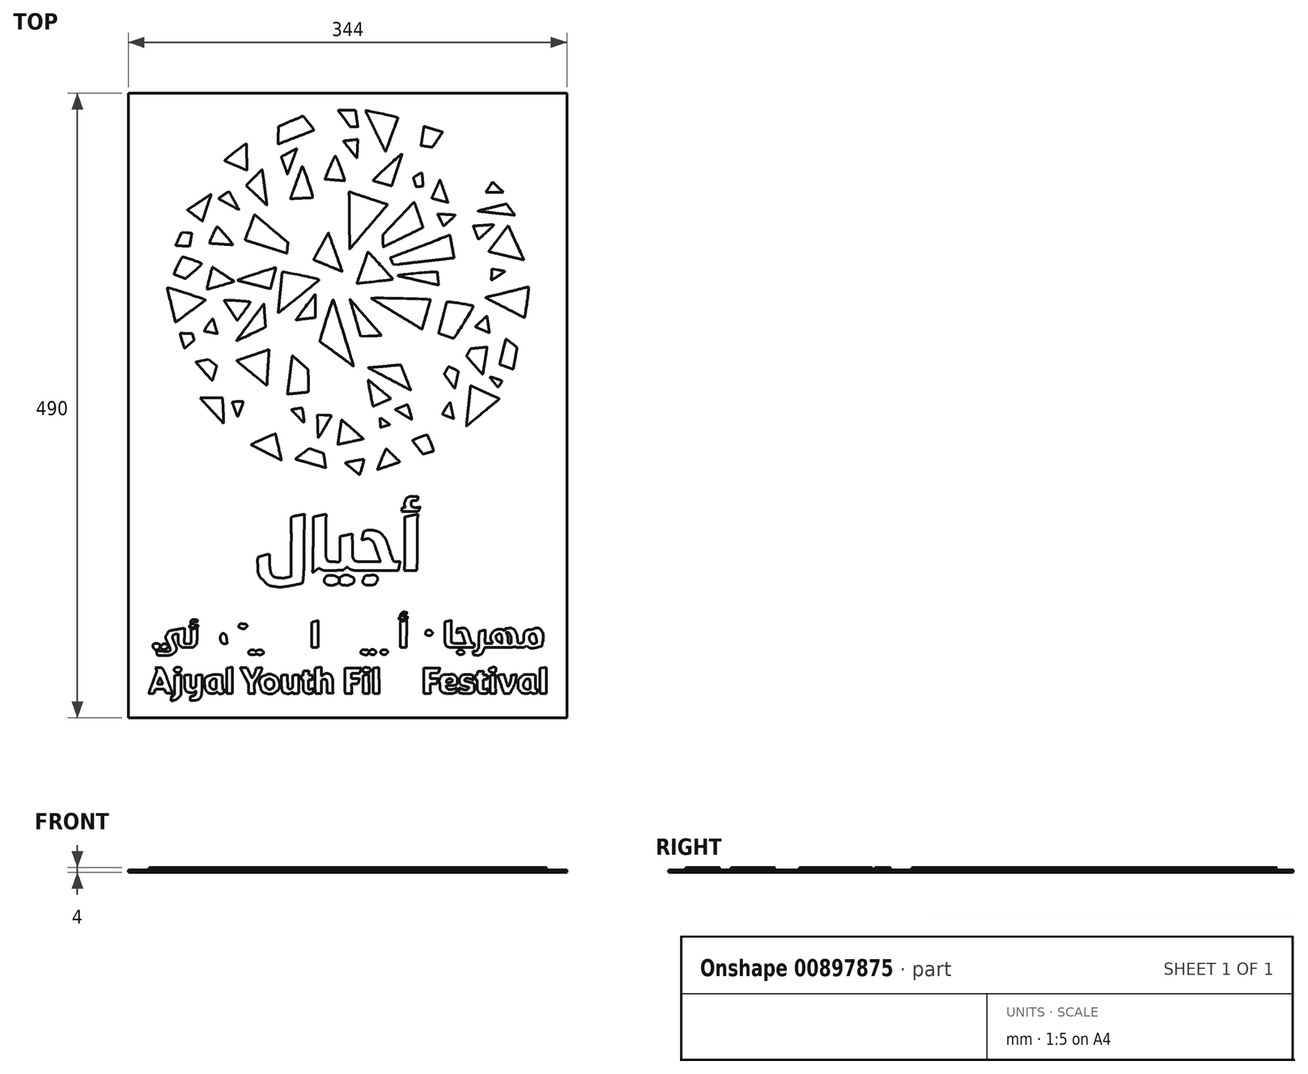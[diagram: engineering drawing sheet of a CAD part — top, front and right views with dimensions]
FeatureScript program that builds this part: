
annotation { "Feature Type Name" : "Feature", "Feature Type Description" : "" }
export const myFeature = defineFeature(function(context is Context, id is Id, definition is map)
    precondition{}
    {
        {
            var Q0;
            Q0=qCreatedBy(makeId("Top.planeOp"),FACE);
            var sketch = newSketch(context, id + "F0", { "sketchPlane" : qUnion([Q0])});
            skLineSegment(sketch, "E0.bottom", {"start": v(172, -245) * mm, "end": v(-172, -245) * mm});
            skLineSegment(sketch, "E0.top", {"start": v(172, 245) * mm, "end": v(-172, 245) * mm});
            skLineSegment(sketch, "E0.left", {"start": v(172, -245) * mm, "end": v(172, 245) * mm});
            skLineSegment(sketch, "E0.right", {"start": v(-172, -245) * mm, "end": v(-172, 245) * mm});
            skPoint(sketch, "E0.middle", {"position": v(0, 0) * mm});
            skSolve(sketch);
        }
        {
            var Q0;
            Q0 = qSketchRegion(id + "F0", true);
            extrude(context, id + "F1", {"entities" : qUnion([Q0]), "oppositeDirection" : true, "depth" : 2 * mm, "offsetDistance" : 25 * mm});
        }
        {
            var Q0;
            Q0=qCreatedBy(makeId("Top.planeOp"),FACE);
            var sketch = newSketch(context, id + "F2", { "sketchPlane" : qUnion([Q0])});
            skLineSegment(sketch, "E1", {"start": v(-135.68, -219.06) * mm, "end": v(-135.68, -211.83) * mm});
            skLineSegment(sketch, "E2", {"start": v(-135.68, -211.83) * mm, "end": v(-134.9, -211.69) * mm});
            skLineSegment(sketch, "E3", {"start": v(-132.5, -211.39) * mm, "end": v(-130.88, -211.23) * mm});
            skLineSegment(sketch, "E4", {"start": v(-130.88, -211.23) * mm, "end": v(-130.88, -218.42) * mm});
            skLineSegment(sketch, "E5", {"start": v(-138.44, -231.46) * mm, "end": v(-138.44, -231.46) * mm});
            skLineSegment(sketch, "E6", {"start": v(-119.02, -224.64) * mm, "end": v(-118.85, -223.71) * mm});
            skLineSegment(sketch, "E7", {"start": v(-118.85, -223.71) * mm, "end": v(-119.5, -224.23) * mm});
            skLineSegment(sketch, "E8", {"start": v(-127.96, -216.75) * mm, "end": v(-128.04, -212.02) * mm});
            skLineSegment(sketch, "E9", {"start": v(-128.04, -212.02) * mm, "end": v(-127.47, -211.8) * mm});
            skLineSegment(sketch, "E10", {"start": v(-125.07, -211.41) * mm, "end": v(-123.23, -211.24) * mm});
            skLineSegment(sketch, "E11", {"start": v(-123.23, -211.24) * mm, "end": v(-123.16, -215.97) * mm});
            skLineSegment(sketch, "E12", {"start": v(-119.97, -221.2) * mm, "end": v(-119.12, -220.8) * mm});
            skLineSegment(sketch, "E13", {"start": v(-119.12, -220.8) * mm, "end": v(-119.12, -216.31) * mm});
            skLineSegment(sketch, "E14", {"start": v(-119.12, -216.31) * mm, "end": v(-119.12, -211.83) * mm});
            skLineSegment(sketch, "E15", {"start": v(-119.12, -211.83) * mm, "end": v(-118.34, -211.69) * mm});
            skLineSegment(sketch, "E16", {"start": v(-115.94, -211.39) * mm, "end": v(-114.32, -211.23) * mm});
            skLineSegment(sketch, "E17", {"start": v(-114.32, -211.23) * mm, "end": v(-114.32, -217.85) * mm});
            skLineSegment(sketch, "E18", {"start": v(-122.07, -231.58) * mm, "end": v(-123.44, -231.75) * mm});
            skLineSegment(sketch, "E19", {"start": v(-123.44, -231.75) * mm, "end": v(-123.44, -230.58) * mm});
            skLineSegment(sketch, "E20", {"start": v(-123.44, -230.58) * mm, "end": v(-123.44, -230.58) * mm});
            skLineSegment(sketch, "E21", {"start": v(-99.32, -211.46) * mm, "end": v(-98.36, -211.67) * mm});
            skLineSegment(sketch, "E22", {"start": v(-98.36, -211.67) * mm, "end": v(-98.24, -217.06) * mm});
            skLineSegment(sketch, "E23", {"start": v(-103.04, -218.4) * mm, "end": v(-103.04, -214.71) * mm});
            skLineSegment(sketch, "E24", {"start": v(-103.04, -214.71) * mm, "end": v(-103.73, -214.57) * mm});
            skLineSegment(sketch, "E25", {"start": v(-63.62, -225.84) * mm, "end": v(-63.62, -225.84) * mm});
            skLineSegment(sketch, "E26", {"start": v(-51.92, -216.04) * mm, "end": v(-51.92, -211.83) * mm});
            skLineSegment(sketch, "E27", {"start": v(-51.92, -211.83) * mm, "end": v(-51.14, -211.69) * mm});
            skLineSegment(sketch, "E28", {"start": v(-48.76, -211.39) * mm, "end": v(-47.15, -211.23) * mm});
            skLineSegment(sketch, "E29", {"start": v(-47.15, -211.23) * mm, "end": v(-47.08, -216.28) * mm});
            skLineSegment(sketch, "E30", {"start": v(-43.75, -221.97) * mm, "end": v(-43.04, -221.6) * mm});
            skLineSegment(sketch, "E31", {"start": v(-43.04, -221.6) * mm, "end": v(-43.04, -216.72) * mm});
            skLineSegment(sketch, "E32", {"start": v(-43.04, -216.72) * mm, "end": v(-43.04, -211.83) * mm});
            skLineSegment(sketch, "E33", {"start": v(-43.04, -211.83) * mm, "end": v(-42.28, -211.68) * mm});
            skLineSegment(sketch, "E34", {"start": v(-39.88, -211.38) * mm, "end": v(-38.24, -211.22) * mm});
            skLineSegment(sketch, "E35", {"start": v(-38.24, -211.22) * mm, "end": v(-38.24, -218.22) * mm});
            skLineSegment(sketch, "E36", {"start": v(-42.8, -225.33) * mm, "end": v(-42.8, -224.76) * mm});
            skLineSegment(sketch, "E37", {"start": v(-42.8, -224.76) * mm, "end": v(-43.94, -225.35) * mm});
            skLineSegment(sketch, "E38", {"start": v(-34.88, -219.02) * mm, "end": v(-34.88, -215.13) * mm});
            skLineSegment(sketch, "E39", {"start": v(-34.88, -215.13) * mm, "end": v(-35.72, -215.13) * mm});
            skLineSegment(sketch, "E40", {"start": v(-35.72, -215.13) * mm, "end": v(-36.56, -215.13) * mm});
            skLineSegment(sketch, "E41", {"start": v(-36.56, -215.13) * mm, "end": v(-36.56, -213.47) * mm});
            skLineSegment(sketch, "E42", {"start": v(-36.56, -213.47) * mm, "end": v(-36.56, -211.8) * mm});
            skLineSegment(sketch, "E43", {"start": v(-36.56, -211.8) * mm, "end": v(-35.78, -211.73) * mm});
            skLineSegment(sketch, "E44", {"start": v(-31.55, -208.25) * mm, "end": v(-30.25, -208.1) * mm});
            skLineSegment(sketch, "E45", {"start": v(-30.25, -208.1) * mm, "end": v(-30.42, -209.8) * mm});
            skLineSegment(sketch, "E46", {"start": v(-30.42, -209.8) * mm, "end": v(-30.59, -211.5) * mm});
            skLineSegment(sketch, "E47", {"start": v(-30.59, -211.5) * mm, "end": v(-28.96, -211.58) * mm});
            skLineSegment(sketch, "E48", {"start": v(-28.96, -211.58) * mm, "end": v(-27.32, -211.65) * mm});
            skLineSegment(sketch, "E49", {"start": v(-27.32, -211.65) * mm, "end": v(-27.4, -213.1) * mm});
            skLineSegment(sketch, "E50", {"start": v(-29.4, -215.13) * mm, "end": v(-30.56, -215.13) * mm});
            skLineSegment(sketch, "E51", {"start": v(-30.56, -215.13) * mm, "end": v(-30.56, -217.86) * mm});
            skLineSegment(sketch, "E52", {"start": v(85.36, -223.4) * mm, "end": v(85.36, -225.2) * mm});
            skLineSegment(sketch, "E53", {"start": v(85.36, -225.2) * mm, "end": v(84.1, -225.55) * mm});
            skLineSegment(sketch, "E54", {"start": v(88.78, -225.67) * mm, "end": v(87.52, -225.42) * mm});
            skLineSegment(sketch, "E55", {"start": v(87.52, -225.42) * mm, "end": v(87.52, -223.68) * mm});
            skLineSegment(sketch, "E56", {"start": v(97.12, -211.35) * mm, "end": v(98.44, -211.66) * mm});
            skLineSegment(sketch, "E57", {"start": v(98.44, -211.66) * mm, "end": v(98.5, -213.55) * mm});
            skLineSegment(sketch, "E58", {"start": v(90.88, -226.02) * mm, "end": v(90.88, -226.02) * mm});
            skLineSegment(sketch, "E59", {"start": v(101.71, -219.15) * mm, "end": v(101.63, -215.13) * mm});
            skLineSegment(sketch, "E60", {"start": v(101.63, -215.13) * mm, "end": v(100.93, -215.13) * mm});
            skLineSegment(sketch, "E61", {"start": v(100.93, -215.13) * mm, "end": v(100.24, -215.13) * mm});
            skLineSegment(sketch, "E62", {"start": v(100.24, -215.13) * mm, "end": v(100.24, -213.45) * mm});
            skLineSegment(sketch, "E63", {"start": v(104.5, -208.54) * mm, "end": v(106.7, -208.36) * mm});
            skLineSegment(sketch, "E64", {"start": v(106.7, -208.36) * mm, "end": v(106.56, -209.95) * mm});
            skLineSegment(sketch, "E65", {"start": v(106.56, -209.95) * mm, "end": v(106.4, -211.53) * mm});
            skLineSegment(sketch, "E66", {"start": v(106.4, -211.53) * mm, "end": v(108, -211.53) * mm});
            skLineSegment(sketch, "E67", {"start": v(108, -211.53) * mm, "end": v(109.6, -211.53) * mm});
            skLineSegment(sketch, "E68", {"start": v(109.6, -211.53) * mm, "end": v(109.6, -212.91) * mm});
            skLineSegment(sketch, "E69", {"start": v(107.82, -215.08) * mm, "end": v(106.48, -215.2) * mm});
            skLineSegment(sketch, "E70", {"start": v(106.48, -215.2) * mm, "end": v(106.48, -218.48) * mm});
            skLineSegment(sketch, "E71", {"start": v(146.62, -211.36) * mm, "end": v(147.52, -211.55) * mm});
            skLineSegment(sketch, "E72", {"start": v(147.52, -211.55) * mm, "end": v(147.52, -216.8) * mm});
            skLineSegment(sketch, "E73", {"start": v(143.14, -218.35) * mm, "end": v(143.08, -214.53) * mm});
            skLineSegment(sketch, "E74", {"start": v(143.08, -214.53) * mm, "end": v(141.94, -214.55) * mm});
            skLineSegment(sketch, "E75", {"start": v(-150.54, -206.67) * mm, "end": v(-151.08, -205.77) * mm});
            skLineSegment(sketch, "E76", {"start": v(-151.08, -205.77) * mm, "end": v(-148.31, -205.77) * mm});
            skLineSegment(sketch, "E77", {"start": v(-148.31, -205.77) * mm, "end": v(-145.54, -205.77) * mm});
            skLineSegment(sketch, "E78", {"start": v(-145.54, -205.77) * mm, "end": v(-144.9, -206.88) * mm});
            skLineSegment(sketch, "E79", {"start": v(-140.04, -225.88) * mm, "end": v(-142.48, -225.81) * mm});
            skLineSegment(sketch, "E80", {"start": v(-142.48, -225.81) * mm, "end": v(-143.08, -224.2) * mm});
            skLineSegment(sketch, "E81", {"start": v(-143.08, -224.2) * mm, "end": v(-143.67, -222.57) * mm});
            skLineSegment(sketch, "E82", {"start": v(-143.67, -222.57) * mm, "end": v(-147.18, -222.57) * mm});
            skLineSegment(sketch, "E83", {"start": v(-147.18, -222.57) * mm, "end": v(-150.7, -222.57) * mm});
            skLineSegment(sketch, "E84", {"start": v(-150.7, -222.57) * mm, "end": v(-151.28, -224.25) * mm});
            skLineSegment(sketch, "E85", {"start": v(-151.28, -224.25) * mm, "end": v(-151.86, -225.93) * mm});
            skLineSegment(sketch, "E86", {"start": v(-151.86, -225.93) * mm, "end": v(-153.84, -225.93) * mm});
            skLineSegment(sketch, "E87", {"start": v(-147.1, -218.73) * mm, "end": v(-145.09, -218.73) * mm});
            skLineSegment(sketch, "E88", {"start": v(-145.09, -218.73) * mm, "end": v(-146.08, -216.21) * mm});
            skLineSegment(sketch, "E89", {"start": v(-94.83, -215.38) * mm, "end": v(-94.76, -205.9) * mm});
            skLineSegment(sketch, "E90", {"start": v(-94.76, -205.9) * mm, "end": v(-92.72, -205.63) * mm});
            skLineSegment(sketch, "E91", {"start": v(-90.52, -215.68) * mm, "end": v(-90.44, -225.93) * mm});
            skLineSegment(sketch, "E92", {"start": v(-90.44, -225.93) * mm, "end": v(-92.54, -225.93) * mm});
            skLineSegment(sketch, "E93", {"start": v(-77.84, -222.14) * mm, "end": v(-77.84, -218.35) * mm});
            skLineSegment(sketch, "E94", {"start": v(-77.84, -218.35) * mm, "end": v(-80.96, -212.36) * mm});
            skLineSegment(sketch, "E95", {"start": v(-81.47, -205.77) * mm, "end": v(-78.87, -205.77) * mm});
            skLineSegment(sketch, "E96", {"start": v(-78.87, -205.77) * mm, "end": v(-77.13, -209.55) * mm});
            skLineSegment(sketch, "E97", {"start": v(-72, -207.17) * mm, "end": v(-71.67, -205.9) * mm});
            skLineSegment(sketch, "E98", {"start": v(-71.67, -205.9) * mm, "end": v(-69.47, -205.82) * mm});
            skLineSegment(sketch, "E99", {"start": v(-71.74, -215.48) * mm, "end": v(-73.35, -218.03) * mm});
            skLineSegment(sketch, "E100", {"start": v(-73.35, -218.03) * mm, "end": v(-73.2, -221.26) * mm});
            skLineSegment(sketch, "E101", {"start": v(-72.89, -225.21) * mm, "end": v(-72.74, -225.93) * mm});
            skLineSegment(sketch, "E102", {"start": v(-72.74, -225.93) * mm, "end": v(-75.3, -225.93) * mm});
            skLineSegment(sketch, "E103", {"start": v(-75.3, -225.93) * mm, "end": v(-77.84, -225.93) * mm});
            skLineSegment(sketch, "E104", {"start": v(-77.84, -225.93) * mm, "end": v(-77.84, -222.14) * mm});
            skLineSegment(sketch, "E105", {"start": v(-20.48, -209.04) * mm, "end": v(-20.48, -212.53) * mm});
            skLineSegment(sketch, "E106", {"start": v(-20.48, -212.53) * mm, "end": v(-19.82, -212.05) * mm});
            skLineSegment(sketch, "E107", {"start": v(-11.54, -223.24) * mm, "end": v(-11.48, -225.95) * mm});
            skLineSegment(sketch, "E108", {"start": v(-11.48, -225.95) * mm, "end": v(-13.76, -225.88) * mm});
            skLineSegment(sketch, "E109", {"start": v(-13.76, -225.88) * mm, "end": v(-16.04, -225.81) * mm});
            skLineSegment(sketch, "E110", {"start": v(-16.04, -225.81) * mm, "end": v(-16.16, -221.01) * mm});
            skLineSegment(sketch, "E111", {"start": v(-19.77, -215.26) * mm, "end": v(-20.48, -215.62) * mm});
            skLineSegment(sketch, "E112", {"start": v(-20.48, -215.62) * mm, "end": v(-20.48, -220.78) * mm});
            skLineSegment(sketch, "E113", {"start": v(-20.48, -220.78) * mm, "end": v(-20.48, -225.93) * mm});
            skLineSegment(sketch, "E114", {"start": v(-20.48, -225.93) * mm, "end": v(-22.72, -225.93) * mm});
            skLineSegment(sketch, "E115", {"start": v(-2.05, -215.67) * mm, "end": v(-2.12, -206.01) * mm});
            skLineSegment(sketch, "E116", {"start": v(-2.12, -206.01) * mm, "end": v(4.3, -206.01) * mm});
            skLineSegment(sketch, "E117", {"start": v(10, -208.35) * mm, "end": v(9.5, -210.1) * mm});
            skLineSegment(sketch, "E118", {"start": v(9.5, -210.1) * mm, "end": v(6.27, -210.1) * mm});
            skLineSegment(sketch, "E119", {"start": v(6.27, -210.1) * mm, "end": v(3.04, -210.1) * mm});
            skLineSegment(sketch, "E120", {"start": v(3.04, -210.1) * mm, "end": v(3.04, -212.25) * mm});
            skLineSegment(sketch, "E121", {"start": v(3.04, -212.25) * mm, "end": v(3.04, -214.41) * mm});
            skLineSegment(sketch, "E122", {"start": v(3.04, -214.41) * mm, "end": v(6.16, -214.41) * mm});
            skLineSegment(sketch, "E123", {"start": v(8.7, -216.45) * mm, "end": v(8.15, -218.37) * mm});
            skLineSegment(sketch, "E124", {"start": v(8.15, -218.37) * mm, "end": v(5.57, -218.44) * mm});
            skLineSegment(sketch, "E125", {"start": v(5.57, -218.44) * mm, "end": v(2.98, -218.5) * mm});
            skLineSegment(sketch, "E126", {"start": v(2.98, -218.5) * mm, "end": v(3.1, -221.8) * mm});
            skLineSegment(sketch, "E127", {"start": v(12.16, -218.1) * mm, "end": v(12.16, -211.78) * mm});
            skLineSegment(sketch, "E128", {"start": v(12.16, -211.78) * mm, "end": v(12.7, -211.66) * mm});
            skLineSegment(sketch, "E129", {"start": v(16.76, -218.55) * mm, "end": v(16.84, -225.93) * mm});
            skLineSegment(sketch, "E130", {"start": v(16.84, -225.93) * mm, "end": v(14.65, -225.93) * mm});
            skLineSegment(sketch, "E131", {"start": v(14.65, -225.93) * mm, "end": v(12.46, -225.93) * mm});
            skLineSegment(sketch, "E132", {"start": v(12.46, -225.93) * mm, "end": v(12.3, -225.18) * mm});
            skLineSegment(sketch, "E133", {"start": v(20.13, -215.26) * mm, "end": v(20.2, -206.14) * mm});
            skLineSegment(sketch, "E134", {"start": v(20.2, -206.14) * mm, "end": v(22.24, -205.85) * mm});
            skLineSegment(sketch, "E135", {"start": v(24.7, -215.92) * mm, "end": v(24.76, -225.93) * mm});
            skLineSegment(sketch, "E136", {"start": v(24.76, -225.93) * mm, "end": v(22.55, -225.93) * mm});
            skLineSegment(sketch, "E137", {"start": v(22.55, -225.93) * mm, "end": v(20.34, -225.93) * mm});
            skLineSegment(sketch, "E138", {"start": v(20.34, -225.93) * mm, "end": v(20.2, -225.15) * mm});
            skLineSegment(sketch, "E139", {"start": v(39.76, -212.17) * mm, "end": v(40.47, -212.77) * mm});
            skLineSegment(sketch, "E140", {"start": v(40.47, -212.77) * mm, "end": v(41.18, -212.27) * mm});
            skLineSegment(sketch, "E141", {"start": v(50.27, -220.47) * mm, "end": v(50.37, -225.93) * mm});
            skLineSegment(sketch, "E142", {"start": v(50.37, -225.93) * mm, "end": v(48.09, -225.93) * mm});
            skLineSegment(sketch, "E143", {"start": v(41.44, -220.67) * mm, "end": v(41.44, -225.95) * mm});
            skLineSegment(sketch, "E144", {"start": v(41.44, -225.95) * mm, "end": v(39.22, -225.88) * mm});
            skLineSegment(sketch, "E145", {"start": v(39.22, -225.88) * mm, "end": v(37, -225.81) * mm});
            skLineSegment(sketch, "E146", {"start": v(37, -225.81) * mm, "end": v(36.88, -220.86) * mm});
            skLineSegment(sketch, "E147", {"start": v(33.27, -215.26) * mm, "end": v(32.56, -215.62) * mm});
            skLineSegment(sketch, "E148", {"start": v(32.56, -215.62) * mm, "end": v(32.56, -220.78) * mm});
            skLineSegment(sketch, "E149", {"start": v(32.56, -220.78) * mm, "end": v(32.56, -225.93) * mm});
            skLineSegment(sketch, "E150", {"start": v(32.56, -225.93) * mm, "end": v(30.32, -225.93) * mm});
            skLineSegment(sketch, "E151", {"start": v(59.7, -207.03) * mm, "end": v(59.5, -206.01) * mm});
            skLineSegment(sketch, "E152", {"start": v(59.5, -206.01) * mm, "end": v(65.95, -206.01) * mm});
            skLineSegment(sketch, "E153", {"start": v(71.83, -208.05) * mm, "end": v(71.27, -209.97) * mm});
            skLineSegment(sketch, "E154", {"start": v(71.27, -209.97) * mm, "end": v(68.11, -210.04) * mm});
            skLineSegment(sketch, "E155", {"start": v(68.11, -210.04) * mm, "end": v(64.96, -210.1) * mm});
            skLineSegment(sketch, "E156", {"start": v(64.96, -210.1) * mm, "end": v(64.96, -212.26) * mm});
            skLineSegment(sketch, "E157", {"start": v(64.96, -212.26) * mm, "end": v(64.96, -214.41) * mm});
            skLineSegment(sketch, "E158", {"start": v(64.96, -214.41) * mm, "end": v(67.96, -214.41) * mm});
            skLineSegment(sketch, "E159", {"start": v(70.24, -217.47) * mm, "end": v(69.98, -218.5) * mm});
            skLineSegment(sketch, "E160", {"start": v(69.98, -218.5) * mm, "end": v(67.44, -218.5) * mm});
            skLineSegment(sketch, "E161", {"start": v(67.44, -218.5) * mm, "end": v(64.9, -218.5) * mm});
            skLineSegment(sketch, "E162", {"start": v(64.9, -218.5) * mm, "end": v(65, -222.21) * mm});
            skLineSegment(sketch, "E163", {"start": v(65, -222.21) * mm, "end": v(65.1, -225.93) * mm});
            skLineSegment(sketch, "E164", {"start": v(65.1, -225.93) * mm, "end": v(62.5, -225.93) * mm});
            skLineSegment(sketch, "E165", {"start": v(62.5, -225.93) * mm, "end": v(59.92, -225.93) * mm});
            skLineSegment(sketch, "E166", {"start": v(59.92, -225.93) * mm, "end": v(59.9, -217) * mm});
            skLineSegment(sketch, "E167", {"start": v(59.9, -217) * mm, "end": v(59.9, -217) * mm});
            skLineSegment(sketch, "E168", {"start": v(111.81, -218.5) * mm, "end": v(111.88, -211.66) * mm});
            skLineSegment(sketch, "E169", {"start": v(111.88, -211.66) * mm, "end": v(113.92, -211.4) * mm});
            skLineSegment(sketch, "E170", {"start": v(116.12, -218.55) * mm, "end": v(116.2, -225.93) * mm});
            skLineSegment(sketch, "E171", {"start": v(116.2, -225.93) * mm, "end": v(114.1, -225.93) * mm});
            skLineSegment(sketch, "E172", {"start": v(128.55, -223.64) * mm, "end": v(127.28, -225.93) * mm});
            skLineSegment(sketch, "E173", {"start": v(127.28, -225.93) * mm, "end": v(125.03, -225.93) * mm});
            skLineSegment(sketch, "E174", {"start": v(151, -215.61) * mm, "end": v(151, -206.14) * mm});
            skLineSegment(sketch, "E175", {"start": v(151, -206.14) * mm, "end": v(153.28, -205.86) * mm});
            skLineSegment(sketch, "E176", {"start": v(155.92, -215.87) * mm, "end": v(155.92, -225.93) * mm});
            skLineSegment(sketch, "E177", {"start": v(155.92, -225.93) * mm, "end": v(153.63, -225.93) * mm});
            skLineSegment(sketch, "E178", {"start": v(-129.1, -174.9) * mm, "end": v(-127.83, -174.75) * mm});
            skLineSegment(sketch, "E179", {"start": v(-127.83, -174.75) * mm, "end": v(-127.94, -179.52) * mm});
            skLineSegment(sketch, "E180", {"start": v(-132.8, -182.3) * mm, "end": v(-132.8, -179.07) * mm});
            skLineSegment(sketch, "E181", {"start": v(-132.8, -179.07) * mm, "end": v(-133.81, -179.23) * mm});
            skLineSegment(sketch, "E182", {"start": v(-13.71, -186.7) * mm, "end": v(-13.64, -184.85) * mm});
            skLineSegment(sketch, "E183", {"start": v(-13.64, -184.85) * mm, "end": v(-11.84, -184.27) * mm});
            skLineSegment(sketch, "E184", {"start": v(-2.96, -192.59) * mm, "end": v(-1.35, -192.3) * mm});
            skLineSegment(sketch, "E185", {"start": v(-1.35, -192.3) * mm, "end": v(-1.2, -190.84) * mm});
            skLineSegment(sketch, "E186", {"start": v(55.65, -186.95) * mm, "end": v(55.72, -184.85) * mm});
            skLineSegment(sketch, "E187", {"start": v(55.72, -184.85) * mm, "end": v(57.52, -184.27) * mm});
            skLineSegment(sketch, "E188", {"start": v(66.34, -192.58) * mm, "end": v(68.08, -192.29) * mm});
            skLineSegment(sketch, "E189", {"start": v(68.08, -192.29) * mm, "end": v(68.08, -184.06) * mm});
            skLineSegment(sketch, "E190", {"start": v(68.08, -184.06) * mm, "end": v(68.08, -175.83) * mm});
            skLineSegment(sketch, "E191", {"start": v(68.08, -175.83) * mm, "end": v(70.3, -175.32) * mm});
            skLineSegment(sketch, "E192", {"start": v(98.52, -194.37) * mm, "end": v(98.14, -192.81) * mm});
            skLineSegment(sketch, "E193", {"start": v(98.14, -192.81) * mm, "end": v(99.13, -192.81) * mm});
            skLineSegment(sketch, "E194", {"start": v(103.08, -183.53) * mm, "end": v(103.15, -177.24) * mm});
            skLineSegment(sketch, "E195", {"start": v(103.15, -177.24) * mm, "end": v(105.27, -176.75) * mm});
            skLineSegment(sketch, "E196", {"start": v(111.88, -186.57) * mm, "end": v(113.9, -186.57) * mm});
            skLineSegment(sketch, "E197", {"start": v(113.9, -186.57) * mm, "end": v(113.26, -185.2) * mm});
            skLineSegment(sketch, "E198", {"start": v(122.6, -176.52) * mm, "end": v(123.28, -177) * mm});
            skLineSegment(sketch, "E199", {"start": v(123.28, -177) * mm, "end": v(123.52, -176.37) * mm});
            skLineSegment(sketch, "E200", {"start": v(152.7, -187.11) * mm, "end": v(152.52, -188.93) * mm});
            skLineSegment(sketch, "E201", {"start": v(152.52, -188.93) * mm, "end": v(149.74, -189.58) * mm});
            skLineSegment(sketch, "E202", {"start": v(141.59, -189.38) * mm, "end": v(140.34, -188.74) * mm});
            skLineSegment(sketch, "E203", {"start": v(140.34, -188.74) * mm, "end": v(139.43, -189.27) * mm});
            skLineSegment(sketch, "E204", {"start": v(100.24, -195.93) * mm, "end": v(98.9, -195.93) * mm});
            skLineSegment(sketch, "E205", {"start": v(98.9, -195.93) * mm, "end": v(98.52, -194.37) * mm});
            skLineSegment(sketch, "E206", {"start": v(98.52, -194.37) * mm, "end": v(98.52, -194.37) * mm});
            skLineSegment(sketch, "E207", {"start": v(125.86, -184.11) * mm, "end": v(125.99, -186.57) * mm});
            skLineSegment(sketch, "E208", {"start": v(125.99, -186.57) * mm, "end": v(127.18, -186.57) * mm});
            skLineSegment(sketch, "E209", {"start": v(127.18, -186.57) * mm, "end": v(128.37, -186.57) * mm});
            skLineSegment(sketch, "E210", {"start": v(128.37, -186.57) * mm, "end": v(128.28, -183.87) * mm});
            skLineSegment(sketch, "E211", {"start": v(-70.34, -195.33) * mm, "end": v(-70.34, -195.33) * mm});
            skLineSegment(sketch, "E212", {"start": v(27.76, -186.53) * mm, "end": v(32.3, -186.6) * mm});
            skLineSegment(sketch, "E213", {"start": v(32.3, -186.6) * mm, "end": v(31.34, -183.89) * mm});
            skLineSegment(sketch, "E214", {"start": v(39.18, -189.28) * mm, "end": v(39.02, -189.95) * mm});
            skLineSegment(sketch, "E215", {"start": v(39.02, -189.95) * mm, "end": v(30.21, -189.88) * mm});
            skLineSegment(sketch, "E216", {"start": v(20.62, -189.26) * mm, "end": v(19.85, -188.7) * mm});
            skLineSegment(sketch, "E217", {"start": v(19.85, -188.7) * mm, "end": v(19.1, -189.26) * mm});
            skLineSegment(sketch, "E218", {"start": v(10.08, -189.57) * mm, "end": v(9.04, -189.17) * mm});
            skLineSegment(sketch, "E219", {"start": v(9.04, -189.17) * mm, "end": v(8.15, -189.91) * mm});
            skLineSegment(sketch, "E220", {"start": v(-115.04, -177.66) * mm, "end": v(-115.04, -170.07) * mm});
            skLineSegment(sketch, "E221", {"start": v(-115.04, -170.07) * mm, "end": v(-113.01, -169.56) * mm});
            skLineSegment(sketch, "E222", {"start": v(-84.32, -180.76) * mm, "end": v(-84.32, -177.22) * mm});
            skLineSegment(sketch, "E223", {"start": v(-84.32, -177.22) * mm, "end": v(-83.66, -177.07) * mm});
            skLineSegment(sketch, "E224", {"start": v(-54.6, -181.12) * mm, "end": v(-54.5, -177.22) * mm});
            skLineSegment(sketch, "E225", {"start": v(-54.5, -177.22) * mm, "end": v(-53.63, -177) * mm});
            skLineSegment(sketch, "E226", {"start": v(-45.96, -180.55) * mm, "end": v(-45.88, -175.77) * mm});
            skLineSegment(sketch, "E227", {"start": v(-45.88, -175.77) * mm, "end": v(-45.24, -175.63) * mm});
            skLineSegment(sketch, "E228", {"start": v(-58.46, -190.12) * mm, "end": v(-58.46, -190.12) * mm});
            skLineSegment(sketch, "E229", {"start": v(-28.16, -180.09) * mm, "end": v(-28.16, -170.24) * mm});
            skLineSegment(sketch, "E230", {"start": v(-28.16, -170.24) * mm, "end": v(-27.62, -170.01) * mm});
            skLineSegment(sketch, "E231", {"start": v(-23.25, -189.15) * mm, "end": v(-23.38, -189.93) * mm});
            skLineSegment(sketch, "E232", {"start": v(-23.38, -189.93) * mm, "end": v(-25.77, -189.93) * mm});
            skLineSegment(sketch, "E233", {"start": v(-25.77, -189.93) * mm, "end": v(-28.16, -189.93) * mm});
            skLineSegment(sketch, "E234", {"start": v(-28.16, -189.93) * mm, "end": v(-28.16, -180.09) * mm});
            skLineSegment(sketch, "E235", {"start": v(46.1, -188.67) * mm, "end": v(45.96, -189.93) * mm});
            skLineSegment(sketch, "E236", {"start": v(45.96, -189.93) * mm, "end": v(43.64, -189.93) * mm});
            skLineSegment(sketch, "E237", {"start": v(43.64, -189.93) * mm, "end": v(41.32, -189.93) * mm});
            skLineSegment(sketch, "E238", {"start": v(41.32, -189.93) * mm, "end": v(41.39, -179.92) * mm});
            skLineSegment(sketch, "E239", {"start": v(76.24, -177.53) * mm, "end": v(76.24, -169.78) * mm});
            skLineSegment(sketch, "E240", {"start": v(76.24, -169.78) * mm, "end": v(76.78, -169.66) * mm});
            skLineSegment(sketch, "E241", {"start": v(99.26, -186.57) * mm, "end": v(99.92, -186.57) * mm});
            skLineSegment(sketch, "E242", {"start": v(99.92, -186.57) * mm, "end": v(99.54, -188.25) * mm});
            skLineSegment(sketch, "E243", {"start": v(99.54, -188.25) * mm, "end": v(99.16, -189.93) * mm});
            skLineSegment(sketch, "E244", {"start": v(99.16, -189.93) * mm, "end": v(89.68, -189.9) * mm});
            skLineSegment(sketch, "E245", {"start": v(-118.35, -172.33) * mm, "end": v(-117.15, -172.19) * mm});
            skLineSegment(sketch, "E246", {"start": v(-117.15, -172.19) * mm, "end": v(-117.31, -172.84) * mm});
            skLineSegment(sketch, "E247", {"start": v(-124, -173.93) * mm, "end": v(-124, -173.93) * mm});
            skLineSegment(sketch, "E248", {"start": v(-70.47, -120.1) * mm, "end": v(-70.27, -119.02) * mm});
            skLineSegment(sketch, "E249", {"start": v(-70.27, -119.02) * mm, "end": v(-66.68, -117.9) * mm});
            skLineSegment(sketch, "E250", {"start": v(-62.12, -116.75) * mm, "end": v(-61.16, -116.73) * mm});
            skLineSegment(sketch, "E251", {"start": v(-61.16, -116.73) * mm, "end": v(-61.25, -120.8) * mm});
            skLineSegment(sketch, "E252", {"start": v(-2.41, -140.95) * mm, "end": v(-2.41, -140.95) * mm});
            skLineSegment(sketch, "E253", {"start": v(-27.05, -107.55) * mm, "end": v(-26.9, -87.45) * mm});
            skLineSegment(sketch, "E254", {"start": v(-26.9, -87.45) * mm, "end": v(-26.4, -87.33) * mm});
            skLineSegment(sketch, "E255", {"start": v(-17.5, -85.53) * mm, "end": v(-16.65, -85.53) * mm});
            skLineSegment(sketch, "E256", {"start": v(-16.65, -85.53) * mm, "end": v(-16.83, -87.03) * mm});
            skLineSegment(sketch, "E257", {"start": v(-17, -103.77) * mm, "end": v(-17, -119.01) * mm});
            skLineSegment(sketch, "E258", {"start": v(-17, -119.01) * mm, "end": v(-16.44, -120.14) * mm});
            skLineSegment(sketch, "E259", {"start": v(-6.08, -109.85) * mm, "end": v(-6.08, -102.86) * mm});
            skLineSegment(sketch, "E260", {"start": v(-6.08, -102.86) * mm, "end": v(-3.98, -102.38) * mm});
            skLineSegment(sketch, "E261", {"start": v(17.01, -122.5) * mm, "end": v(26.06, -122.5) * mm});
            skLineSegment(sketch, "E262", {"start": v(26.06, -122.5) * mm, "end": v(25.61, -121.71) * mm});
            skLineSegment(sketch, "E263", {"start": v(11.96, -101.92) * mm, "end": v(12.78, -98.61) * mm});
            skLineSegment(sketch, "E264", {"start": v(12.78, -98.61) * mm, "end": v(13.97, -98.3) * mm});
            skLineSegment(sketch, "E265", {"start": v(40.43, -126.25) * mm, "end": v(39.67, -129.45) * mm});
            skLineSegment(sketch, "E266", {"start": v(39.67, -129.45) * mm, "end": v(22.48, -129.45) * mm});
            skLineSegment(sketch, "E267", {"start": v(-21.39, -128.33) * mm, "end": v(-22.9, -127.73) * mm});
            skLineSegment(sketch, "E268", {"start": v(-22.9, -127.73) * mm, "end": v(-24.7, -129.12) * mm});
            skLineSegment(sketch, "E269", {"start": v(-27.47, -130.78) * mm, "end": v(-27.47, -130.78) * mm});
            skLineSegment(sketch, "E270", {"start": v(54.42, -85.53) * mm, "end": v(55.33, -85.53) * mm});
            skLineSegment(sketch, "E271", {"start": v(55.33, -85.53) * mm, "end": v(55.2, -86.43) * mm});
            skLineSegment(sketch, "E272", {"start": v(49.18, -129.45) * mm, "end": v(44.26, -129.45) * mm});
            skLineSegment(sketch, "E273", {"start": v(44.26, -129.45) * mm, "end": v(44.46, -128.91) * mm});
            skLineSegment(sketch, "E274", {"start": v(42.6, -81.63) * mm, "end": v(43, -80.13) * mm});
            skLineSegment(sketch, "E275", {"start": v(43, -80.13) * mm, "end": v(44.26, -80.06) * mm});
            skLineSegment(sketch, "E276", {"start": v(44.26, -80.06) * mm, "end": v(45.52, -79.99) * mm});
            skLineSegment(sketch, "E277", {"start": v(45.52, -79.99) * mm, "end": v(45.16, -79.3) * mm});
            skLineSegment(sketch, "E278", {"start": v(54.95, -73.45) * mm, "end": v(54.55, -74.74) * mm});
            skLineSegment(sketch, "E279", {"start": v(54.55, -74.74) * mm, "end": v(52.73, -74.59) * mm});
            skLineSegment(sketch, "E280", {"start": v(48.12, -83.13) * mm, "end": v(42.2, -83.13) * mm});
            skLineSegment(sketch, "E281", {"start": v(42.2, -83.13) * mm, "end": v(42.6, -81.63) * mm});
            skLineSegment(sketch, "E282", {"start": v(42.6, -81.63) * mm, "end": v(42.6, -81.63) * mm});
            skLineSegment(sketch, "E283", {"start": v(-35.46, -37.64) * mm, "end": v(-30.2, -33.53) * mm});
            skLineSegment(sketch, "E284", {"start": v(-30.2, -33.53) * mm, "end": v(-24.55, -35.42) * mm});
            skLineSegment(sketch, "E285", {"start": v(-24.55, -35.42) * mm, "end": v(-18.9, -37.3) * mm});
            skLineSegment(sketch, "E286", {"start": v(-18.9, -37.3) * mm, "end": v(-18.1, -42.64) * mm});
            skLineSegment(sketch, "E287", {"start": v(78.43, -18.24) * mm, "end": v(80.85, -19.6) * mm});
            skLineSegment(sketch, "E288", {"start": v(80.85, -19.6) * mm, "end": v(77.65, -22.8) * mm});
            skLineSegment(sketch, "E289", {"start": v(-23.5, -13.53) * mm, "end": v(-23.65, -7.16) * mm});
            skLineSegment(sketch, "E290", {"start": v(-23.65, -7.16) * mm, "end": v(-18.28, -7.5) * mm});
            skLineSegment(sketch, "E291", {"start": v(25.64, -10.58) * mm, "end": v(25.72, -9.42) * mm});
            skLineSegment(sketch, "E292", {"start": v(25.72, -9.42) * mm, "end": v(29.37, -12.14) * mm});
            skLineSegment(sketch, "E293", {"start": v(-113.09, 3.03) * mm, "end": v(-115.88, 6.03) * mm});
            skLineSegment(sketch, "E294", {"start": v(-115.88, 6.03) * mm, "end": v(-107.14, 6.1) * mm});
            skLineSegment(sketch, "E295", {"start": v(29.97, 8.8) * mm, "end": v(33.98, 5.49) * mm});
            skLineSegment(sketch, "E296", {"start": v(33.98, 5.49) * mm, "end": v(27.33, 2.55) * mm});
            skLineSegment(sketch, "E297", {"start": v(-37.03, 33.68) * mm, "end": v(-30.92, 28.34) * mm});
            skLineSegment(sketch, "E298", {"start": v(-30.92, 28.34) * mm, "end": v(-30.87, 19.7) * mm});
            skLineSegment(sketch, "E299", {"start": v(-110.65, 35.78) * mm, "end": v(-109.02, 36.1) * mm});
            skLineSegment(sketch, "E300", {"start": v(-109.02, 36.1) * mm, "end": v(-105.97, 33.7) * mm});
            skLineSegment(sketch, "E301", {"start": v(128.88, 48.81) * mm, "end": v(133.06, 45.52) * mm});
            skLineSegment(sketch, "E302", {"start": v(133.06, 45.52) * mm, "end": v(132.87, 44.5) * mm});
            skLineSegment(sketch, "E303", {"start": v(-126.42, 56.6) * mm, "end": v(-121.85, 56.48) * mm});
            skLineSegment(sketch, "E304", {"start": v(-121.85, 56.48) * mm, "end": v(-121.08, 53.94) * mm});
            skLineSegment(sketch, "E305", {"start": v(-121.08, 53.94) * mm, "end": v(-120.3, 51.39) * mm});
            skLineSegment(sketch, "E306", {"start": v(-120.3, 51.39) * mm, "end": v(-121, 50.79) * mm});
            skLineSegment(sketch, "E307", {"start": v(-65.04, 69.9) * mm, "end": v(-64.5, 61.54) * mm});
            skLineSegment(sketch, "E308", {"start": v(-64.5, 61.54) * mm, "end": v(-65.41, 61.08) * mm});
            skLineSegment(sketch, "E309", {"start": v(14.79, 68.67) * mm, "end": v(26.82, 54.99) * mm});
            skLineSegment(sketch, "E310", {"start": v(26.82, 54.99) * mm, "end": v(24.11, 54.84) * mm});
            skLineSegment(sketch, "E311", {"start": v(15.85, 54.5) * mm, "end": v(10.3, 54.33) * mm});
            skLineSegment(sketch, "E312", {"start": v(10.3, 54.33) * mm, "end": v(10.04, 55.14) * mm});
            skLineSegment(sketch, "E313", {"start": v(10.04, 55.14) * mm, "end": v(10.04, 55.14) * mm});
            skLineSegment(sketch, "E314", {"start": v(-25.28, 77.83) * mm, "end": v(-25.28, 68.79) * mm});
            skLineSegment(sketch, "E315", {"start": v(-25.28, 68.79) * mm, "end": v(-26, 68.79) * mm});
            skLineSegment(sketch, "E316", {"start": v(34.58, 100.3) * mm, "end": v(35.7, 99.05) * mm});
            skLineSegment(sketch, "E317", {"start": v(35.7, 99.05) * mm, "end": v(34.9, 98.92) * mm});
            skLineSegment(sketch, "E318", {"start": v(113.17, 106.49) * mm, "end": v(113.2, 107.35) * mm});
            skLineSegment(sketch, "E319", {"start": v(113.2, 107.35) * mm, "end": v(118.16, 106.43) * mm});
            skLineSegment(sketch, "E320", {"start": v(40.87, 110.95) * mm, "end": v(36.1, 110.4) * mm});
            skLineSegment(sketch, "E321", {"start": v(36.1, 110.4) * mm, "end": v(34.8, 113.13) * mm});
            skLineSegment(sketch, "E322", {"start": v(124.1, 138.84) * mm, "end": v(126, 141.38) * mm});
            skLineSegment(sketch, "E323", {"start": v(126, 141.38) * mm, "end": v(126.4, 140.42) * mm});
            skLineSegment(sketch, "E324", {"start": v(27.7, 130.5) * mm, "end": v(27.64, 134) * mm});
            skLineSegment(sketch, "E325", {"start": v(27.64, 134) * mm, "end": v(39.83, 146.75) * mm});
            skLineSegment(sketch, "E326", {"start": v(-131.54, 133.12) * mm, "end": v(-130.23, 135.9) * mm});
            skLineSegment(sketch, "E327", {"start": v(-130.23, 135.9) * mm, "end": v(-126.33, 135.6) * mm});
            skLineSegment(sketch, "E328", {"start": v(-123.12, 130) * mm, "end": v(-124.04, 124.95) * mm});
            skLineSegment(sketch, "E329", {"start": v(-124.04, 124.95) * mm, "end": v(-125.24, 124.98) * mm});
            skLineSegment(sketch, "E330", {"start": v(72.8, 145.74) * mm, "end": v(70.44, 150.46) * mm});
            skLineSegment(sketch, "E331", {"start": v(70.44, 150.46) * mm, "end": v(72.32, 150.31) * mm});
            skLineSegment(sketch, "E332", {"start": v(-71.54, 165.1) * mm, "end": v(-79.5, 172.83) * mm});
            skLineSegment(sketch, "E333", {"start": v(-79.5, 172.83) * mm, "end": v(-73.34, 179.01) * mm});
            skLineSegment(sketch, "E334", {"start": v(112.47, 173.48) * mm, "end": v(113.82, 175.57) * mm});
            skLineSegment(sketch, "E335", {"start": v(113.82, 175.57) * mm, "end": v(118, 171.38) * mm});
            skLineSegment(sketch, "E336", {"start": v(118, 171.38) * mm, "end": v(122.2, 167.19) * mm});
            skLineSegment(sketch, "E337", {"start": v(122.2, 167.19) * mm, "end": v(115.3, 167.19) * mm});
            skLineSegment(sketch, "E338", {"start": v(115.3, 167.19) * mm, "end": v(108.4, 167.19) * mm});
            skLineSegment(sketch, "E339", {"start": v(108.4, 167.19) * mm, "end": v(109.77, 169.29) * mm});
            skLineSegment(sketch, "E340", {"start": v(76.77, 190.74) * mm, "end": v(75.99, 191.58) * mm});
            skLineSegment(sketch, "E341", {"start": v(75.99, 191.58) * mm, "end": v(77.08, 194.08) * mm});
            skLineSegment(sketch, "E342", {"start": v(7.36, 208.87) * mm, "end": v(7.96, 208.98) * mm});
            skLineSegment(sketch, "E343", {"start": v(7.96, 208.98) * mm, "end": v(7.67, 201.96) * mm});
            skLineSegment(sketch, "E344", {"start": v(4.91, 218.78) * mm, "end": v(2.1, 218.9) * mm});
            skLineSegment(sketch, "E345", {"start": v(2.1, 218.9) * mm, "end": v(-2.58, 225.15) * mm});
            skLineSegment(sketch, "E346", {"start": v(-0.58, 231.75) * mm, "end": v(6.12, 231.75) * mm});
            skLineSegment(sketch, "E347", {"start": v(6.12, 231.75) * mm, "end": v(6.25, 231.09) * mm});
            skFitSpline(sketch, "E348", {"points": [v(-138.44, -231.46) * mm, v(-138.52, -231.33) * mm, v(-138.51, -230.57) * mm, v(-138.42, -229.78) * mm]});
            skFitSpline(sketch, "E349", {"points": [v(-138.42, -229.78) * mm, v(-138.27, -228.41) * mm, v(-138.23, -228.34) * mm, v(-137.43, -228.08) * mm]});
            skFitSpline(sketch, "E350", {"points": [v(-137.43, -228.08) * mm, v(-136.94, -227.91) * mm, v(-136.42, -227.5) * mm, v(-136.14, -227.05) * mm]});
            skFitSpline(sketch, "E351", {"points": [v(-136.14, -227.05) * mm, v(-135.72, -226.35) * mm, v(-135.68, -225.77) * mm, v(-135.68, -219.06) * mm]});
            skFitSpline(sketch, "E352", {"points": [v(-134.9, -211.69) * mm, v(-134.47, -211.6) * mm, v(-133.4, -211.47) * mm, v(-132.5, -211.39) * mm]});
            skFitSpline(sketch, "E353", {"points": [v(-130.88, -218.42) * mm, v(-130.88, -227.06) * mm, v(-130.97, -227.55) * mm, v(-132.9, -229.44) * mm]});
            skFitSpline(sketch, "E354", {"points": [v(-132.9, -229.44) * mm, v(-133.75, -230.27) * mm, v(-134.55, -230.8) * mm, v(-135.34, -231.04) * mm]});
            skFitSpline(sketch, "E355", {"points": [v(-135.34, -231.04) * mm, v(-137.05, -231.58) * mm, v(-138.26, -231.75) * mm, v(-138.44, -231.46) * mm]});
            skFitSpline(sketch, "E356", {"points": [v(-123.44, -230.58) * mm, v(-123.43, -228.7) * mm, v(-123.28, -228.4) * mm, v(-122.14, -228.12) * mm]});
            skFitSpline(sketch, "E357", {"points": [v(-122.14, -228.12) * mm, v(-120.34, -227.67) * mm, v(-119.37, -226.58) * mm, v(-119.02, -224.64) * mm]});
            skFitSpline(sketch, "E358", {"points": [v(-119.5, -224.23) * mm, v(-120.64, -225.12) * mm, v(-122.51, -225.53) * mm, v(-124.04, -225.21) * mm]});
            skFitSpline(sketch, "E359", {"points": [v(-124.04, -225.21) * mm, v(-125.65, -224.88) * mm, v(-126.7, -224.05) * mm, v(-127.37, -222.58) * mm]});
            skFitSpline(sketch, "E360", {"points": [v(-127.37, -222.58) * mm, v(-127.82, -221.62) * mm, v(-127.88, -220.94) * mm, v(-127.96, -216.75) * mm]});
            skFitSpline(sketch, "E361", {"points": [v(-127.47, -211.8) * mm, v(-127.16, -211.68) * mm, v(-126.08, -211.5) * mm, v(-125.07, -211.41) * mm]});
            skFitSpline(sketch, "E362", {"points": [v(-123.16, -215.97) * mm, v(-123.08, -220.6) * mm, v(-123.07, -220.7) * mm, v(-122.52, -221.15) * mm]});
            skFitSpline(sketch, "E363", {"points": [v(-122.52, -221.15) * mm, v(-121.82, -221.72) * mm, v(-121.07, -221.73) * mm, v(-119.97, -221.2) * mm]});
            skFitSpline(sketch, "E364", {"points": [v(-118.34, -211.69) * mm, v(-117.91, -211.6) * mm, v(-116.83, -211.47) * mm, v(-115.94, -211.39) * mm]});
            skFitSpline(sketch, "E365", {"points": [v(-114.32, -217.85) * mm, v(-114.32, -221.61) * mm, v(-114.43, -224.98) * mm, v(-114.58, -225.66) * mm]});
            skFitSpline(sketch, "E366", {"points": [v(-114.58, -225.66) * mm, v(-115.26, -228.83) * mm, v(-118.1, -231.08) * mm, v(-122.07, -231.58) * mm]});
            skFitSpline(sketch, "E367", {"points": [v(-107.81, -225.93) * mm, v(-109.1, -225.63) * mm, v(-110.5, -224.48) * mm, v(-111.29, -223.06) * mm]});
            skFitSpline(sketch, "E368", {"points": [v(-111.29, -223.06) * mm, v(-111.93, -221.92) * mm, v(-112.04, -221.46) * mm, v(-112.12, -219.54) * mm]});
            skFitSpline(sketch, "E369", {"points": [v(-112.12, -219.54) * mm, v(-112.3, -215.28) * mm, v(-110.8, -212.9) * mm, v(-107.12, -211.63) * mm]});
            skFitSpline(sketch, "E370", {"points": [v(-107.12, -211.63) * mm, v(-106.09, -211.27) * mm, v(-105.2, -211.18) * mm, v(-103.04, -211.2) * mm]});
            skFitSpline(sketch, "E371", {"points": [v(-103.04, -211.2) * mm, v(-101.52, -211.23) * mm, v(-99.85, -211.34) * mm, v(-99.32, -211.46) * mm]});
            skFitSpline(sketch, "E372", {"points": [v(-98.24, -217.06) * mm, v(-98.12, -222.43) * mm, v(-98.12, -222.45) * mm, v(-97.58, -222.53) * mm]});
            skFitSpline(sketch, "E373", {"points": [v(-97.58, -222.53) * mm, v(-97.1, -222.6) * mm, v(-97.04, -222.74) * mm, v(-97.04, -224.02) * mm]});
            skFitSpline(sketch, "E374", {"points": [v(-97.04, -224.02) * mm, v(-97.04, -225.56) * mm, v(-97.17, -225.72) * mm, v(-98.68, -226.05) * mm]});
            skFitSpline(sketch, "E375", {"points": [v(-98.68, -226.05) * mm, v(-99.82, -226.3) * mm, v(-101, -226.01) * mm, v(-101.84, -225.3) * mm]});
            skFitSpline(sketch, "E376", {"points": [v(-101.84, -225.3) * mm, v(-102.54, -224.7) * mm, v(-102.6, -224.7) * mm, v(-103.03, -225.08) * mm]});
            skFitSpline(sketch, "E377", {"points": [v(-103.03, -225.08) * mm, v(-103.56, -225.56) * mm, v(-105.5, -226.18) * mm, v(-106.38, -226.15) * mm]});
            skFitSpline(sketch, "E378", {"points": [v(-106.38, -226.15) * mm, v(-106.72, -226.13) * mm, v(-107.37, -226.04) * mm, v(-107.81, -225.93) * mm]});
            skFitSpline(sketch, "E379", {"points": [v(-103.5, -222.32) * mm, v(-103.08, -222.1) * mm, v(-103.04, -221.79) * mm, v(-103.04, -218.4) * mm]});
            skFitSpline(sketch, "E380", {"points": [v(-103.73, -214.57) * mm, v(-104.68, -214.38) * mm, v(-105.97, -214.78) * mm, v(-106.6, -215.45) * mm]});
            skFitSpline(sketch, "E381", {"points": [v(-106.6, -215.45) * mm, v(-108, -216.94) * mm, v(-107.93, -220.94) * mm, v(-106.48, -222.08) * mm]});
            skFitSpline(sketch, "E382", {"points": [v(-106.48, -222.08) * mm, v(-105.8, -222.62) * mm, v(-104.29, -222.74) * mm, v(-103.5, -222.32) * mm]});
            skFitSpline(sketch, "E383", {"points": [v(-63.62, -225.84) * mm, v(-66.15, -225.2) * mm, v(-67.7, -223.59) * mm, v(-68.4, -220.83) * mm]});
            skFitSpline(sketch, "E384", {"points": [v(-68.4, -220.83) * mm, v(-69.4, -216.94) * mm, v(-67.8, -213.22) * mm, v(-64.52, -211.73) * mm]});
            skFitSpline(sketch, "E385", {"points": [v(-64.52, -211.73) * mm, v(-62.81, -210.96) * mm, v(-59.76, -210.97) * mm, v(-58, -211.75) * mm]});
            skFitSpline(sketch, "E386", {"points": [v(-58, -211.75) * mm, v(-56.34, -212.48) * mm, v(-54.75, -214.2) * mm, v(-54.2, -215.83) * mm]});
            skFitSpline(sketch, "E387", {"points": [v(-54.2, -215.83) * mm, v(-53.24, -218.74) * mm, v(-54.18, -222.83) * mm, v(-56.18, -224.48) * mm]});
            skFitSpline(sketch, "E388", {"points": [v(-56.18, -224.48) * mm, v(-57.87, -225.87) * mm, v(-61.14, -226.47) * mm, v(-63.62, -225.84) * mm]});
            skFitSpline(sketch, "E389", {"points": [v(-60.05, -222.31) * mm, v(-58.35, -221.4) * mm, v(-58.15, -216.4) * mm, v(-59.76, -215.14) * mm]});
            skFitSpline(sketch, "E390", {"points": [v(-59.76, -215.14) * mm, v(-60.44, -214.61) * mm, v(-61.74, -214.5) * mm, v(-62.5, -214.9) * mm]});
            skFitSpline(sketch, "E391", {"points": [v(-62.5, -214.9) * mm, v(-64.1, -215.76) * mm, v(-64.3, -220.44) * mm, v(-62.8, -221.95) * mm]});
            skFitSpline(sketch, "E392", {"points": [v(-62.8, -221.95) * mm, v(-62.12, -222.62) * mm, v(-60.92, -222.78) * mm, v(-60.05, -222.31) * mm]});
            skFitSpline(sketch, "E393", {"points": [v(-48.3, -225.95) * mm, v(-50.1, -225.5) * mm, v(-51.26, -224.04) * mm, v(-51.66, -221.77) * mm]});
            skFitSpline(sketch, "E394", {"points": [v(-51.66, -221.77) * mm, v(-51.8, -220.94) * mm, v(-51.92, -218.36) * mm, v(-51.92, -216.04) * mm]});
            skFitSpline(sketch, "E395", {"points": [v(-51.14, -211.69) * mm, v(-50.71, -211.6) * mm, v(-49.64, -211.47) * mm, v(-48.76, -211.39) * mm]});
            skFitSpline(sketch, "E396", {"points": [v(-47.08, -216.28) * mm, v(-47, -220.84) * mm, v(-46.96, -221.37) * mm, v(-46.54, -221.83) * mm]});
            skFitSpline(sketch, "E397", {"points": [v(-46.54, -221.83) * mm, v(-46, -222.43) * mm, v(-44.77, -222.5) * mm, v(-43.75, -221.97) * mm]});
            skFitSpline(sketch, "E398", {"points": [v(-42.28, -211.68) * mm, v(-41.86, -211.6) * mm, v(-40.78, -211.46) * mm, v(-39.88, -211.38) * mm]});
            skFitSpline(sketch, "E399", {"points": [v(-38.24, -218.22) * mm, v(-38.24, -222.06) * mm, v(-38.24, -225.3) * mm, v(-38.23, -225.4) * mm]});
            skFitSpline(sketch, "E400", {"points": [v(-38.23, -225.4) * mm, v(-38.22, -225.6) * mm, v(-42.33, -226.2) * mm, v(-42.61, -226.02) * mm]});
            skFitSpline(sketch, "E401", {"points": [v(-42.61, -226.02) * mm, v(-42.72, -225.96) * mm, v(-42.8, -225.65) * mm, v(-42.8, -225.33) * mm]});
            skFitSpline(sketch, "E402", {"points": [v(-43.94, -225.35) * mm, v(-45.21, -226) * mm, v(-47.05, -226.26) * mm, v(-48.3, -225.95) * mm]});
            skFitSpline(sketch, "E403", {"points": [v(-31.97, -225.91) * mm, v(-33.24, -225.52) * mm, v(-33.86, -225.01) * mm, v(-34.39, -223.92) * mm]});
            skFitSpline(sketch, "E404", {"points": [v(-34.39, -223.92) * mm, v(-34.82, -223.02) * mm, v(-34.88, -222.44) * mm, v(-34.88, -219.02) * mm]});
            skFitSpline(sketch, "E405", {"points": [v(-35.78, -211.73) * mm, v(-35.02, -211.65) * mm, v(-35, -211.62) * mm, v(-34.85, -210.24) * mm]});
            skFitSpline(sketch, "E406", {"points": [v(-34.85, -210.24) * mm, v(-34.7, -208.76) * mm, v(-34.43, -208.42) * mm, v(-33.44, -208.41) * mm]});
            skFitSpline(sketch, "E407", {"points": [v(-33.44, -208.41) * mm, v(-33.11, -208.41) * mm, v(-32.26, -208.34) * mm, v(-31.55, -208.25) * mm]});
            skFitSpline(sketch, "E408", {"points": [v(-27.4, -213.1) * mm, v(-27.5, -214.82) * mm, v(-27.8, -215.13) * mm, v(-29.4, -215.13) * mm]});
            skFitSpline(sketch, "E409", {"points": [v(-30.56, -217.86) * mm, v(-30.56, -222.33) * mm, v(-30.28, -222.86) * mm, v(-28.23, -222.34) * mm]});
            skFitSpline(sketch, "E410", {"points": [v(-28.23, -222.34) * mm, v(-27.63, -222.2) * mm, v(-27.09, -222.12) * mm, v(-27.02, -222.2) * mm]});
            skFitSpline(sketch, "E411", {"points": [v(-27.02, -222.2) * mm, v(-26.96, -222.26) * mm, v(-26.98, -223.02) * mm, v(-27.07, -223.9) * mm]});
            skFitSpline(sketch, "E412", {"points": [v(-27.07, -223.9) * mm, v(-27.23, -225.32) * mm, v(-27.3, -225.5) * mm, v(-27.88, -225.73) * mm]});
            skFitSpline(sketch, "E413", {"points": [v(-27.88, -225.73) * mm, v(-28.82, -226.1) * mm, v(-31.04, -226.2) * mm, v(-31.97, -225.9) * mm]});
            skFitSpline(sketch, "E414", {"points": [v(78.35, -225.91) * mm, v(74.83, -225.4) * mm, v(72.75, -223.08) * mm, v(72.47, -219.36) * mm]});
            skFitSpline(sketch, "E415", {"points": [v(72.47, -219.36) * mm, v(72.11, -214.67) * mm, v(74.99, -211.4) * mm, v(79.74, -211.1) * mm]});
            skFitSpline(sketch, "E416", {"points": [v(79.74, -211.1) * mm, v(82.13, -210.95) * mm, v(83.84, -211.48) * mm, v(84.96, -212.72) * mm]});
            skFitSpline(sketch, "E417", {"points": [v(84.96, -212.72) * mm, v(85.98, -213.85) * mm, v(86.18, -214.5) * mm, v(86.02, -216.12) * mm]});
            skFitSpline(sketch, "E418", {"points": [v(86.02, -216.12) * mm, v(85.78, -218.65) * mm, v(84.55, -219.43) * mm, v(80.38, -219.72) * mm]});
            skFitSpline(sketch, "E419", {"points": [v(80.38, -219.72) * mm, v(78.72, -219.84) * mm, v(77.33, -219.96) * mm, v(77.3, -220) * mm]});
            skFitSpline(sketch, "E420", {"points": [v(77.3, -220) * mm, v(77.27, -220.03) * mm, v(77.4, -220.45) * mm, v(77.6, -220.94) * mm]});
            skFitSpline(sketch, "E421", {"points": [v(77.6, -220.94) * mm, v(78.03, -222) * mm, v(79.48, -222.81) * mm, v(80.93, -222.8) * mm]});
            skFitSpline(sketch, "E422", {"points": [v(80.93, -222.8) * mm, v(81.97, -222.8) * mm, v(84, -222.32) * mm, v(84.83, -221.88) * mm]});
            skFitSpline(sketch, "E423", {"points": [v(84.83, -221.88) * mm, v(85.35, -221.6) * mm, v(85.36, -221.61) * mm, v(85.36, -223.4) * mm]});
            skFitSpline(sketch, "E424", {"points": [v(84.1, -225.55) * mm, v(82.42, -226) * mm, v(80.03, -226.16) * mm, v(78.35, -225.91) * mm]});
            skFitSpline(sketch, "E425", {"points": [v(81.7, -216.68) * mm, v(82.42, -216.18) * mm, v(82.38, -215.52) * mm, v(81.6, -214.9) * mm]});
            skFitSpline(sketch, "E426", {"points": [v(81.6, -214.9) * mm, v(80.9, -214.35) * mm, v(80.26, -214.3) * mm, v(79.16, -214.67) * mm]});
            skFitSpline(sketch, "E427", {"points": [v(79.16, -214.67) * mm, v(78.46, -214.92) * mm, v(77.44, -216.17) * mm, v(77.44, -216.78) * mm]});
            skFitSpline(sketch, "E428", {"points": [v(77.44, -216.78) * mm, v(77.44, -217.22) * mm, v(81.05, -217.13) * mm, v(81.7, -216.68) * mm]});
            skFitSpline(sketch, "E429", {"points": [v(90.88, -226.02) * mm, v(90.42, -225.96) * mm, v(89.47, -225.8) * mm, v(88.78, -225.67) * mm]});
            skFitSpline(sketch, "E430", {"points": [v(87.52, -223.68) * mm, v(87.52, -222.72) * mm, v(87.58, -221.87) * mm, v(87.65, -221.8) * mm]});
            skFitSpline(sketch, "E431", {"points": [v(87.65, -221.8) * mm, v(87.72, -221.73) * mm, v(88.4, -221.93) * mm, v(89.15, -222.24) * mm]});
            skFitSpline(sketch, "E432", {"points": [v(89.15, -222.24) * mm, v(90.84, -222.93) * mm, v(93.73, -223.04) * mm, v(94.34, -222.44) * mm]});
            skFitSpline(sketch, "E433", {"points": [v(94.34, -222.44) * mm, v(95.24, -221.53) * mm, v(94.55, -220.92) * mm, v(91.9, -220.3) * mm]});
            skFitSpline(sketch, "E434", {"points": [v(91.9, -220.3) * mm, v(90, -219.84) * mm, v(88.93, -219.24) * mm, v(88.14, -218.17) * mm]});
            skFitSpline(sketch, "E435", {"points": [v(88.14, -218.17) * mm, v(87.75, -217.64) * mm, v(87.64, -217.15) * mm, v(87.64, -215.86) * mm]});
            skFitSpline(sketch, "E436", {"points": [v(87.64, -215.86) * mm, v(87.64, -214.39) * mm, v(87.72, -214.12) * mm, v(88.37, -213.3) * mm]});
            skFitSpline(sketch, "E437", {"points": [v(88.37, -213.3) * mm, v(89.53, -211.84) * mm, v(91.06, -211.2) * mm, v(93.63, -211.11) * mm]});
            skFitSpline(sketch, "E438", {"points": [v(93.63, -211.11) * mm, v(94.86, -211.07) * mm, v(96.37, -211.17) * mm, v(97.12, -211.35) * mm]});
            skFitSpline(sketch, "E439", {"points": [v(98.5, -213.55) * mm, v(98.57, -215.28) * mm, v(98.54, -215.42) * mm, v(98.15, -215.27) * mm]});
            skFitSpline(sketch, "E440", {"points": [v(98.15, -215.27) * mm, v(95.97, -214.42) * mm, v(92.73, -214.24) * mm, v(92.3, -214.93) * mm]});
            skFitSpline(sketch, "E441", {"points": [v(92.3, -214.93) * mm, v(91.73, -215.81) * mm, v(92.1, -216.08) * mm, v(95.11, -216.95) * mm]});
            skFitSpline(sketch, "E442", {"points": [v(95.11, -216.95) * mm, v(98.37, -217.9) * mm, v(99.35, -218.89) * mm, v(99.35, -221.25) * mm]});
            skFitSpline(sketch, "E443", {"points": [v(99.35, -221.25) * mm, v(99.35, -224.12) * mm, v(97.26, -225.72) * mm, v(93.16, -226.02) * mm]});
            skFitSpline(sketch, "E444", {"points": [v(93.16, -226.02) * mm, v(92.37, -226.07) * mm, v(91.34, -226.07) * mm, v(90.88, -226.02) * mm]});
            skFitSpline(sketch, "E445", {"points": [v(105.04, -225.91) * mm, v(103.74, -225.65) * mm, v(102.92, -225.08) * mm, v(102.28, -223.99) * mm]});
            skFitSpline(sketch, "E446", {"points": [v(102.28, -223.99) * mm, v(101.86, -223.28) * mm, v(101.79, -222.65) * mm, v(101.71, -219.15) * mm]});
            skFitSpline(sketch, "E447", {"points": [v(100.24, -213.45) * mm, v(100.24, -211.77) * mm, v(100.24, -211.76) * mm, v(100.95, -211.62) * mm]});
            skFitSpline(sketch, "E448", {"points": [v(100.95, -211.62) * mm, v(101.6, -211.49) * mm, v(101.68, -211.36) * mm, v(101.82, -210.33) * mm]});
            skFitSpline(sketch, "E449", {"points": [v(101.82, -210.33) * mm, v(101.9, -209.7) * mm, v(102.04, -209.08) * mm, v(102.13, -208.95) * mm]});
            skFitSpline(sketch, "E450", {"points": [v(102.13, -208.95) * mm, v(102.2, -208.82) * mm, v(103.27, -208.63) * mm, v(104.5, -208.54) * mm]});
            skFitSpline(sketch, "E451", {"points": [v(109.6, -212.91) * mm, v(109.6, -213.67) * mm, v(109.5, -214.44) * mm, v(109.38, -214.63) * mm]});
            skFitSpline(sketch, "E452", {"points": [v(109.38, -214.63) * mm, v(109.25, -214.83) * mm, v(108.6, -215.02) * mm, v(107.82, -215.08) * mm]});
            skFitSpline(sketch, "E453", {"points": [v(106.48, -218.48) * mm, v(106.48, -222.6) * mm, v(106.54, -222.7) * mm, v(108.63, -222.5) * mm]});
            skFitSpline(sketch, "E454", {"points": [v(108.63, -222.5) * mm, v(110.1, -222.34) * mm, v(110.13, -222.34) * mm, v(109.99, -222.87) * mm]});
            skFitSpline(sketch, "E455", {"points": [v(109.99, -222.87) * mm, v(109.9, -223.17) * mm, v(109.84, -223.87) * mm, v(109.84, -224.44) * mm]});
            skFitSpline(sketch, "E456", {"points": [v(109.84, -224.44) * mm, v(109.84, -225.28) * mm, v(109.74, -225.5) * mm, v(109.3, -225.67) * mm]});
            skFitSpline(sketch, "E457", {"points": [v(109.3, -225.67) * mm, v(108.38, -226.01) * mm, v(106.17, -226.14) * mm, v(105.04, -225.91) * mm]});
            skFitSpline(sketch, "E458", {"points": [v(138.48, -225.92) * mm, v(137.04, -225.64) * mm, v(136.16, -225.12) * mm, v(135.21, -224) * mm]});
            skFitSpline(sketch, "E459", {"points": [v(135.21, -224) * mm, v(134.16, -222.78) * mm, v(133.72, -221.27) * mm, v(133.73, -218.97) * mm]});
            skFitSpline(sketch, "E460", {"points": [v(133.73, -218.97) * mm, v(133.74, -216.5) * mm, v(134.33, -214.85) * mm, v(135.75, -213.44) * mm]});
            skFitSpline(sketch, "E461", {"points": [v(135.75, -213.44) * mm, v(137.5, -211.7) * mm, v(139.03, -211.2) * mm, v(142.72, -211.18) * mm]});
            skFitSpline(sketch, "E462", {"points": [v(142.72, -211.18) * mm, v(144.37, -211.18) * mm, v(146.12, -211.26) * mm, v(146.62, -211.36) * mm]});
            skFitSpline(sketch, "E463", {"points": [v(147.52, -216.8) * mm, v(147.52, -219.7) * mm, v(147.58, -222.22) * mm, v(147.66, -222.43) * mm]});
            skFitSpline(sketch, "E464", {"points": [v(147.66, -222.43) * mm, v(147.74, -222.64) * mm, v(148.07, -222.81) * mm, v(148.38, -222.81) * mm]});
            skFitSpline(sketch, "E465", {"points": [v(148.38, -222.81) * mm, v(149.01, -222.81) * mm, v(149.08, -223.13) * mm, v(148.8, -224.78) * mm]});
            skFitSpline(sketch, "E466", {"points": [v(148.8, -224.78) * mm, v(148.67, -225.6) * mm, v(148.59, -225.68) * mm, v(147.54, -225.9) * mm]});
            skFitSpline(sketch, "E467", {"points": [v(147.54, -225.9) * mm, v(146.25, -226.18) * mm, v(144.83, -225.94) * mm, v(144.15, -225.33) * mm]});
            skFitSpline(sketch, "E468", {"points": [v(144.15, -225.33) * mm, v(143.73, -224.94) * mm, v(143.64, -224.95) * mm, v(142.67, -225.4) * mm]});
            skFitSpline(sketch, "E469", {"points": [v(142.67, -225.4) * mm, v(141.4, -226) * mm, v(139.81, -226.2) * mm, v(138.48, -225.92) * mm]});
            skFitSpline(sketch, "E470", {"points": [v(142.9, -222.37) * mm, v(143.14, -222.22) * mm, v(143.2, -221.25) * mm, v(143.14, -218.35) * mm]});
            skFitSpline(sketch, "E471", {"points": [v(141.94, -214.55) * mm, v(140.62, -214.57) * mm, v(139.73, -215.11) * mm, v(139, -216.35) * mm]});
            skFitSpline(sketch, "E472", {"points": [v(139, -216.35) * mm, v(138.07, -217.95) * mm, v(138.54, -221.6) * mm, v(139.78, -222.31) * mm]});
            skFitSpline(sketch, "E473", {"points": [v(139.78, -222.31) * mm, v(140.28, -222.6) * mm, v(142.47, -222.65) * mm, v(142.9, -222.37) * mm]});
            skFitSpline(sketch, "E474", {"points": [v(-155.92, -225.75) * mm, v(-155.97, -225.65) * mm, v(-154.57, -221.68) * mm, v(-152.8, -216.93) * mm]});
            skFitSpline(sketch, "E475", {"points": [v(-152.8, -216.93) * mm, v(-150.64, -211.13) * mm, v(-149.65, -208.17) * mm, v(-149.79, -207.93) * mm]});
            skFitSpline(sketch, "E476", {"points": [v(-149.79, -207.93) * mm, v(-149.9, -207.73) * mm, v(-150.24, -207.17) * mm, v(-150.54, -206.67) * mm]});
            skFitSpline(sketch, "E477", {"points": [v(-144.9, -206.88) * mm, v(-144.1, -208.25) * mm, v(-142.7, -211.46) * mm, v(-141.73, -214.17) * mm]});
            skFitSpline(sketch, "E478", {"points": [v(-141.73, -214.17) * mm, v(-141.33, -215.3) * mm, v(-140.23, -218.3) * mm, v(-139.3, -220.85) * mm]});
            skFitSpline(sketch, "E479", {"points": [v(-139.3, -220.85) * mm, v(-138.37, -223.4) * mm, v(-137.6, -225.59) * mm, v(-137.6, -225.72) * mm]});
            skFitSpline(sketch, "E480", {"points": [v(-137.6, -225.72) * mm, v(-137.6, -225.86) * mm, v(-138.58, -225.92) * mm, v(-140.04, -225.88) * mm]});
            skFitSpline(sketch, "E481", {"points": [v(-153.84, -225.93) * mm, v(-154.92, -225.93) * mm, v(-155.86, -225.85) * mm, v(-155.92, -225.75) * mm]});
            skFitSpline(sketch, "E482", {"points": [v(-146.08, -216.21) * mm, v(-146.63, -214.83) * mm, v(-147.14, -213.7) * mm, v(-147.2, -213.7) * mm]});
            skFitSpline(sketch, "E483", {"points": [v(-147.2, -213.7) * mm, v(-147.32, -213.7) * mm, v(-149.12, -218.27) * mm, v(-149.12, -218.58) * mm]});
            skFitSpline(sketch, "E484", {"points": [v(-149.12, -218.58) * mm, v(-149.12, -218.66) * mm, v(-148.21, -218.73) * mm, v(-147.1, -218.73) * mm]});
            skFitSpline(sketch, "E485", {"points": [v(-94.76, -225.4) * mm, v(-94.84, -225.1) * mm, v(-94.87, -220.59) * mm, v(-94.83, -215.38) * mm]});
            skFitSpline(sketch, "E486", {"points": [v(-92.72, -205.63) * mm, v(-91.6, -205.48) * mm, v(-90.66, -205.37) * mm, v(-90.64, -205.4) * mm]});
            skFitSpline(sketch, "E487", {"points": [v(-90.64, -205.4) * mm, v(-90.61, -205.4) * mm, v(-90.56, -210.03) * mm, v(-90.52, -215.68) * mm]});
            skFitSpline(sketch, "E488", {"points": [v(-92.54, -225.93) * mm, v(-94.51, -225.93) * mm, v(-94.64, -225.9) * mm, v(-94.76, -225.4) * mm]});
            skFitSpline(sketch, "E489", {"points": [v(-80.96, -212.36) * mm, v(-82.67, -209.07) * mm, v(-84.08, -206.24) * mm, v(-84.08, -206.07) * mm]});
            skFitSpline(sketch, "E490", {"points": [v(-84.08, -206.07) * mm, v(-84.08, -205.85) * mm, v(-83.4, -205.77) * mm, v(-81.47, -205.77) * mm]});
            skFitSpline(sketch, "E491", {"points": [v(-77.13, -209.55) * mm, v(-76.17, -211.63) * mm, v(-75.3, -213.42) * mm, v(-75.2, -213.53) * mm]});
            skFitSpline(sketch, "E492", {"points": [v(-75.2, -213.53) * mm, v(-74.95, -213.8) * mm, v(-72.4, -208.74) * mm, v(-72, -207.17) * mm]});
            skFitSpline(sketch, "E493", {"points": [v(-69.47, -205.82) * mm, v(-68.27, -205.79) * mm, v(-67.28, -205.85) * mm, v(-67.28, -205.96) * mm]});
            skFitSpline(sketch, "E494", {"points": [v(-67.28, -205.96) * mm, v(-67.28, -207.3) * mm, v(-69.3, -211.63) * mm, v(-71.74, -215.48) * mm]});
            skFitSpline(sketch, "E495", {"points": [v(-73.2, -221.26) * mm, v(-73.1, -223.04) * mm, v(-72.96, -224.82) * mm, v(-72.89, -225.21) * mm]});
            skFitSpline(sketch, "E496", {"points": [v(-25.12, -225.77) * mm, v(-25.27, -225.63) * mm, v(-25.36, -206.03) * mm, v(-25.22, -206) * mm]});
            skFitSpline(sketch, "E497", {"points": [v(-25.22, -206) * mm, v(-24.6, -205.83) * mm, v(-20.8, -205.38) * mm, v(-20.66, -205.46) * mm]});
            skFitSpline(sketch, "E498", {"points": [v(-20.66, -205.46) * mm, v(-20.56, -205.51) * mm, v(-20.48, -207.13) * mm, v(-20.48, -209.04) * mm]});
            skFitSpline(sketch, "E499", {"points": [v(-19.82, -212.05) * mm, v(-17.35, -210.3) * mm, v(-13.53, -211.1) * mm, v(-12.29, -213.63) * mm]});
            skFitSpline(sketch, "E500", {"points": [v(-12.29, -213.63) * mm, v(-11.81, -214.6) * mm, v(-11.72, -215.2) * mm, v(-11.66, -217.65) * mm]});
            skFitSpline(sketch, "E501", {"points": [v(-11.66, -217.65) * mm, v(-11.63, -219.24) * mm, v(-11.57, -221.75) * mm, v(-11.54, -223.24) * mm]});
            skFitSpline(sketch, "E502", {"points": [v(-16.16, -221.01) * mm, v(-16.28, -216.16) * mm, v(-16.43, -215.36) * mm, v(-17.25, -215.04) * mm]});
            skFitSpline(sketch, "E503", {"points": [v(-17.25, -215.04) * mm, v(-17.93, -214.78) * mm, v(-19.04, -214.88) * mm, v(-19.77, -215.26) * mm]});
            skFitSpline(sketch, "E504", {"points": [v(-22.72, -225.93) * mm, v(-23.95, -225.93) * mm, v(-25.03, -225.86) * mm, v(-25.12, -225.77) * mm]});
            skFitSpline(sketch, "E505", {"points": [v(-1.88, -225.63) * mm, v(-1.94, -225.47) * mm, v(-2.02, -220.99) * mm, v(-2.05, -215.67) * mm]});
            skFitSpline(sketch, "E506", {"points": [v(4.3, -206.01) * mm, v(9.31, -206.01) * mm, v(10.68, -206.08) * mm, v(10.6, -206.31) * mm]});
            skFitSpline(sketch, "E507", {"points": [v(10.6, -206.31) * mm, v(10.55, -206.48) * mm, v(10.28, -207.4) * mm, v(10, -208.35) * mm]});
            skFitSpline(sketch, "E508", {"points": [v(6.16, -214.41) * mm, v(7.87, -214.41) * mm, v(9.28, -214.44) * mm, v(9.27, -214.47) * mm]});
            skFitSpline(sketch, "E509", {"points": [v(9.27, -214.47) * mm, v(9.27, -214.5) * mm, v(9.02, -215.4) * mm, v(8.7, -216.45) * mm]});
            skFitSpline(sketch, "E510", {"points": [v(3.1, -221.8) * mm, v(3.15, -223.61) * mm, v(3.29, -225.28) * mm, v(3.39, -225.51) * mm]});
            skFitSpline(sketch, "E511", {"points": [v(3.39, -225.51) * mm, v(3.55, -225.9) * mm, v(3.35, -225.93) * mm, v(0.9, -225.93) * mm]});
            skFitSpline(sketch, "E512", {"points": [v(0.9, -225.93) * mm, v(-1.03, -225.93) * mm, v(-1.8, -225.85) * mm, v(-1.88, -225.63) * mm]});
            skFitSpline(sketch, "E513", {"points": [v(12.3, -225.18) * mm, v(12.23, -224.77) * mm, v(12.16, -221.59) * mm, v(12.16, -218.1) * mm]});
            skFitSpline(sketch, "E514", {"points": [v(12.7, -211.66) * mm, v(13.3, -211.52) * mm, v(16.58, -211.1) * mm, v(16.64, -211.14) * mm]});
            skFitSpline(sketch, "E515", {"points": [v(16.64, -211.14) * mm, v(16.66, -211.16) * mm, v(16.71, -214.5) * mm, v(16.76, -218.55) * mm]});
            skFitSpline(sketch, "E516", {"points": [v(20.2, -225.15) * mm, v(20.12, -224.72) * mm, v(20.1, -220.27) * mm, v(20.13, -215.26) * mm]});
            skFitSpline(sketch, "E517", {"points": [v(22.24, -205.85) * mm, v(23.36, -205.7) * mm, v(24.36, -205.64) * mm, v(24.45, -205.73) * mm]});
            skFitSpline(sketch, "E518", {"points": [v(24.45, -205.73) * mm, v(24.55, -205.83) * mm, v(24.66, -210.41) * mm, v(24.7, -215.92) * mm]});
            skFitSpline(sketch, "E519", {"points": [v(27.92, -225.77) * mm, v(27.77, -225.63) * mm, v(27.68, -211.8) * mm, v(27.82, -211.76) * mm]});
            skFitSpline(sketch, "E520", {"points": [v(27.82, -211.76) * mm, v(28.43, -211.6) * mm, v(32.25, -211.14) * mm, v(32.38, -211.22) * mm]});
            skFitSpline(sketch, "E521", {"points": [v(32.38, -211.22) * mm, v(32.48, -211.27) * mm, v(32.56, -211.53) * mm, v(32.56, -211.79) * mm]});
            skFitSpline(sketch, "E522", {"points": [v(32.56, -211.79) * mm, v(32.56, -212.37) * mm, v(32.58, -212.36) * mm, v(33.62, -211.75) * mm]});
            skFitSpline(sketch, "E523", {"points": [v(33.62, -211.75) * mm, v(34.68, -211.12) * mm, v(36.98, -210.89) * mm, v(38.17, -211.28) * mm]});
            skFitSpline(sketch, "E524", {"points": [v(38.17, -211.28) * mm, v(38.65, -211.44) * mm, v(39.37, -211.84) * mm, v(39.76, -212.17) * mm]});
            skFitSpline(sketch, "E525", {"points": [v(41.18, -212.27) * mm, v(43.54, -210.58) * mm, v(47.13, -210.7) * mm, v(48.8, -212.52) * mm]});
            skFitSpline(sketch, "E526", {"points": [v(48.8, -212.52) * mm, v(50.02, -213.84) * mm, v(50.16, -214.65) * mm, v(50.27, -220.47) * mm]});
            skFitSpline(sketch, "E527", {"points": [v(48.09, -225.93) * mm, v(46.23, -225.93) * mm, v(45.78, -225.86) * mm, v(45.66, -225.55) * mm]});
            skFitSpline(sketch, "E528", {"points": [v(45.66, -225.55) * mm, v(45.58, -225.34) * mm, v(45.52, -223.3) * mm, v(45.52, -221.03) * mm]});
            skFitSpline(sketch, "E529", {"points": [v(45.52, -221.03) * mm, v(45.52, -215.56) * mm, v(45.27, -214.9) * mm, v(43.24, -214.9) * mm]});
            skFitSpline(sketch, "E530", {"points": [v(43.24, -214.9) * mm, v(41.4, -214.9) * mm, v(41.44, -214.75) * mm, v(41.44, -220.67) * mm]});
            skFitSpline(sketch, "E531", {"points": [v(36.88, -220.86) * mm, v(36.77, -216.42) * mm, v(36.71, -215.85) * mm, v(36.3, -215.4) * mm]});
            skFitSpline(sketch, "E532", {"points": [v(36.3, -215.4) * mm, v(35.75, -214.78) * mm, v(34.3, -214.72) * mm, v(33.27, -215.26) * mm]});
            skFitSpline(sketch, "E533", {"points": [v(30.32, -225.93) * mm, v(29.09, -225.93) * mm, v(28, -225.86) * mm, v(27.92, -225.77) * mm]});
            skFitSpline(sketch, "E534", {"points": [v(59.9, -217) * mm, v(59.9, -212.08) * mm, v(59.8, -207.6) * mm, v(59.7, -207.03) * mm]});
            skFitSpline(sketch, "E535", {"points": [v(65.95, -206.01) * mm, v(69.5, -206.01) * mm, v(72.4, -206.04) * mm, v(72.4, -206.07) * mm]});
            skFitSpline(sketch, "E536", {"points": [v(72.4, -206.07) * mm, v(72.39, -206.1) * mm, v(72.13, -207) * mm, v(71.83, -208.05) * mm]});
            skFitSpline(sketch, "E537", {"points": [v(67.96, -214.41) * mm, v(69.6, -214.41) * mm, v(70.96, -214.5) * mm, v(70.96, -214.6) * mm]});
            skFitSpline(sketch, "E538", {"points": [v(70.96, -214.6) * mm, v(70.96, -214.7) * mm, v(70.86, -215.15) * mm, v(70.73, -215.61) * mm]});
            skFitSpline(sketch, "E539", {"points": [v(70.73, -215.61) * mm, v(70.6, -216.07) * mm, v(70.4, -216.91) * mm, v(70.24, -217.47) * mm]});
            skFitSpline(sketch, "E540", {"points": [v(111.87, -225.63) * mm, v(111.8, -225.46) * mm, v(111.78, -222.25) * mm, v(111.81, -218.5) * mm]});
            skFitSpline(sketch, "E541", {"points": [v(113.92, -211.4) * mm, v(115.04, -211.24) * mm, v(115.98, -211.13) * mm, v(116, -211.15) * mm]});
            skFitSpline(sketch, "E542", {"points": [v(116, -211.15) * mm, v(116.02, -211.16) * mm, v(116.07, -214.5) * mm, v(116.12, -218.55) * mm]});
            skFitSpline(sketch, "E543", {"points": [v(114.1, -225.93) * mm, v(112.61, -225.93) * mm, v(111.95, -225.84) * mm, v(111.87, -225.63) * mm]});
            skFitSpline(sketch, "E544", {"points": [v(122.59, -225.4) * mm, v(120.89, -220.73) * mm, v(117.97, -211.96) * mm, v(118.08, -211.85) * mm]});
            skFitSpline(sketch, "E545", {"points": [v(118.08, -211.85) * mm, v(118.24, -211.7) * mm, v(122.62, -211.04) * mm, v(122.74, -211.15) * mm]});
            skFitSpline(sketch, "E546", {"points": [v(122.74, -211.15) * mm, v(122.78, -211.19) * mm, v(123.47, -213.34) * mm, v(124.28, -215.94) * mm]});
            skFitSpline(sketch, "E547", {"points": [v(124.28, -215.94) * mm, v(125.1, -218.54) * mm, v(125.84, -220.58) * mm, v(125.93, -220.48) * mm]});
            skFitSpline(sketch, "E548", {"points": [v(125.93, -220.48) * mm, v(126.68, -219.62) * mm, v(128.32, -214.08) * mm, v(128.32, -212.39) * mm]});
            skFitSpline(sketch, "E549", {"points": [v(128.32, -212.39) * mm, v(128.32, -211.73) * mm, v(128.43, -211.68) * mm, v(130.78, -211.33) * mm]});
            skFitSpline(sketch, "E550", {"points": [v(130.78, -211.33) * mm, v(131.53, -211.22) * mm, v(132.2, -211.18) * mm, v(132.28, -211.25) * mm]});
            skFitSpline(sketch, "E551", {"points": [v(132.28, -211.25) * mm, v(132.52, -211.5) * mm, v(132.38, -213.14) * mm, v(131.94, -215.3) * mm]});
            skFitSpline(sketch, "E552", {"points": [v(131.94, -215.3) * mm, v(131.42, -217.8) * mm, v(130.41, -220.29) * mm, v(128.55, -223.64) * mm]});
            skFitSpline(sketch, "E553", {"points": [v(125.03, -225.93) * mm, v(122.92, -225.93) * mm, v(122.77, -225.9) * mm, v(122.59, -225.4) * mm]});
            skFitSpline(sketch, "E554", {"points": [v(151.17, -225.51) * mm, v(151.08, -225.28) * mm, v(151, -220.83) * mm, v(151, -215.61) * mm]});
            skFitSpline(sketch, "E555", {"points": [v(153.28, -205.86) * mm, v(154.53, -205.7) * mm, v(155.64, -205.63) * mm, v(155.74, -205.69) * mm]});
            skFitSpline(sketch, "E556", {"points": [v(155.74, -205.69) * mm, v(155.84, -205.75) * mm, v(155.92, -210.33) * mm, v(155.92, -215.87) * mm]});
            skFitSpline(sketch, "E557", {"points": [v(153.63, -225.93) * mm, v(151.68, -225.93) * mm, v(151.32, -225.87) * mm, v(151.17, -225.51) * mm]});
            skFitSpline(sketch, "E558", {"points": [v(13.21, -209.27) * mm, v(12.18, -208.82) * mm, v(11.82, -207.58) * mm, v(12.4, -206.5) * mm]});
            skFitSpline(sketch, "E559", {"points": [v(12.4, -206.5) * mm, v(12.71, -205.9) * mm, v(14.17, -205.44) * mm, v(15.1, -205.63) * mm]});
            skFitSpline(sketch, "E560", {"points": [v(15.1, -205.63) * mm, v(17.25, -206.06) * mm, v(17.68, -208.67) * mm, v(15.73, -209.35) * mm]});
            skFitSpline(sketch, "E561", {"points": [v(15.73, -209.35) * mm, v(14.75, -209.69) * mm, v(14.13, -209.67) * mm, v(13.21, -209.27) * mm]});
            skFitSpline(sketch, "E562", {"points": [v(112.72, -209.2) * mm, v(111.1, -208.38) * mm, v(111.19, -206.57) * mm, v(112.88, -205.86) * mm]});
            skFitSpline(sketch, "E563", {"points": [v(112.88, -205.86) * mm, v(114.53, -205.17) * mm, v(116.32, -206) * mm, v(116.32, -207.43) * mm]});
            skFitSpline(sketch, "E564", {"points": [v(116.32, -207.43) * mm, v(116.32, -208.46) * mm, v(116.1, -208.87) * mm, v(115.34, -209.26) * mm]});
            skFitSpline(sketch, "E565", {"points": [v(115.34, -209.26) * mm, v(114.45, -209.72) * mm, v(113.74, -209.7) * mm, v(112.72, -209.2) * mm]});
            skFitSpline(sketch, "E566", {"points": [v(-134.72, -209.06) * mm, v(-135.82, -208.5) * mm, v(-136.16, -207) * mm, v(-135.4, -206.08) * mm]});
            skFitSpline(sketch, "E567", {"points": [v(-135.4, -206.08) * mm, v(-135.03, -205.63) * mm, v(-133.45, -205.27) * mm, v(-132.61, -205.44) * mm]});
            skFitSpline(sketch, "E568", {"points": [v(-132.61, -205.44) * mm, v(-131.15, -205.73) * mm, v(-130.44, -207.14) * mm, v(-131.12, -208.4) * mm]});
            skFitSpline(sketch, "E569", {"points": [v(-131.12, -208.4) * mm, v(-131.58, -209.26) * mm, v(-133.6, -209.63) * mm, v(-134.72, -209.06) * mm]});
            skFitSpline(sketch, "E570", {"points": [v(-148.54, -196.01) * mm, v(-149.23, -195.91) * mm, v(-149.3, -195.81) * mm, v(-149.68, -194.2) * mm]});
            skFitSpline(sketch, "E571", {"points": [v(-149.68, -194.2) * mm, v(-149.9, -193.27) * mm, v(-150.06, -192.48) * mm, v(-150.03, -192.45) * mm]});
            skFitSpline(sketch, "E572", {"points": [v(-150.03, -192.45) * mm, v(-150, -192.42) * mm, v(-148.61, -192.5) * mm, v(-146.96, -192.62) * mm]});
            skFitSpline(sketch, "E573", {"points": [v(-146.96, -192.62) * mm, v(-141.65, -193.02) * mm, v(-139.28, -192.5) * mm, v(-139.28, -190.95) * mm]});
            skFitSpline(sketch, "E574", {"points": [v(-139.28, -190.95) * mm, v(-139.28, -190.61) * mm, v(-139.82, -189.17) * mm, v(-140.48, -187.76) * mm]});
            skFitSpline(sketch, "E575", {"points": [v(-140.48, -187.76) * mm, v(-142.52, -183.37) * mm, v(-142.78, -181.35) * mm, v(-141.6, -179.25) * mm]});
            skFitSpline(sketch, "E576", {"points": [v(-141.6, -179.25) * mm, v(-140.6, -177.47) * mm, v(-138.61, -176.57) * mm, v(-133.62, -175.65) * mm]});
            skFitSpline(sketch, "E577", {"points": [v(-133.62, -175.65) * mm, v(-131.84, -175.32) * mm, v(-129.8, -174.99) * mm, v(-129.1, -174.9) * mm]});
            skFitSpline(sketch, "E578", {"points": [v(-127.94, -179.52) * mm, v(-128.08, -185.93) * mm, v(-127.77, -186.8) * mm, v(-125.29, -186.8) * mm]});
            skFitSpline(sketch, "E579", {"points": [v(-125.29, -186.8) * mm, v(-123.19, -186.82) * mm, v(-122.96, -186.2) * mm, v(-122.96, -180.41) * mm]});
            skFitSpline(sketch, "E580", {"points": [v(-122.96, -180.41) * mm, v(-122.96, -176.07) * mm, v(-122.95, -176) * mm, v(-122.42, -175.77) * mm]});
            skFitSpline(sketch, "E581", {"points": [v(-122.42, -175.77) * mm, v(-121.8, -175.51) * mm, v(-118.79, -174.81) * mm, v(-118.27, -174.81) * mm]});
            skFitSpline(sketch, "E582", {"points": [v(-118.27, -174.81) * mm, v(-117.98, -174.81) * mm, v(-117.94, -175.5) * mm, v(-118.05, -179.2) * mm]});
            skFitSpline(sketch, "E583", {"points": [v(-118.05, -179.2) * mm, v(-118.24, -185.53) * mm, v(-118.64, -187.26) * mm, v(-120.24, -188.78) * mm]});
            skFitSpline(sketch, "E584", {"points": [v(-120.24, -188.78) * mm, v(-121.29, -189.77) * mm, v(-122.02, -189.93) * mm, v(-125.44, -189.93) * mm]});
            skFitSpline(sketch, "E585", {"points": [v(-125.44, -189.93) * mm, v(-129.07, -189.93) * mm, v(-130.09, -189.71) * mm, v(-131.25, -188.7) * mm]});
            skFitSpline(sketch, "E586", {"points": [v(-131.25, -188.7) * mm, v(-132.46, -187.63) * mm, v(-132.8, -186.21) * mm, v(-132.8, -182.3) * mm]});
            skFitSpline(sketch, "E587", {"points": [v(-133.81, -179.23) * mm, v(-135.36, -179.48) * mm, v(-136.84, -180.23) * mm, v(-137.16, -180.92) * mm]});
            skFitSpline(sketch, "E588", {"points": [v(-137.16, -180.92) * mm, v(-137.54, -181.75) * mm, v(-137.18, -183.27) * mm, v(-135.88, -186.28) * mm]});
            skFitSpline(sketch, "E589", {"points": [v(-135.88, -186.28) * mm, v(-134.3, -189.95) * mm, v(-134.36, -192.12) * mm, v(-136.07, -194.02) * mm]});
            skFitSpline(sketch, "E590", {"points": [v(-136.07, -194.02) * mm, v(-136.52, -194.51) * mm, v(-137.45, -195.17) * mm, v(-138.14, -195.48) * mm]});
            skFitSpline(sketch, "E591", {"points": [v(-138.14, -195.48) * mm, v(-139.3, -195.99) * mm, v(-139.77, -196.04) * mm, v(-143.6, -196.08) * mm]});
            skFitSpline(sketch, "E592", {"points": [v(-143.6, -196.08) * mm, v(-145.91, -196.1) * mm, v(-148.13, -196.07) * mm, v(-148.54, -196.01) * mm]});
            skFitSpline(sketch, "E593", {"points": [v(-8.67, -195.48) * mm, v(-10.33, -194.9) * mm, v(-11.54, -193.91) * mm, v(-12.5, -192.34) * mm]});
            skFitSpline(sketch, "E594", {"points": [v(-12.5, -192.34) * mm, v(-13.44, -190.76) * mm, v(-13.8, -189.1) * mm, v(-13.71, -186.7) * mm]});
            skFitSpline(sketch, "E595", {"points": [v(-11.84, -184.27) * mm, v(-9.1, -183.4) * mm, v(-9.27, -183.27) * mm, v(-9.17, -186.4) * mm]});
            skFitSpline(sketch, "E596", {"points": [v(-9.17, -186.4) * mm, v(-9.1, -188.68) * mm, v(-8.99, -189.28) * mm, v(-8.48, -190.3) * mm]});
            skFitSpline(sketch, "E597", {"points": [v(-8.48, -190.3) * mm, v(-7.43, -192.4) * mm, v(-5.76, -193.09) * mm, v(-2.96, -192.59) * mm]});
            skFitSpline(sketch, "E598", {"points": [v(-1.2, -190.84) * mm, v(-1.11, -190.04) * mm, v(-1.04, -184.98) * mm, v(-1.04, -179.6) * mm]});
            skFitSpline(sketch, "E599", {"points": [v(-1.04, -179.6) * mm, v(-1.04, -170.48) * mm, v(-1.01, -169.8) * mm, v(-0.62, -169.68) * mm]});
            skFitSpline(sketch, "E600", {"points": [v(-0.62, -169.68) * mm, v(0.4, -169.38) * mm, v(3.76, -168.74) * mm, v(3.82, -168.83) * mm]});
            skFitSpline(sketch, "E601", {"points": [v(3.82, -168.83) * mm, v(3.96, -169.05) * mm, v(3.54, -193.46) * mm, v(3.39, -194.07) * mm]});
            skFitSpline(sketch, "E602", {"points": [v(3.39, -194.07) * mm, v(3.29, -194.48) * mm, v(3.03, -194.78) * mm, v(2.7, -194.84) * mm]});
            skFitSpline(sketch, "E603", {"points": [v(2.7, -194.84) * mm, v(-3.53, -196.05) * mm, v(-6.53, -196.22) * mm, v(-8.67, -195.48) * mm]});
            skFitSpline(sketch, "E604", {"points": [v(61, -195.6) * mm, v(59.4, -195.1) * mm, v(58.58, -194.57) * mm, v(57.54, -193.38) * mm]});
            skFitSpline(sketch, "E605", {"points": [v(57.54, -193.38) * mm, v(56.16, -191.81) * mm, v(55.56, -189.76) * mm, v(55.65, -186.95) * mm]});
            skFitSpline(sketch, "E606", {"points": [v(57.52, -184.27) * mm, v(60.29, -183.39) * mm, v(60.16, -183.3) * mm, v(60.16, -186.05) * mm]});
            skFitSpline(sketch, "E607", {"points": [v(60.16, -186.05) * mm, v(60.16, -188.94) * mm, v(60.59, -190.52) * mm, v(61.65, -191.55) * mm]});
            skFitSpline(sketch, "E608", {"points": [v(61.65, -191.55) * mm, v(62.79, -192.64) * mm, v(64.17, -192.95) * mm, v(66.34, -192.58) * mm]});
            skFitSpline(sketch, "E609", {"points": [v(70.3, -175.32) * mm, v(71.52, -175.04) * mm, v(72.68, -174.8) * mm, v(72.88, -174.81) * mm]});
            skFitSpline(sketch, "E610", {"points": [v(72.88, -174.81) * mm, v(73.2, -174.81) * mm, v(73.23, -175.65) * mm, v(73.18, -181.11) * mm]});
            skFitSpline(sketch, "E611", {"points": [v(73.18, -181.11) * mm, v(73.13, -186.7) * mm, v(72.77, -194.44) * mm, v(72.55, -194.66) * mm]});
            skFitSpline(sketch, "E612", {"points": [v(72.55, -194.66) * mm, v(72.5, -194.7) * mm, v(70.94, -195) * mm, v(69.07, -195.34) * mm]});
            skFitSpline(sketch, "E613", {"points": [v(69.07, -195.34) * mm, v(65.38, -195.98) * mm, v(62.51, -196.08) * mm, v(61, -195.6) * mm]});
            skFitSpline(sketch, "E614", {"points": [v(99.13, -192.81) * mm, v(100.57, -192.81) * mm, v(101.7, -192.15) * mm, v(102.4, -190.9) * mm]});
            skFitSpline(sketch, "E615", {"points": [v(102.4, -190.9) * mm, v(102.99, -189.83) * mm, v(103, -189.72) * mm, v(103.08, -183.53) * mm]});
            skFitSpline(sketch, "E616", {"points": [v(105.27, -176.75) * mm, v(106.43, -176.48) * mm, v(107.5, -176.25) * mm, v(107.65, -176.25) * mm]});
            skFitSpline(sketch, "E617", {"points": [v(107.65, -176.25) * mm, v(107.84, -176.25) * mm, v(107.92, -177.47) * mm, v(107.92, -180.34) * mm]});
            skFitSpline(sketch, "E618", {"points": [v(107.92, -180.34) * mm, v(107.92, -186.27) * mm, v(108.1, -186.57) * mm, v(111.88, -186.57) * mm]});
            skFitSpline(sketch, "E619", {"points": [v(113.26, -185.2) * mm, v(112.21, -182.9) * mm, v(112.46, -179.95) * mm, v(113.86, -178.1) * mm]});
            skFitSpline(sketch, "E620", {"points": [v(113.86, -178.1) * mm, v(114.63, -177.06) * mm, v(116.9, -175.86) * mm, v(118.48, -175.65) * mm]});
            skFitSpline(sketch, "E621", {"points": [v(118.48, -175.65) * mm, v(119.8, -175.47) * mm, v(121.67, -175.86) * mm, v(122.6, -176.52) * mm]});
            skFitSpline(sketch, "E622", {"points": [v(123.52, -176.37) * mm, v(123.65, -176.03) * mm, v(123.76, -175.64) * mm, v(123.76, -175.51) * mm]});
            skFitSpline(sketch, "E623", {"points": [v(123.76, -175.51) * mm, v(123.76, -175.16) * mm, v(124.87, -174.81) * mm, v(126.01, -174.81) * mm]});
            skFitSpline(sketch, "E624", {"points": [v(126.01, -174.81) * mm, v(128.69, -174.81) * mm, v(131.13, -176.37) * mm, v(132.29, -178.8) * mm]});
            skFitSpline(sketch, "E625", {"points": [v(132.29, -178.8) * mm, v(132.74, -179.77) * mm, v(133, -180.92) * mm, v(133.23, -182.87) * mm]});
            skFitSpline(sketch, "E626", {"points": [v(133.23, -182.87) * mm, v(133.4, -184.36) * mm, v(133.62, -185.69) * mm, v(133.7, -185.82) * mm]});
            skFitSpline(sketch, "E627", {"points": [v(133.7, -185.82) * mm, v(134.02, -186.34) * mm, v(135.49, -186.62) * mm, v(136.37, -186.33) * mm]});
            skFitSpline(sketch, "E628", {"points": [v(136.37, -186.33) * mm, v(137.57, -185.93) * mm, v(137.96, -185.18) * mm, v(138.17, -182.87) * mm]});
            skFitSpline(sketch, "E629", {"points": [v(138.17, -182.87) * mm, v(138.55, -178.67) * mm, v(140.5, -176.42) * mm, v(144.36, -175.74) * mm]});
            skFitSpline(sketch, "E630", {"points": [v(144.36, -175.74) * mm, v(149.9, -174.76) * mm, v(153.4, -179.53) * mm, v(152.7, -187.11) * mm]});
            skFitSpline(sketch, "E631", {"points": [v(149.74, -189.58) * mm, v(146.13, -190.42) * mm, v(143.5, -190.35) * mm, v(141.59, -189.38) * mm]});
            skFitSpline(sketch, "E632", {"points": [v(139.43, -189.27) * mm, v(138.67, -189.72) * mm, v(138.09, -189.83) * mm, v(135.88, -189.9) * mm]});
            skFitSpline(sketch, "E633", {"points": [v(135.88, -189.9) * mm, v(133.98, -189.95) * mm, v(132.95, -189.88) * mm, v(132.2, -189.62) * mm]});
            skFitSpline(sketch, "E634", {"points": [v(132.2, -189.62) * mm, v(131.31, -189.3) * mm, v(131.01, -189.3) * mm, v(129.88, -189.6) * mm]});
            skFitSpline(sketch, "E635", {"points": [v(129.88, -189.6) * mm, v(128.83, -189.88) * mm, v(126.51, -189.93) * mm, v(118, -189.88) * mm]});
            skFitSpline(sketch, "E636", {"points": [v(118, -189.88) * mm, v(109.24, -189.82) * mm, v(107.44, -189.87) * mm, v(107.44, -190.14) * mm]});
            skFitSpline(sketch, "E637", {"points": [v(107.44, -190.14) * mm, v(107.44, -190.32) * mm, v(107.11, -191.15) * mm, v(106.71, -191.98) * mm]});
            skFitSpline(sketch, "E638", {"points": [v(106.71, -191.98) * mm, v(105.45, -194.62) * mm, v(103.3, -195.93) * mm, v(100.24, -195.93) * mm]});
            skFitSpline(sketch, "E639", {"points": [v(147.7, -186.44) * mm, v(148.08, -186.32) * mm, v(148.1, -183.13) * mm, v(147.73, -181.63) * mm]});
            skFitSpline(sketch, "E640", {"points": [v(147.73, -181.63) * mm, v(147.39, -180.29) * mm, v(146.35, -179.13) * mm, v(145.49, -179.13) * mm]});
            skFitSpline(sketch, "E641", {"points": [v(145.49, -179.13) * mm, v(144.75, -179.13) * mm, v(143.93, -179.52) * mm, v(143.5, -180.07) * mm]});
            skFitSpline(sketch, "E642", {"points": [v(143.5, -180.07) * mm, v(142.7, -181.14) * mm, v(142.96, -184.46) * mm, v(143.95, -185.71) * mm]});
            skFitSpline(sketch, "E643", {"points": [v(143.95, -185.71) * mm, v(144.66, -186.63) * mm, v(146.15, -186.91) * mm, v(147.7, -186.44) * mm]});
            skFitSpline(sketch, "E644", {"points": [v(121.04, -183.94) * mm, v(120.9, -181.38) * mm, v(120.46, -179.72) * mm, v(119.85, -179.32) * mm]});
            skFitSpline(sketch, "E645", {"points": [v(119.85, -179.32) * mm, v(119.33, -179) * mm, v(118.56, -179.12) * mm, v(117.91, -179.63) * mm]});
            skFitSpline(sketch, "E646", {"points": [v(117.91, -179.63) * mm, v(116.45, -180.78) * mm, v(117.49, -184.52) * mm, v(119.64, -185.88) * mm]});
            skFitSpline(sketch, "E647", {"points": [v(119.64, -185.88) * mm, v(120.24, -186.26) * mm, v(120.84, -186.57) * mm, v(120.96, -186.57) * mm]});
            skFitSpline(sketch, "E648", {"points": [v(120.96, -186.57) * mm, v(121.1, -186.57) * mm, v(121.13, -185.56) * mm, v(121.04, -183.94) * mm]});
            skFitSpline(sketch, "E649", {"points": [v(128.28, -183.87) * mm, v(128.2, -181.65) * mm, v(128.1, -180.97) * mm, v(127.63, -180.03) * mm]});
            skFitSpline(sketch, "E650", {"points": [v(127.63, -180.03) * mm, v(127.04, -178.81) * mm, v(126.15, -178.17) * mm, v(125.06, -178.17) * mm]});
            skFitSpline(sketch, "E651", {"points": [v(125.06, -178.17) * mm, v(124.55, -178.17) * mm, v(124.46, -178.25) * mm, v(124.6, -178.6) * mm]});
            skFitSpline(sketch, "E652", {"points": [v(124.6, -178.6) * mm, v(125.4, -180.43) * mm, v(125.74, -181.92) * mm, v(125.86, -184.11) * mm]});
            skFitSpline(sketch, "E653", {"points": [v(-75.92, -195.54) * mm, v(-77.37, -194.96) * mm, v(-77.78, -193.45) * mm, v(-76.77, -192.44) * mm]});
            skFitSpline(sketch, "E654", {"points": [v(-76.77, -192.44) * mm, v(-76.29, -191.96) * mm, v(-75.95, -191.85) * mm, v(-74.84, -191.85) * mm]});
            skFitSpline(sketch, "E655", {"points": [v(-74.84, -191.85) * mm, v(-73.74, -191.85) * mm, v(-73.4, -191.96) * mm, v(-72.91, -192.44) * mm]});
            skFitSpline(sketch, "E656", {"points": [v(-72.91, -192.44) * mm, v(-71.65, -193.7) * mm, v(-72.54, -195.43) * mm, v(-74.53, -195.6) * mm]});
            skFitSpline(sketch, "E657", {"points": [v(-74.53, -195.6) * mm, v(-75.1, -195.64) * mm, v(-75.72, -195.62) * mm, v(-75.92, -195.54) * mm]});
            skFitSpline(sketch, "E658", {"points": [v(-70.34, -195.33) * mm, v(-71.8, -194.7) * mm, v(-71.88, -192.76) * mm, v(-70.5, -192.12) * mm]});
            skFitSpline(sketch, "E659", {"points": [v(-70.5, -192.12) * mm, v(-69.51, -191.68) * mm, v(-67.69, -191.78) * mm, v(-67.1, -192.32) * mm]});
            skFitSpline(sketch, "E660", {"points": [v(-67.1, -192.32) * mm, v(-66, -193.35) * mm, v(-66.25, -194.77) * mm, v(-67.63, -195.34) * mm]});
            skFitSpline(sketch, "E661", {"points": [v(-67.63, -195.34) * mm, v(-68.66, -195.77) * mm, v(-69.33, -195.77) * mm, v(-70.34, -195.33) * mm]});
            skFitSpline(sketch, "E662", {"points": [v(12.51, -195.22) * mm, v(10.4, -194.37) * mm, v(11.36, -191.85) * mm, v(13.8, -191.85) * mm]});
            skFitSpline(sketch, "E663", {"points": [v(13.8, -191.85) * mm, v(15.64, -191.85) * mm, v(16.77, -192.97) * mm, v(16.24, -194.26) * mm]});
            skFitSpline(sketch, "E664", {"points": [v(16.24, -194.26) * mm, v(15.81, -195.28) * mm, v(13.88, -195.78) * mm, v(12.51, -195.22) * mm]});
            skFitSpline(sketch, "E665", {"points": [v(17.92, -195.05) * mm, v(16.8, -194.47) * mm, v(16.64, -193.35) * mm, v(17.53, -192.46) * mm]});
            skFitSpline(sketch, "E666", {"points": [v(17.53, -192.46) * mm, v(18.34, -191.65) * mm, v(20.4, -191.6) * mm, v(21.37, -192.35) * mm]});
            skFitSpline(sketch, "E667", {"points": [v(21.37, -192.35) * mm, v(22.14, -192.96) * mm, v(22.23, -194.2) * mm, v(21.55, -194.82) * mm]});
            skFitSpline(sketch, "E668", {"points": [v(21.55, -194.82) * mm, v(20.86, -195.45) * mm, v(18.93, -195.57) * mm, v(17.92, -195.05) * mm]});
            skFitSpline(sketch, "E669", {"points": [v(27.3, -195.26) * mm, v(26.98, -195.16) * mm, v(26.5, -194.8) * mm, v(26.24, -194.44) * mm]});
            skFitSpline(sketch, "E670", {"points": [v(26.24, -194.44) * mm, v(25.83, -193.89) * mm, v(25.8, -193.7) * mm, v(26.06, -193.1) * mm]});
            skFitSpline(sketch, "E671", {"points": [v(26.06, -193.1) * mm, v(26.42, -192.24) * mm, v(27.2, -191.85) * mm, v(28.6, -191.85) * mm]});
            skFitSpline(sketch, "E672", {"points": [v(28.6, -191.85) * mm, v(30.48, -191.85) * mm, v(31.6, -193.42) * mm, v(30.58, -194.61) * mm]});
            skFitSpline(sketch, "E673", {"points": [v(30.58, -194.61) * mm, v(29.98, -195.3) * mm, v(28.46, -195.6) * mm, v(27.3, -195.26) * mm]});
            skFitSpline(sketch, "E674", {"points": [v(87.04, -195.03) * mm, v(85.92, -194.47) * mm, v(85.76, -193.35) * mm, v(86.65, -192.46) * mm]});
            skFitSpline(sketch, "E675", {"points": [v(86.65, -192.46) * mm, v(87.15, -191.96) * mm, v(87.48, -191.85) * mm, v(88.6, -191.85) * mm]});
            skFitSpline(sketch, "E676", {"points": [v(88.6, -191.85) * mm, v(89.7, -191.85) * mm, v(90.04, -191.96) * mm, v(90.53, -192.44) * mm]});
            skFitSpline(sketch, "E677", {"points": [v(90.53, -192.44) * mm, v(91.52, -193.43) * mm, v(91.22, -194.72) * mm, v(89.89, -195.19) * mm]});
            skFitSpline(sketch, "E678", {"points": [v(89.89, -195.19) * mm, v(88.82, -195.56) * mm, v(88, -195.52) * mm, v(87.04, -195.03) * mm]});
            skFitSpline(sketch, "E679", {"points": [v(-151.85, -190.87) * mm, v(-152.26, -190.55) * mm, v(-152.48, -190.14) * mm, v(-152.48, -189.72) * mm]});
            skFitSpline(sketch, "E680", {"points": [v(-152.48, -189.72) * mm, v(-152.48, -187.35) * mm, v(-147.73, -187.26) * mm, v(-147.49, -189.63) * mm]});
            skFitSpline(sketch, "E681", {"points": [v(-147.49, -189.63) * mm, v(-147.43, -190.18) * mm, v(-147.57, -190.48) * mm, v(-148.06, -190.86) * mm]});
            skFitSpline(sketch, "E682", {"points": [v(-148.06, -190.86) * mm, v(-148.95, -191.57) * mm, v(-150.96, -191.57) * mm, v(-151.85, -190.87) * mm]});
            skFitSpline(sketch, "E683", {"points": [v(-146.04, -190.65) * mm, v(-146.83, -189.86) * mm, v(-146.81, -189.18) * mm, v(-145.99, -188.46) * mm]});
            skFitSpline(sketch, "E684", {"points": [v(-145.99, -188.46) * mm, v(-144.3, -187) * mm, v(-140.77, -188.46) * mm, v(-141.7, -190.23) * mm]});
            skFitSpline(sketch, "E685", {"points": [v(-141.7, -190.23) * mm, v(-142.18, -191.11) * mm, v(-142.69, -191.36) * mm, v(-144.04, -191.36) * mm]});
            skFitSpline(sketch, "E686", {"points": [v(-144.04, -191.36) * mm, v(-145.15, -191.37) * mm, v(-145.42, -191.27) * mm, v(-146.04, -190.65) * mm]});
            skFitSpline(sketch, "E687", {"points": [v(7.08, -180.27) * mm, v(7.13, -174.56) * mm, v(7.2, -169.85) * mm, v(7.25, -169.8) * mm]});
            skFitSpline(sketch, "E688", {"points": [v(7.25, -169.8) * mm, v(7.38, -169.66) * mm, v(11.03, -168.83) * mm, v(11.56, -168.82) * mm]});
            skFitSpline(sketch, "E689", {"points": [v(11.56, -168.82) * mm, v(12.03, -168.81) * mm, v(12.04, -168.94) * mm, v(11.96, -176.71) * mm]});
            skFitSpline(sketch, "E690", {"points": [v(11.96, -176.71) * mm, v(11.88, -185.35) * mm, v(11.94, -185.84) * mm, v(13.27, -186.34) * mm]});
            skFitSpline(sketch, "E691", {"points": [v(13.27, -186.34) * mm, v(14.22, -186.7) * mm, v(15.65, -186.61) * mm, v(16.22, -186.15) * mm]});
            skFitSpline(sketch, "E692", {"points": [v(16.22, -186.15) * mm, v(16.88, -185.62) * mm, v(17.19, -183.63) * mm, v(17.2, -179.92) * mm]});
            skFitSpline(sketch, "E693", {"points": [v(17.2, -179.92) * mm, v(17.2, -177.32) * mm, v(17.22, -177.22) * mm, v(17.74, -177.1) * mm]});
            skFitSpline(sketch, "E694", {"points": [v(17.74, -177.1) * mm, v(20.78, -176.4) * mm, v(21.62, -176.25) * mm, v(21.78, -176.42) * mm]});
            skFitSpline(sketch, "E695", {"points": [v(21.78, -176.42) * mm, v(21.88, -176.53) * mm, v(22, -178.58) * mm, v(22.04, -180.99) * mm]});
            skFitSpline(sketch, "E696", {"points": [v(22.04, -180.99) * mm, v(22.14, -186.84) * mm, v(21.72, -186.43) * mm, v(27.76, -186.53) * mm]});
            skFitSpline(sketch, "E697", {"points": [v(31.34, -183.89) * mm, v(30.13, -180.46) * mm, v(29.49, -179.2) * mm, v(28.66, -178.57) * mm]});
            skFitSpline(sketch, "E698", {"points": [v(28.66, -178.57) * mm, v(28.07, -178.13) * mm, v(27.86, -178.1) * mm, v(26.79, -178.33) * mm]});
            skFitSpline(sketch, "E699", {"points": [v(26.79, -178.33) * mm, v(26.12, -178.46) * mm, v(25.54, -178.5) * mm, v(25.48, -178.42) * mm]});
            skFitSpline(sketch, "E700", {"points": [v(25.48, -178.42) * mm, v(25.43, -178.34) * mm, v(25.56, -177.59) * mm, v(25.77, -176.76) * mm]});
            skFitSpline(sketch, "E701", {"points": [v(25.77, -176.76) * mm, v(26.22, -174.95) * mm, v(26.63, -174.71) * mm, v(28.96, -174.87) * mm]});
            skFitSpline(sketch, "E702", {"points": [v(28.96, -174.87) * mm, v(30.83, -175) * mm, v(32.15, -175.62) * mm, v(33.34, -176.94) * mm]});
            skFitSpline(sketch, "E703", {"points": [v(33.34, -176.94) * mm, v(34.46, -178.18) * mm, v(34.7, -178.68) * mm, v(35.78, -181.94) * mm]});
            skFitSpline(sketch, "E704", {"points": [v(35.78, -181.94) * mm, v(36.9, -185.32) * mm, v(37.43, -186.14) * mm, v(38.69, -186.44) * mm]});
            skFitSpline(sketch, "E705", {"points": [v(38.69, -186.44) * mm, v(39.2, -186.56) * mm, v(39.67, -186.68) * mm, v(39.71, -186.71) * mm]});
            skFitSpline(sketch, "E706", {"points": [v(39.71, -186.71) * mm, v(39.76, -186.74) * mm, v(39.69, -187.18) * mm, v(39.56, -187.69) * mm]});
            skFitSpline(sketch, "E707", {"points": [v(39.56, -187.69) * mm, v(39.43, -188.2) * mm, v(39.26, -188.91) * mm, v(39.18, -189.28) * mm]});
            skFitSpline(sketch, "E708", {"points": [v(30.21, -189.88) * mm, v(21.45, -189.81) * mm, v(21.4, -189.8) * mm, v(20.62, -189.26) * mm]});
            skFitSpline(sketch, "E709", {"points": [v(19.1, -189.26) * mm, v(18.42, -189.77) * mm, v(18.08, -189.82) * mm, v(14.74, -189.9) * mm]});
            skFitSpline(sketch, "E710", {"points": [v(14.74, -189.9) * mm, v(11.81, -189.95) * mm, v(10.92, -189.9) * mm, v(10.08, -189.57) * mm]});
            skFitSpline(sketch, "E711", {"points": [v(8.15, -189.91) * mm, v(7.65, -190.32) * mm, v(7.2, -190.65) * mm, v(7.12, -190.65) * mm]});
            skFitSpline(sketch, "E712", {"points": [v(7.12, -190.65) * mm, v(7.05, -190.65) * mm, v(7.03, -185.98) * mm, v(7.08, -180.27) * mm]});
            skFitSpline(sketch, "E713", {"points": [v(-58.46, -190.12) * mm, v(-59.22, -190.03) * mm, v(-60.12, -189.8) * mm, v(-60.47, -189.62) * mm]});
            skFitSpline(sketch, "E714", {"points": [v(-60.47, -189.62) * mm, v(-61, -189.34) * mm, v(-61.25, -189.34) * mm, v(-61.97, -189.6) * mm]});
            skFitSpline(sketch, "E715", {"points": [v(-61.97, -189.6) * mm, v(-62.52, -189.8) * mm, v(-64.1, -189.92) * mm, v(-66.27, -189.92) * mm]});
            skFitSpline(sketch, "E716", {"points": [v(-66.27, -189.92) * mm, v(-69.25, -189.93) * mm, v(-69.83, -189.87) * mm, v(-70.65, -189.45) * mm]});
            skFitSpline(sketch, "E717", {"points": [v(-70.65, -189.45) * mm, v(-71.57, -188.98) * mm, v(-71.63, -188.98) * mm, v(-72.25, -189.39) * mm]});
            skFitSpline(sketch, "E718", {"points": [v(-72.25, -189.39) * mm, v(-72.78, -189.73) * mm, v(-73.55, -189.83) * mm, v(-76.3, -189.9) * mm]});
            skFitSpline(sketch, "E719", {"points": [v(-76.3, -189.9) * mm, v(-79.34, -189.97) * mm, v(-79.8, -189.93) * mm, v(-80.66, -189.48) * mm]});
            skFitSpline(sketch, "E720", {"points": [v(-80.66, -189.48) * mm, v(-81.62, -189) * mm, v(-81.62, -189) * mm, v(-82.54, -189.46) * mm]});
            skFitSpline(sketch, "E721", {"points": [v(-82.54, -189.46) * mm, v(-83.33, -189.87) * mm, v(-83.96, -189.93) * mm, v(-86.98, -189.93) * mm]});
            skFitSpline(sketch, "E722", {"points": [v(-86.98, -189.93) * mm, v(-89.38, -189.93) * mm, v(-90.8, -189.83) * mm, v(-91.45, -189.6) * mm]});
            skFitSpline(sketch, "E723", {"points": [v(-91.45, -189.6) * mm, v(-92.31, -189.3) * mm, v(-92.54, -189.3) * mm, v(-93.82, -189.74) * mm]});
            skFitSpline(sketch, "E724", {"points": [v(-93.82, -189.74) * mm, v(-95.7, -190.38) * mm, v(-99.2, -190.25) * mm, v(-100.98, -189.47) * mm]});
            skFitSpline(sketch, "E725", {"points": [v(-100.98, -189.47) * mm, v(-102.13, -188.97) * mm, v(-102.18, -188.97) * mm, v(-103.02, -189.38) * mm]});
            skFitSpline(sketch, "E726", {"points": [v(-103.02, -189.38) * mm, v(-103.74, -189.74) * mm, v(-104.52, -189.81) * mm, v(-107.73, -189.81) * mm]});
            skFitSpline(sketch, "E727", {"points": [v(-107.73, -189.81) * mm, v(-112.08, -189.81) * mm, v(-113.08, -189.55) * mm, v(-114.01, -188.18) * mm]});
            skFitSpline(sketch, "E728", {"points": [v(-114.01, -188.18) * mm, v(-114.9, -186.87) * mm, v(-115.03, -185.57) * mm, v(-115.04, -177.66) * mm]});
            skFitSpline(sketch, "E729", {"points": [v(-113.01, -169.56) * mm, v(-109.77, -168.75) * mm, v(-110.1, -167.95) * mm, v(-110.2, -176.26) * mm]});
            skFitSpline(sketch, "E730", {"points": [v(-110.2, -176.26) * mm, v(-110.3, -183.97) * mm, v(-110.21, -185.3) * mm, v(-109.56, -186.1) * mm]});
            skFitSpline(sketch, "E731", {"points": [v(-109.56, -186.1) * mm, v(-108.98, -186.82) * mm, v(-107.23, -187) * mm, v(-106.1, -186.47) * mm]});
            skFitSpline(sketch, "E732", {"points": [v(-106.1, -186.47) * mm, v(-105.11, -186) * mm, v(-104.72, -185.25) * mm, v(-104.72, -183.81) * mm]});
            skFitSpline(sketch, "E733", {"points": [v(-104.72, -183.81) * mm, v(-104.72, -181.26) * mm, v(-103.9, -179.1) * mm, v(-102.4, -177.64) * mm]});
            skFitSpline(sketch, "E734", {"points": [v(-102.4, -177.64) * mm, v(-99.69, -175.03) * mm, v(-95.35, -174.9) * mm, v(-92.72, -177.36) * mm]});
            skFitSpline(sketch, "E735", {"points": [v(-92.72, -177.36) * mm, v(-91.31, -178.68) * mm, v(-90.68, -180.09) * mm, v(-90.21, -182.98) * mm]});
            skFitSpline(sketch, "E736", {"points": [v(-90.21, -182.98) * mm, v(-89.69, -186.22) * mm, v(-89.15, -186.81) * mm, v(-86.72, -186.81) * mm]});
            skFitSpline(sketch, "E737", {"points": [v(-86.72, -186.81) * mm, v(-84.67, -186.81) * mm, v(-84.32, -185.94) * mm, v(-84.32, -180.76) * mm]});
            skFitSpline(sketch, "E738", {"points": [v(-83.66, -177.07) * mm, v(-83.3, -176.99) * mm, v(-82.4, -176.77) * mm, v(-81.65, -176.59) * mm]});
            skFitSpline(sketch, "E739", {"points": [v(-81.65, -176.59) * mm, v(-79.37, -176.03) * mm, v(-79.56, -175.65) * mm, v(-79.48, -180.93) * mm]});
            skFitSpline(sketch, "E740", {"points": [v(-79.48, -180.93) * mm, v(-79.4, -185.38) * mm, v(-79.38, -185.63) * mm, v(-78.87, -186.13) * mm]});
            skFitSpline(sketch, "E741", {"points": [v(-78.87, -186.13) * mm, v(-78.48, -186.52) * mm, v(-77.97, -186.69) * mm, v(-76.95, -186.76) * mm]});
            skFitSpline(sketch, "E742", {"points": [v(-76.95, -186.76) * mm, v(-75.75, -186.85) * mm, v(-75.5, -186.79) * mm, v(-75.08, -186.33) * mm]});
            skFitSpline(sketch, "E743", {"points": [v(-75.08, -186.33) * mm, v(-74.65, -185.85) * mm, v(-74.6, -185.4) * mm, v(-74.53, -181.62) * mm]});
            skFitSpline(sketch, "E744", {"points": [v(-74.53, -181.62) * mm, v(-74.45, -177.57) * mm, v(-74.43, -177.42) * mm, v(-73.93, -177.2) * mm]});
            skFitSpline(sketch, "E745", {"points": [v(-73.93, -177.2) * mm, v(-73.33, -176.95) * mm, v(-70.3, -176.25) * mm, v(-69.8, -176.25) * mm]});
            skFitSpline(sketch, "E746", {"points": [v(-69.8, -176.25) * mm, v(-69.54, -176.25) * mm, v(-69.46, -177.18) * mm, v(-69.4, -180.93) * mm]});
            skFitSpline(sketch, "E747", {"points": [v(-69.4, -180.93) * mm, v(-69.33, -185.39) * mm, v(-69.3, -185.62) * mm, v(-68.79, -186.13) * mm]});
            skFitSpline(sketch, "E748", {"points": [v(-68.79, -186.13) * mm, v(-68.37, -186.55) * mm, v(-67.9, -186.7) * mm, v(-66.72, -186.77) * mm]});
            skFitSpline(sketch, "E749", {"points": [v(-66.72, -186.77) * mm, v(-65.85, -186.82) * mm, v(-64.97, -186.75) * mm, v(-64.68, -186.6) * mm]});
            skFitSpline(sketch, "E750", {"points": [v(-64.68, -186.6) * mm, v(-63.95, -186.2) * mm, v(-63.68, -184.9) * mm, v(-63.68, -181.6) * mm]});
            skFitSpline(sketch, "E751", {"points": [v(-63.68, -181.6) * mm, v(-63.68, -179.03) * mm, v(-63.63, -178.67) * mm, v(-63.26, -178.56) * mm]});
            skFitSpline(sketch, "E752", {"points": [v(-63.26, -178.56) * mm, v(-62.4, -178.3) * mm, v(-59.56, -177.7) * mm, v(-59.23, -177.7) * mm]});
            skFitSpline(sketch, "E753", {"points": [v(-59.23, -177.7) * mm, v(-58.95, -177.7) * mm, v(-58.88, -178.2) * mm, v(-58.88, -180.4) * mm]});
            skFitSpline(sketch, "E754", {"points": [v(-58.88, -180.4) * mm, v(-58.88, -181.88) * mm, v(-59, -183.8) * mm, v(-59.14, -184.65) * mm]});
            skFitSpline(sketch, "E755", {"points": [v(-59.14, -184.65) * mm, v(-59.42, -186.41) * mm, v(-59.26, -186.67) * mm, v(-57.72, -186.96) * mm]});
            skFitSpline(sketch, "E756", {"points": [v(-57.72, -186.96) * mm, v(-56.56, -187.18) * mm, v(-55.75, -186.83) * mm, v(-55.18, -185.86) * mm]});
            skFitSpline(sketch, "E757", {"points": [v(-55.18, -185.86) * mm, v(-54.76, -185.14) * mm, v(-54.68, -184.5) * mm, v(-54.6, -181.12) * mm]});
            skFitSpline(sketch, "E758", {"points": [v(-53.63, -177) * mm, v(-51.2, -176.39) * mm, v(-50.24, -176.23) * mm, v(-49.98, -176.39) * mm]});
            skFitSpline(sketch, "E759", {"points": [v(-49.98, -176.39) * mm, v(-49.63, -176.6) * mm, v(-49.84, -183.7) * mm, v(-50.24, -185.35) * mm]});
            skFitSpline(sketch, "E760", {"points": [v(-50.24, -185.35) * mm, v(-50.54, -186.55) * mm, v(-50.43, -186.7) * mm, v(-49.07, -186.96) * mm]});
            skFitSpline(sketch, "E761", {"points": [v(-49.07, -186.96) * mm, v(-48, -187.17) * mm, v(-47.17, -186.85) * mm, v(-46.55, -186.02) * mm]});
            skFitSpline(sketch, "E762", {"points": [v(-46.55, -186.02) * mm, v(-46.08, -185.4) * mm, v(-46.04, -184.97) * mm, v(-45.96, -180.55) * mm]});
            skFitSpline(sketch, "E763", {"points": [v(-45.24, -175.63) * mm, v(-44.89, -175.55) * mm, v(-44, -175.33) * mm, v(-43.25, -175.15) * mm]});
            skFitSpline(sketch, "E764", {"points": [v(-43.25, -175.15) * mm, v(-40.8, -174.54) * mm, v(-41, -174.06) * mm, v(-41, -180.2) * mm]});
            skFitSpline(sketch, "E765", {"points": [v(-41, -180.2) * mm, v(-41, -185.37) * mm, v(-40.98, -185.62) * mm, v(-40.5, -186.1) * mm]});
            skFitSpline(sketch, "E766", {"points": [v(-40.5, -186.1) * mm, v(-39.96, -186.64) * mm, v(-38.4, -186.96) * mm, v(-37.46, -186.73) * mm]});
            skFitSpline(sketch, "E767", {"points": [v(-37.46, -186.73) * mm, v(-36.32, -186.44) * mm, v(-36.23, -185.82) * mm, v(-36.13, -177.63) * mm]});
            skFitSpline(sketch, "E768", {"points": [v(-36.13, -177.63) * mm, v(-36.04, -170.05) * mm, v(-36.04, -170.01) * mm, v(-35.52, -169.9) * mm]});
            skFitSpline(sketch, "E769", {"points": [v(-35.52, -169.9) * mm, v(-32.46, -169.19) * mm, v(-31.8, -169.06) * mm, v(-31.33, -169.06) * mm]});
            skFitSpline(sketch, "E770", {"points": [v(-31.33, -169.06) * mm, v(-30.94, -169.05) * mm, v(-30.83, -169.14) * mm, v(-30.96, -169.35) * mm]});
            skFitSpline(sketch, "E771", {"points": [v(-30.96, -169.35) * mm, v(-31.07, -169.52) * mm, v(-31.22, -173.1) * mm, v(-31.3, -177.33) * mm]});
            skFitSpline(sketch, "E772", {"points": [v(-31.3, -177.33) * mm, v(-31.46, -185.85) * mm, v(-31.61, -186.8) * mm, v(-33.03, -188.41) * mm]});
            skFitSpline(sketch, "E773", {"points": [v(-33.03, -188.41) * mm, v(-34.18, -189.72) * mm, v(-34.92, -189.93) * mm, v(-38.36, -189.93) * mm]});
            skFitSpline(sketch, "E774", {"points": [v(-38.36, -189.93) * mm, v(-40.92, -189.93) * mm, v(-41.53, -189.86) * mm, v(-42.33, -189.45) * mm]});
            skFitSpline(sketch, "E775", {"points": [v(-42.33, -189.45) * mm, v(-43.19, -189.01) * mm, v(-43.35, -189) * mm, v(-43.94, -189.3) * mm]});
            skFitSpline(sketch, "E776", {"points": [v(-43.94, -189.3) * mm, v(-45.83, -190.28) * mm, v(-49.12, -190.5) * mm, v(-51.24, -189.8) * mm]});
            skFitSpline(sketch, "E777", {"points": [v(-51.24, -189.8) * mm, v(-52.3, -189.45) * mm, v(-52.6, -189.43) * mm, v(-53.34, -189.7) * mm]});
            skFitSpline(sketch, "E778", {"points": [v(-53.34, -189.7) * mm, v(-54.56, -190.14) * mm, v(-56.85, -190.33) * mm, v(-58.46, -190.12) * mm]});
            skFitSpline(sketch, "E779", {"points": [v(-95.28, -186.8) * mm, v(-94.5, -186.58) * mm, v(-94.38, -186.46) * mm, v(-94.48, -186.02) * mm]});
            skFitSpline(sketch, "E780", {"points": [v(-94.48, -186.02) * mm, v(-94.55, -185.73) * mm, v(-94.73, -184.63) * mm, v(-94.88, -183.57) * mm]});
            skFitSpline(sketch, "E781", {"points": [v(-94.88, -183.57) * mm, v(-95.2, -181.35) * mm, v(-95.83, -179.76) * mm, v(-96.52, -179.4) * mm]});
            skFitSpline(sketch, "E782", {"points": [v(-96.52, -179.4) * mm, v(-97.58, -178.83) * mm, v(-98.8, -179.3) * mm, v(-99.41, -180.5) * mm]});
            skFitSpline(sketch, "E783", {"points": [v(-99.41, -180.5) * mm, v(-99.79, -181.23) * mm, v(-99.75, -184.03) * mm, v(-99.35, -184.96) * mm]});
            skFitSpline(sketch, "E784", {"points": [v(-99.35, -184.96) * mm, v(-98.96, -185.9) * mm, v(-98.28, -186.53) * mm, v(-97.37, -186.8) * mm]});
            skFitSpline(sketch, "E785", {"points": [v(-97.37, -186.8) * mm, v(-96.43, -187.09) * mm, v(-96.33, -187.09) * mm, v(-95.28, -186.8) * mm]});
            skFitSpline(sketch, "E786", {"points": [v(-27.62, -170.01) * mm, v(-26.97, -169.73) * mm, v(-23.97, -169.05) * mm, v(-23.4, -169.05) * mm]});
            skFitSpline(sketch, "E787", {"points": [v(-23.4, -169.05) * mm, v(-23.03, -169.05) * mm, v(-23, -169.78) * mm, v(-23.06, -178.71) * mm]});
            skFitSpline(sketch, "E788", {"points": [v(-23.06, -178.71) * mm, v(-23.1, -184.03) * mm, v(-23.18, -188.72) * mm, v(-23.25, -189.15) * mm]});
            skFitSpline(sketch, "E789", {"points": [v(41.39, -179.92) * mm, v(41.43, -174.42) * mm, v(41.5, -169.87) * mm, v(41.56, -169.81) * mm]});
            skFitSpline(sketch, "E790", {"points": [v(41.56, -169.81) * mm, v(41.7, -169.66) * mm, v(45.33, -168.83) * mm, v(45.88, -168.82) * mm]});
            skFitSpline(sketch, "E791", {"points": [v(45.88, -168.82) * mm, v(46.35, -168.81) * mm, v(46.36, -168.95) * mm, v(46.3, -178.11) * mm]});
            skFitSpline(sketch, "E792", {"points": [v(46.3, -178.11) * mm, v(46.27, -183.23) * mm, v(46.18, -187.98) * mm, v(46.1, -188.67) * mm]});
            skFitSpline(sketch, "E793", {"points": [v(79.4, -189.63) * mm, v(78.12, -189.22) * mm, v(77.06, -188.05) * mm, v(76.62, -186.58) * mm]});
            skFitSpline(sketch, "E794", {"points": [v(76.62, -186.58) * mm, v(76.3, -185.5) * mm, v(76.24, -183.96) * mm, v(76.24, -177.53) * mm]});
            skFitSpline(sketch, "E795", {"points": [v(76.78, -169.66) * mm, v(79.76, -168.97) * mm, v(80.5, -168.82) * mm, v(80.92, -168.82) * mm]});
            skFitSpline(sketch, "E796", {"points": [v(80.92, -168.82) * mm, v(81.4, -168.81) * mm, v(81.4, -168.95) * mm, v(81.32, -176.55) * mm]});
            skFitSpline(sketch, "E797", {"points": [v(81.32, -176.55) * mm, v(81.24, -185.23) * mm, v(81.32, -185.9) * mm, v(82.52, -186.3) * mm]});
            skFitSpline(sketch, "E798", {"points": [v(82.52, -186.3) * mm, v(82.96, -186.46) * mm, v(85.17, -186.57) * mm, v(87.92, -186.57) * mm]});
            skFitSpline(sketch, "E799", {"points": [v(87.92, -186.57) * mm, v(92.27, -186.57) * mm, v(92.55, -186.55) * mm, v(92.32, -186.15) * mm]});
            skFitSpline(sketch, "E800", {"points": [v(92.32, -186.15) * mm, v(92.18, -185.92) * mm, v(91.69, -184.6) * mm, v(91.22, -183.21) * mm]});
            skFitSpline(sketch, "E801", {"points": [v(91.22, -183.21) * mm, v(89.72, -178.8) * mm, v(88.83, -177.84) * mm, v(86.75, -178.37) * mm]});
            skFitSpline(sketch, "E802", {"points": [v(86.75, -178.37) * mm, v(86.2, -178.5) * mm, v(85.67, -178.58) * mm, v(85.58, -178.52) * mm]});
            skFitSpline(sketch, "E803", {"points": [v(85.58, -178.52) * mm, v(85.49, -178.46) * mm, v(85.6, -177.69) * mm, v(85.84, -176.8) * mm]});
            skFitSpline(sketch, "E804", {"points": [v(85.84, -176.8) * mm, v(86.3, -174.99) * mm, v(86.46, -174.88) * mm, v(88.63, -174.84) * mm]});
            skFitSpline(sketch, "E805", {"points": [v(88.63, -174.84) * mm, v(91.88, -174.77) * mm, v(94.26, -176.78) * mm, v(95.44, -180.57) * mm]});
            skFitSpline(sketch, "E806", {"points": [v(95.44, -180.57) * mm, v(96.86, -185.12) * mm, v(97.79, -186.57) * mm, v(99.26, -186.57) * mm]});
            skFitSpline(sketch, "E807", {"points": [v(89.68, -189.9) * mm, v(83.64, -189.9) * mm, v(79.9, -189.79) * mm, v(79.4, -189.63) * mm]});
            skFitSpline(sketch, "E808", {"points": [v(62.13, -180.08) * mm, v(61.37, -179.78) * mm, v(61.03, -178.78) * mm, v(61.42, -177.97) * mm]});
            skFitSpline(sketch, "E809", {"points": [v(61.42, -177.97) * mm, v(62.04, -176.68) * mm, v(64.83, -176.37) * mm, v(65.93, -177.47) * mm]});
            skFitSpline(sketch, "E810", {"points": [v(65.93, -177.47) * mm, v(66.61, -178.14) * mm, v(66.53, -179.23) * mm, v(65.77, -179.83) * mm]});
            skFitSpline(sketch, "E811", {"points": [v(65.77, -179.83) * mm, v(65.08, -180.37) * mm, v(63.18, -180.5) * mm, v(62.13, -180.08) * mm]});
            skFitSpline(sketch, "E812", {"points": [v(-83.52, -174.68) * mm, v(-85.46, -173.69) * mm, v(-84.32, -171.45) * mm, v(-81.88, -171.45) * mm]});
            skFitSpline(sketch, "E813", {"points": [v(-81.88, -171.45) * mm, v(-79.93, -171.45) * mm, v(-78.77, -173) * mm, v(-79.81, -174.2) * mm]});
            skFitSpline(sketch, "E814", {"points": [v(-79.81, -174.2) * mm, v(-80.53, -175.02) * mm, v(-82.39, -175.26) * mm, v(-83.52, -174.68) * mm]});
            skFitSpline(sketch, "E815", {"points": [v(-124, -173.93) * mm, v(-124.06, -173.82) * mm, v(-124.06, -173.43) * mm, v(-124, -173.07) * mm]});
            skFitSpline(sketch, "E816", {"points": [v(-124, -173.07) * mm, v(-123.9, -172.58) * mm, v(-123.72, -172.41) * mm, v(-123.32, -172.41) * mm]});
            skFitSpline(sketch, "E817", {"points": [v(-123.32, -172.41) * mm, v(-122.83, -172.41) * mm, v(-122.79, -172.32) * mm, v(-122.88, -171.4) * mm]});
            skFitSpline(sketch, "E818", {"points": [v(-122.88, -171.4) * mm, v(-123.09, -169.4) * mm, v(-121.39, -167.9) * mm, v(-119.18, -168.16) * mm]});
            skFitSpline(sketch, "E819", {"points": [v(-119.18, -168.16) * mm, v(-117.9, -168.3) * mm, v(-117.84, -168.36) * mm, v(-118.03, -169.26) * mm]});
            skFitSpline(sketch, "E820", {"points": [v(-118.03, -169.26) * mm, v(-118.18, -169.92) * mm, v(-118.25, -169.97) * mm, v(-119.01, -169.84) * mm]});
            skFitSpline(sketch, "E821", {"points": [v(-119.01, -169.84) * mm, v(-120.48, -169.6) * mm, v(-121.12, -170.9) * mm, v(-120.05, -171.96) * mm]});
            skFitSpline(sketch, "E822", {"points": [v(-120.05, -171.96) * mm, v(-119.62, -172.4) * mm, v(-119.36, -172.45) * mm, v(-118.35, -172.33) * mm]});
            skFitSpline(sketch, "E823", {"points": [v(-117.31, -172.84) * mm, v(-117.4, -173.2) * mm, v(-117.58, -173.6) * mm, v(-117.71, -173.73) * mm]});
            skFitSpline(sketch, "E824", {"points": [v(-117.71, -173.73) * mm, v(-118, -174.03) * mm, v(-123.82, -174.22) * mm, v(-124, -173.93) * mm]});
            skFitSpline(sketch, "E825", {"points": [v(40.24, -167.55) * mm, v(40.25, -166.71) * mm, v(40.57, -166.17) * mm, v(41.05, -166.17) * mm]});
            skFitSpline(sketch, "E826", {"points": [v(41.05, -166.17) * mm, v(41.5, -166.17) * mm, v(41.55, -166.06) * mm, v(41.48, -165.14) * mm]});
            skFitSpline(sketch, "E827", {"points": [v(41.48, -165.14) * mm, v(41.41, -164.3) * mm, v(41.52, -163.96) * mm, v(42, -163.38) * mm]});
            skFitSpline(sketch, "E828", {"points": [v(42, -163.38) * mm, v(42.74, -162.5) * mm, v(44.27, -162) * mm, v(45.54, -162.22) * mm]});
            skFitSpline(sketch, "E829", {"points": [v(45.54, -162.22) * mm, v(46.55, -162.39) * mm, v(46.6, -162.47) * mm, v(46.25, -163.4) * mm]});
            skFitSpline(sketch, "E830", {"points": [v(46.25, -163.4) * mm, v(46.05, -163.92) * mm, v(45.9, -163.98) * mm, v(45.29, -163.86) * mm]});
            skFitSpline(sketch, "E831", {"points": [v(45.29, -163.86) * mm, v(43.94, -163.59) * mm, v(43.36, -164.74) * mm, v(44.35, -165.72) * mm]});
            skFitSpline(sketch, "E832", {"points": [v(44.35, -165.72) * mm, v(44.78, -166.15) * mm, v(45.04, -166.21) * mm, v(46.03, -166.1) * mm]});
            skFitSpline(sketch, "E833", {"points": [v(46.03, -166.1) * mm, v(46.67, -166.02) * mm, v(47.2, -165.99) * mm, v(47.2, -166.03) * mm]});
            skFitSpline(sketch, "E834", {"points": [v(47.2, -166.03) * mm, v(47.2, -166.07) * mm, v(47.08, -166.43) * mm, v(46.94, -166.83) * mm]});
            skFitSpline(sketch, "E835", {"points": [v(46.94, -166.83) * mm, v(46.63, -167.73) * mm, v(46.12, -167.85) * mm, v(42.73, -167.85) * mm]});
            skFitSpline(sketch, "E836", {"points": [v(42.73, -167.85) * mm, v(40.9, -167.85) * mm, v(40.24, -167.77) * mm, v(40.24, -167.55) * mm]});
            skFitSpline(sketch, "E837", {"points": [v(-56.35, -142.15) * mm, v(-60.22, -141.58) * mm, v(-63.04, -140.2) * mm, v(-65.64, -137.6) * mm]});
            skFitSpline(sketch, "E838", {"points": [v(-65.64, -137.6) * mm, v(-68.86, -134.37) * mm, v(-70.33, -130.4) * mm, v(-70.55, -124.41) * mm]});
            skFitSpline(sketch, "E839", {"points": [v(-70.55, -124.41) * mm, v(-70.62, -122.63) * mm, v(-70.58, -120.69) * mm, v(-70.47, -120.1) * mm]});
            skFitSpline(sketch, "E840", {"points": [v(-66.68, -117.9) * mm, v(-64.7, -117.28) * mm, v(-62.65, -116.76) * mm, v(-62.12, -116.75) * mm]});
            skFitSpline(sketch, "E841", {"points": [v(-61.25, -120.8) * mm, v(-61.31, -123.92) * mm, v(-61.24, -125.33) * mm, v(-60.93, -126.86) * mm]});
            skFitSpline(sketch, "E842", {"points": [v(-60.93, -126.86) * mm, v(-59.93, -131.82) * mm, v(-57.38, -134.54) * mm, v(-53.09, -135.2) * mm]});
            skFitSpline(sketch, "E843", {"points": [v(-53.09, -135.2) * mm, v(-51.4, -135.47) * mm, v(-49.2, -135.27) * mm, v(-46.13, -134.58) * mm]});
            skFitSpline(sketch, "E844", {"points": [v(-46.13, -134.58) * mm, v(-44.57, -134.23) * mm, v(-44.54, -134.21) * mm, v(-44.4, -133.34) * mm]});
            skFitSpline(sketch, "E845", {"points": [v(-44.4, -133.34) * mm, v(-44.31, -132.85) * mm, v(-44.25, -122.39) * mm, v(-44.24, -110.09) * mm]});
            skFitSpline(sketch, "E846", {"points": [v(-44.24, -110.09) * mm, v(-44.24, -97.79) * mm, v(-44.15, -87.66) * mm, v(-44.04, -87.6) * mm]});
            skFitSpline(sketch, "E847", {"points": [v(-44.04, -87.6) * mm, v(-43.65, -87.35) * mm, v(-35.12, -85.53) * mm, v(-34.38, -85.53) * mm]});
            skFitSpline(sketch, "E848", {"points": [v(-34.38, -85.53) * mm, v(-33.68, -85.53) * mm, v(-33.64, -85.58) * mm, v(-33.8, -86.2) * mm]});
            skFitSpline(sketch, "E849", {"points": [v(-33.8, -86.2) * mm, v(-33.9, -86.56) * mm, v(-34.06, -96.73) * mm, v(-34.16, -108.81) * mm]});
            skFitSpline(sketch, "E850", {"points": [v(-34.16, -108.81) * mm, v(-34.27, -121.35) * mm, v(-34.47, -131.96) * mm, v(-34.62, -133.53) * mm]});
            skFitSpline(sketch, "E851", {"points": [v(-34.62, -133.53) * mm, v(-35.07, -138.3) * mm, v(-35.18, -139.06) * mm, v(-35.39, -139.19) * mm]});
            skFitSpline(sketch, "E852", {"points": [v(-35.39, -139.19) * mm, v(-35.85, -139.47) * mm, v(-46.46, -141.75) * mm, v(-48.8, -142.06) * mm]});
            skFitSpline(sketch, "E853", {"points": [v(-48.8, -142.06) * mm, v(-51.57, -142.44) * mm, v(-54.16, -142.47) * mm, v(-56.35, -142.15) * mm]});
            skFitSpline(sketch, "E854", {"points": [v(-14.13, -140.95) * mm, v(-15.54, -140.77) * mm, v(-16.53, -140.3) * mm, v(-17.35, -139.43) * mm]});
            skFitSpline(sketch, "E855", {"points": [v(-17.35, -139.43) * mm, v(-18.17, -138.55) * mm, v(-18.31, -136.38) * mm, v(-17.62, -135.28) * mm]});
            skFitSpline(sketch, "E856", {"points": [v(-17.62, -135.28) * mm, v(-16.8, -133.96) * mm, v(-15.42, -133.42) * mm, v(-12.92, -133.42) * mm]});
            skFitSpline(sketch, "E857", {"points": [v(-12.92, -133.42) * mm, v(-11.14, -133.42) * mm, v(-10.58, -133.51) * mm, v(-9.75, -133.96) * mm]});
            skFitSpline(sketch, "E858", {"points": [v(-9.75, -133.96) * mm, v(-6.97, -135.43) * mm, v(-7, -138.97) * mm, v(-9.78, -140.42) * mm]});
            skFitSpline(sketch, "E859", {"points": [v(-9.78, -140.42) * mm, v(-10.7, -140.9) * mm, v(-12.64, -141.14) * mm, v(-14.13, -140.95) * mm]});
            skFitSpline(sketch, "E860", {"points": [v(-2.41, -140.95) * mm, v(-4.82, -140.64) * mm, v(-6.32, -139.18) * mm, v(-6.32, -137.16) * mm]});
            skFitSpline(sketch, "E861", {"points": [v(-6.32, -137.16) * mm, v(-6.32, -135.72) * mm, v(-5.66, -134.66) * mm, v(-4.35, -133.96) * mm]});
            skFitSpline(sketch, "E862", {"points": [v(-4.35, -133.96) * mm, v(-2.87, -133.17) * mm, v(0.54, -133.17) * mm, v(2.01, -133.96) * mm]});
            skFitSpline(sketch, "E863", {"points": [v(2.01, -133.96) * mm, v(4.77, -135.42) * mm, v(4.75, -138.98) * mm, v(1.98, -140.42) * mm]});
            skFitSpline(sketch, "E864", {"points": [v(1.98, -140.42) * mm, v(1.04, -140.9) * mm, v(-0.88, -141.14) * mm, v(-2.41, -140.95) * mm]});
            skFitSpline(sketch, "E865", {"points": [v(16.44, -140.94) * mm, v(13.3, -140.48) * mm, v(11.76, -138.38) * mm, v(12.73, -135.87) * mm]});
            skFitSpline(sketch, "E866", {"points": [v(12.73, -135.87) * mm, v(13.36, -134.22) * mm, v(15.12, -133.31) * mm, v(17.7, -133.3) * mm]});
            skFitSpline(sketch, "E867", {"points": [v(17.7, -133.3) * mm, v(21.4, -133.28) * mm, v(23.67, -135.67) * mm, v(22.6, -138.46) * mm]});
            skFitSpline(sketch, "E868", {"points": [v(22.6, -138.46) * mm, v(22.22, -139.48) * mm, v(21.49, -140.2) * mm, v(20.44, -140.6) * mm]});
            skFitSpline(sketch, "E869", {"points": [v(20.44, -140.6) * mm, v(19.54, -140.94) * mm, v(17.56, -141.1) * mm, v(16.44, -140.94) * mm]});
            skFitSpline(sketch, "E870", {"points": [v(-27.47, -130.78) * mm, v(-27.53, -130.72) * mm, v(-27.5, -130) * mm, v(-27.39, -129.16) * mm]});
            skFitSpline(sketch, "E871", {"points": [v(-27.39, -129.16) * mm, v(-27.28, -128.33) * mm, v(-27.13, -118.6) * mm, v(-27.05, -107.55) * mm]});
            skFitSpline(sketch, "E872", {"points": [v(-26.4, -87.33) * mm, v(-22.43, -86.4) * mm, v(-18.17, -85.53) * mm, v(-17.5, -85.53) * mm]});
            skFitSpline(sketch, "E873", {"points": [v(-16.83, -87.03) * mm, v(-16.92, -87.86) * mm, v(-17, -95.4) * mm, v(-17, -103.77) * mm]});
            skFitSpline(sketch, "E874", {"points": [v(-16.44, -120.14) * mm, v(-15.57, -121.91) * mm, v(-14.66, -122.35) * mm, v(-11.58, -122.46) * mm]});
            skFitSpline(sketch, "E875", {"points": [v(-11.58, -122.46) * mm, v(-6.5, -122.63) * mm, v(-6.09, -121.7) * mm, v(-6.08, -109.85) * mm]});
            skFitSpline(sketch, "E876", {"points": [v(-3.98, -102.38) * mm, v(1.6, -101.1) * mm, v(3.02, -100.83) * mm, v(3.36, -100.96) * mm]});
            skFitSpline(sketch, "E877", {"points": [v(3.36, -100.96) * mm, v(3.67, -101.08) * mm, v(3.74, -102.3) * mm, v(3.82, -109.7) * mm]});
            skFitSpline(sketch, "E878", {"points": [v(3.82, -109.7) * mm, v(3.9, -115.76) * mm, v(4.02, -118.6) * mm, v(4.24, -119.33) * mm]});
            skFitSpline(sketch, "E879", {"points": [v(4.24, -119.33) * mm, v(4.64, -120.68) * mm, v(5.8, -121.89) * mm, v(7, -122.22) * mm]});
            skFitSpline(sketch, "E880", {"points": [v(7, -122.22) * mm, v(7.62, -122.4) * mm, v(11.13, -122.5) * mm, v(17.01, -122.5) * mm]});
            skFitSpline(sketch, "E881", {"points": [v(25.61, -121.71) * mm, v(25.37, -121.28) * mm, v(24.38, -118.67) * mm, v(23.43, -115.9) * mm]});
            skFitSpline(sketch, "E882", {"points": [v(23.43, -115.9) * mm, v(21.06, -108.98) * mm, v(19.92, -106.76) * mm, v(18.1, -105.43) * mm]});
            skFitSpline(sketch, "E883", {"points": [v(18.1, -105.43) * mm, v(16.94, -104.6) * mm, v(15.38, -104.5) * mm, v(12.94, -105.12) * mm]});
            skFitSpline(sketch, "E884", {"points": [v(12.94, -105.12) * mm, v(12.1, -105.33) * mm, v(11.35, -105.44) * mm, v(11.27, -105.37) * mm]});
            skFitSpline(sketch, "E885", {"points": [v(11.27, -105.37) * mm, v(11.2, -105.3) * mm, v(11.5, -103.74) * mm, v(11.96, -101.92) * mm]});
            skFitSpline(sketch, "E886", {"points": [v(13.97, -98.3) * mm, v(15.54, -97.87) * mm, v(19.62, -97.84) * mm, v(21.28, -98.24) * mm]});
            skFitSpline(sketch, "E887", {"points": [v(21.28, -98.24) * mm, v(23.86, -98.86) * mm, v(26.06, -100.22) * mm, v(27.84, -102.31) * mm]});
            skFitSpline(sketch, "E888", {"points": [v(27.84, -102.31) * mm, v(29.5, -104.25) * mm, v(30.7, -106.8) * mm, v(32.42, -112) * mm]});
            skFitSpline(sketch, "E889", {"points": [v(32.42, -112) * mm, v(35.27, -120.6) * mm, v(36.64, -122.5) * mm, v(40, -122.5) * mm]});
            skFitSpline(sketch, "E890", {"points": [v(40, -122.5) * mm, v(40.76, -122.5) * mm, v(41.2, -122.6) * mm, v(41.2, -122.77) * mm]});
            skFitSpline(sketch, "E891", {"points": [v(41.2, -122.77) * mm, v(41.2, -122.93) * mm, v(40.85, -124.5) * mm, v(40.43, -126.25) * mm]});
            skFitSpline(sketch, "E892", {"points": [v(22.48, -129.45) * mm, v(8.05, -129.45) * mm, v(5.08, -129.4) * mm, v(3.93, -129.1) * mm]});
            skFitSpline(sketch, "E893", {"points": [v(3.93, -129.1) * mm, v(2.56, -128.74) * mm, v(1.18, -128) * mm, v(0.28, -127.13) * mm]});
            skFitSpline(sketch, "E894", {"points": [v(0.28, -127.13) * mm, v(-0.19, -126.67) * mm, v(-0.2, -126.67) * mm, v(-1.2, -127.44) * mm]});
            skFitSpline(sketch, "E895", {"points": [v(-1.2, -127.44) * mm, v(-3.36, -129.08) * mm, v(-4.38, -129.3) * mm, v(-10.5, -129.4) * mm]});
            skFitSpline(sketch, "E896", {"points": [v(-10.5, -129.4) * mm, v(-16.62, -129.51) * mm, v(-19.03, -129.27) * mm, v(-21.39, -128.33) * mm]});
            skFitSpline(sketch, "E897", {"points": [v(-24.7, -129.12) * mm, v(-25.7, -129.88) * mm, v(-26.56, -130.59) * mm, v(-26.63, -130.7) * mm]});
            skFitSpline(sketch, "E898", {"points": [v(-26.63, -130.7) * mm, v(-26.76, -130.9) * mm, v(-27.3, -130.96) * mm, v(-27.47, -130.78) * mm]});
            skFitSpline(sketch, "E899", {"points": [v(44.46, -128.91) * mm, v(44.57, -128.61) * mm, v(44.7, -119.16) * mm, v(44.74, -107.91) * mm]});
            skFitSpline(sketch, "E900", {"points": [v(44.74, -107.91) * mm, v(44.78, -96.66) * mm, v(44.85, -87.45) * mm, v(44.9, -87.45) * mm]});
            skFitSpline(sketch, "E901", {"points": [v(44.9, -87.45) * mm, v(44.93, -87.45) * mm, v(46.9, -87.02) * mm, v(49.24, -86.5) * mm]});
            skFitSpline(sketch, "E902", {"points": [v(49.24, -86.5) * mm, v(51.59, -85.96) * mm, v(53.92, -85.53) * mm, v(54.42, -85.53) * mm]});
            skFitSpline(sketch, "E903", {"points": [v(55.2, -86.43) * mm, v(55.14, -86.93) * mm, v(55.03, -87.55) * mm, v(54.95, -87.81) * mm]});
            skFitSpline(sketch, "E904", {"points": [v(54.95, -87.81) * mm, v(54.87, -88.08) * mm, v(54.73, -97.3) * mm, v(54.64, -108.33) * mm]});
            skFitSpline(sketch, "E905", {"points": [v(54.64, -108.33) * mm, v(54.55, -119.35) * mm, v(54.4, -128.61) * mm, v(54.3, -128.91) * mm]});
            skFitSpline(sketch, "E906", {"points": [v(54.3, -128.91) * mm, v(54.1, -129.45) * mm, v(54.07, -129.45) * mm, v(49.18, -129.45) * mm]});
            skFitSpline(sketch, "E907", {"points": [v(45.16, -79.3) * mm, v(44.67, -78.34) * mm, v(44.71, -76.26) * mm, v(45.25, -75.1) * mm]});
            skFitSpline(sketch, "E908", {"points": [v(45.25, -75.1) * mm, v(46.34, -72.74) * mm, v(48.76, -71.37) * mm, v(51.83, -71.37) * mm]});
            skFitSpline(sketch, "E909", {"points": [v(51.83, -71.37) * mm, v(53.5, -71.38) * mm, v(55.36, -71.72) * mm, v(55.36, -72.02) * mm]});
            skFitSpline(sketch, "E910", {"points": [v(55.36, -72.02) * mm, v(55.36, -72.1) * mm, v(55.18, -72.75) * mm, v(54.95, -73.45) * mm]});
            skFitSpline(sketch, "E911", {"points": [v(52.73, -74.59) * mm, v(51.1, -74.46) * mm, v(50.87, -74.5) * mm, v(50.38, -74.96) * mm]});
            skFitSpline(sketch, "E912", {"points": [v(50.38, -74.96) * mm, v(49.96, -75.36) * mm, v(49.84, -75.74) * mm, v(49.84, -76.67) * mm]});
            skFitSpline(sketch, "E913", {"points": [v(49.84, -76.67) * mm, v(49.84, -78.21) * mm, v(50.37, -79.24) * mm, v(51.4, -79.67) * mm]});
            skFitSpline(sketch, "E914", {"points": [v(51.4, -79.67) * mm, v(52.32, -80.05) * mm, v(54.52, -80.11) * mm, v(55.9, -79.8) * mm]});
            skFitSpline(sketch, "E915", {"points": [v(55.9, -79.8) * mm, v(56.4, -79.68) * mm, v(56.8, -79.67) * mm, v(56.8, -79.78) * mm]});
            skFitSpline(sketch, "E916", {"points": [v(56.8, -79.78) * mm, v(56.8, -79.88) * mm, v(56.57, -80.57) * mm, v(56.29, -81.3) * mm]});
            skFitSpline(sketch, "E917", {"points": [v(56.29, -81.3) * mm, v(55.84, -82.48) * mm, v(55.67, -82.68) * mm, v(54.9, -82.89) * mm]});
            skFitSpline(sketch, "E918", {"points": [v(54.9, -82.89) * mm, v(54.43, -83.02) * mm, v(51.37, -83.13) * mm, v(48.12, -83.13) * mm]});
            skFitSpline(sketch, "E919", {"points": [v(3.7, -49.71) * mm, v(0.7, -47.19) * mm, v(-1.72, -45.1) * mm, v(-1.69, -45.06) * mm]});
            skFitSpline(sketch, "E920", {"points": [v(-1.69, -45.06) * mm, v(-1.53, -44.9) * mm, v(12.47, -42.32) * mm, v(12.58, -42.43) * mm]});
            skFitSpline(sketch, "E921", {"points": [v(12.58, -42.43) * mm, v(12.72, -42.57) * mm, v(9.57, -53.87) * mm, v(9.32, -54.14) * mm]});
            skFitSpline(sketch, "E922", {"points": [v(9.32, -54.14) * mm, v(9.23, -54.23) * mm, v(6.7, -52.24) * mm, v(3.7, -49.71) * mm]});
            skFitSpline(sketch, "E923", {"points": [v(23.5, -49.95) * mm, v(25.07, -46.05) * mm, v(30.03, -34.23) * mm, v(30.17, -34.08) * mm]});
            skFitSpline(sketch, "E924", {"points": [v(30.17, -34.08) * mm, v(30.28, -33.96) * mm, v(32.7, -36.12) * mm, v(35.67, -38.98) * mm]});
            skFitSpline(sketch, "E925", {"points": [v(35.67, -38.98) * mm, v(38.58, -41.8) * mm, v(40.88, -44.18) * mm, v(40.78, -44.27) * mm]});
            skFitSpline(sketch, "E926", {"points": [v(40.78, -44.27) * mm, v(40.62, -44.43) * mm, v(36.58, -45.84) * mm, v(26.69, -49.2) * mm]});
            skFitSpline(sketch, "E927", {"points": [v(26.69, -49.2) * mm, v(24.98, -49.78) * mm, v(23.54, -50.25) * mm, v(23.48, -50.25) * mm]});
            skFitSpline(sketch, "E928", {"points": [v(23.48, -50.25) * mm, v(23.43, -50.25) * mm, v(23.44, -50.12) * mm, v(23.5, -49.95) * mm]});
            skFitSpline(sketch, "E929", {"points": [v(-29.08, -45.48) * mm, v(-35.45, -43.67) * mm, v(-40.68, -42.1) * mm, v(-40.7, -41.97) * mm]});
            skFitSpline(sketch, "E930", {"points": [v(-40.7, -41.97) * mm, v(-40.7, -41.85) * mm, v(-38.35, -39.9) * mm, v(-35.46, -37.64) * mm]});
            skFitSpline(sketch, "E931", {"points": [v(-18.1, -42.64) * mm, v(-17.68, -45.57) * mm, v(-17.27, -48.16) * mm, v(-17.2, -48.4) * mm]});
            skFitSpline(sketch, "E932", {"points": [v(-17.2, -48.4) * mm, v(-17.14, -48.62) * mm, v(-17.18, -48.8) * mm, v(-17.29, -48.8) * mm]});
            skFitSpline(sketch, "E933", {"points": [v(-17.29, -48.8) * mm, v(-17.4, -48.78) * mm, v(-22.7, -47.3) * mm, v(-29.08, -45.48) * mm]});
            skFitSpline(sketch, "E934", {"points": [v(-56.48, -40.63) * mm, v(-58.8, -39.44) * mm, v(-63.98, -36.78) * mm, v(-68, -34.73) * mm]});
            skFitSpline(sketch, "E935", {"points": [v(-68, -34.73) * mm, v(-72.03, -32.67) * mm, v(-75.4, -30.92) * mm, v(-75.5, -30.84) * mm]});
            skFitSpline(sketch, "E936", {"points": [v(-75.5, -30.84) * mm, v(-75.62, -30.72) * mm, v(-59.15, -23.14) * mm, v(-56.96, -22.3) * mm]});
            skFitSpline(sketch, "E937", {"points": [v(-56.96, -22.3) * mm, v(-56.68, -22.2) * mm, v(-56.5, -22.59) * mm, v(-56.16, -24.15) * mm]});
            skFitSpline(sketch, "E938", {"points": [v(-56.16, -24.15) * mm, v(-55.59, -26.72) * mm, v(-52.23, -41.39) * mm, v(-52.03, -42.2) * mm]});
            skFitSpline(sketch, "E939", {"points": [v(-52.03, -42.2) * mm, v(-51.94, -42.53) * mm, v(-51.96, -42.8) * mm, v(-52.08, -42.8) * mm]});
            skFitSpline(sketch, "E940", {"points": [v(-52.08, -42.8) * mm, v(-52.19, -42.8) * mm, v(-54.17, -41.82) * mm, v(-56.48, -40.63) * mm]});
            skFitSpline(sketch, "E941", {"points": [v(55.04, -32.86) * mm, v(52.84, -30.03) * mm, v(51.04, -27.67) * mm, v(51.04, -27.63) * mm]});
            skFitSpline(sketch, "E942", {"points": [v(51.04, -27.63) * mm, v(51.04, -27.37) * mm, v(62.35, -23.07) * mm, v(62.53, -23.27) * mm]});
            skFitSpline(sketch, "E943", {"points": [v(62.53, -23.27) * mm, v(62.8, -23.58) * mm, v(67.46, -35.6) * mm, v(67.34, -35.7) * mm]});
            skFitSpline(sketch, "E944", {"points": [v(67.34, -35.7) * mm, v(67.18, -35.8) * mm, v(59.52, -38.01) * mm, v(59.27, -38.01) * mm]});
            skFitSpline(sketch, "E945", {"points": [v(59.27, -38.01) * mm, v(59.15, -38.01) * mm, v(57.24, -35.7) * mm, v(55.04, -32.86) * mm]});
            skFitSpline(sketch, "E946", {"points": [v(-7.56, -30.46) * mm, v(-7.62, -30.39) * mm, v(-7.55, -29.49) * mm, v(-7.38, -28.46) * mm]});
            skFitSpline(sketch, "E947", {"points": [v(-7.38, -28.46) * mm, v(-7.1, -26.66) * mm, v(-5.98, -19.3) * mm, v(-5.2, -14.01) * mm]});
            skFitSpline(sketch, "E948", {"points": [v(-5.2, -14.01) * mm, v(-5, -12.63) * mm, v(-4.8, -11.45) * mm, v(-4.75, -11.4) * mm]});
            skFitSpline(sketch, "E949", {"points": [v(-4.75, -11.4) * mm, v(-4.62, -11.26) * mm, v(-3.73, -11.97) * mm, v(-0.24, -15.02) * mm]});
            skFitSpline(sketch, "E950", {"points": [v(-0.24, -15.02) * mm, v(1.63, -16.65) * mm, v(5.25, -19.82) * mm, v(7.8, -22.05) * mm]});
            skFitSpline(sketch, "E951", {"points": [v(7.8, -22.05) * mm, v(11.57, -25.34) * mm, v(12.36, -26.15) * mm, v(12, -26.28) * mm]});
            skFitSpline(sketch, "E952", {"points": [v(12, -26.28) * mm, v(11.76, -26.37) * mm, v(10, -26.78) * mm, v(8.08, -27.19) * mm]});
            skFitSpline(sketch, "E953", {"points": [v(8.08, -27.19) * mm, v(6.16, -27.6) * mm, v(3.84, -28.1) * mm, v(2.92, -28.3) * mm]});
            skFitSpline(sketch, "E954", {"points": [v(2.92, -28.3) * mm, v(2, -28.5) * mm, v(0.7, -28.78) * mm, v(0.04, -28.92) * mm]});
            skFitSpline(sketch, "E955", {"points": [v(0.04, -28.92) * mm, v(-0.62, -29.06) * mm, v(-1.54, -29.26) * mm, v(-2, -29.37) * mm]});
            skFitSpline(sketch, "E956", {"points": [v(-2, -29.37) * mm, v(-2.46, -29.47) * mm, v(-3.7, -29.74) * mm, v(-4.76, -29.96) * mm]});
            skFitSpline(sketch, "E957", {"points": [v(-4.76, -29.96) * mm, v(-5.82, -30.18) * mm, v(-6.85, -30.4) * mm, v(-7.06, -30.47) * mm]});
            skFitSpline(sketch, "E958", {"points": [v(-7.06, -30.47) * mm, v(-7.27, -30.53) * mm, v(-7.5, -30.52) * mm, v(-7.56, -30.46) * mm]});
            skFitSpline(sketch, "E959", {"points": [v(73.92, -25.11) * mm, v(73.7, -24.02) * mm, v(73.71, -24.06) * mm, v(73.53, -23.61) * mm]});
            skFitSpline(sketch, "E960", {"points": [v(73.53, -23.61) * mm, v(72.97, -22.19) * mm, v(70.84, -14.25) * mm, v(71.02, -14.25) * mm]});
            skFitSpline(sketch, "E961", {"points": [v(71.02, -14.25) * mm, v(71.14, -14.25) * mm, v(72.32, -14.85) * mm, v(73.62, -15.57) * mm]});
            skFitSpline(sketch, "E962", {"points": [v(73.62, -15.57) * mm, v(74.93, -16.3) * mm, v(77.1, -17.5) * mm, v(78.43, -18.24) * mm]});
            skFitSpline(sketch, "E963", {"points": [v(77.65, -22.8) * mm, v(75.89, -24.57) * mm, v(74.37, -26.01) * mm, v(74.27, -26.01) * mm]});
            skFitSpline(sketch, "E964", {"points": [v(74.27, -26.01) * mm, v(74.18, -26.01) * mm, v(74.02, -25.6) * mm, v(73.92, -25.11) * mm]});
            skFitSpline(sketch, "E965", {"points": [v(-23.21, -22.6) * mm, v(-23.3, -21.11) * mm, v(-23.42, -17.03) * mm, v(-23.5, -13.53) * mm]});
            skFitSpline(sketch, "E966", {"points": [v(-18.28, -7.5) * mm, v(-15.34, -7.68) * mm, v(-12.89, -7.86) * mm, v(-12.84, -7.9) * mm]});
            skFitSpline(sketch, "E967", {"points": [v(-12.84, -7.9) * mm, v(-12.78, -7.96) * mm, v(-22.68, -24.85) * mm, v(-23.01, -25.25) * mm]});
            skFitSpline(sketch, "E968", {"points": [v(-23.01, -25.25) * mm, v(-23.04, -25.29) * mm, v(-23.14, -24.1) * mm, v(-23.21, -22.6) * mm]});
            skFitSpline(sketch, "E969", {"points": [v(25.72, -14.45) * mm, v(25.63, -12.95) * mm, v(25.6, -11.21) * mm, v(25.64, -10.58) * mm]});
            skFitSpline(sketch, "E970", {"points": [v(29.37, -12.14) * mm, v(31.38, -13.63) * mm, v(33.02, -14.9) * mm, v(33.03, -14.97) * mm]});
            skFitSpline(sketch, "E971", {"points": [v(33.03, -14.97) * mm, v(33.03, -15.04) * mm, v(31.56, -15.5) * mm, v(29.76, -16.01) * mm]});
            skFitSpline(sketch, "E972", {"points": [v(29.76, -16.01) * mm, v(27.96, -16.52) * mm, v(26.35, -16.99) * mm, v(26.19, -17.05) * mm]});
            skFitSpline(sketch, "E973", {"points": [v(26.19, -17.05) * mm, v(25.96, -17.14) * mm, v(25.84, -16.46) * mm, v(25.72, -14.45) * mm]});
            skFitSpline(sketch, "E974", {"points": [v(-57.16, -14.38) * mm, v(-61.3, -13.28) * mm, v(-64.71, -12.34) * mm, v(-64.76, -12.3) * mm]});
            skFitSpline(sketch, "E975", {"points": [v(-64.76, -12.3) * mm, v(-64.84, -12.21) * mm, v(-58.84, -1.17) * mm, v(-58.58, -0.9) * mm]});
            skFitSpline(sketch, "E976", {"points": [v(-58.58, -0.9) * mm, v(-58.46, -0.8) * mm, v(-49.28, -15.97) * mm, v(-49.28, -16.27) * mm]});
            skFitSpline(sketch, "E977", {"points": [v(-49.28, -16.27) * mm, v(-49.28, -16.48) * mm, v(-49.08, -16.53) * mm, v(-57.16, -14.38) * mm]});
            skFitSpline(sketch, "E978", {"points": [v(93.28, -15.72) * mm, v(93.28, -15.46) * mm, v(93.76, -10.68) * mm, v(94.36, -5.1) * mm]});
            skFitSpline(sketch, "E979", {"points": [v(94.36, -5.1) * mm, v(94.95, 0.5) * mm, v(95.67, 7.39) * mm, v(95.96, 10.23) * mm]});
            skFitSpline(sketch, "E980", {"points": [v(95.96, 10.23) * mm, v(96.25, 13.07) * mm, v(96.51, 15.43) * mm, v(96.55, 15.48) * mm]});
            skFitSpline(sketch, "E981", {"points": [v(96.55, 15.48) * mm, v(96.59, 15.53) * mm, v(99.73, 14.16) * mm, v(103.53, 12.43) * mm]});
            skFitSpline(sketch, "E982", {"points": [v(103.53, 12.43) * mm, v(107.33, 10.7) * mm, v(112.32, 8.44) * mm, v(114.63, 7.4) * mm]});
            skFitSpline(sketch, "E983", {"points": [v(114.63, 7.4) * mm, v(116.93, 6.36) * mm, v(118.84, 5.4) * mm, v(118.87, 5.28) * mm]});
            skFitSpline(sketch, "E984", {"points": [v(118.87, 5.28) * mm, v(118.9, 5.17) * mm, v(114.5, 1.4) * mm, v(109.08, -3.1) * mm]});
            skFitSpline(sketch, "E985", {"points": [v(109.08, -3.1) * mm, v(103.66, -7.58) * mm, v(97.89, -12.36) * mm, v(96.25, -13.72) * mm]});
            skFitSpline(sketch, "E986", {"points": [v(96.25, -13.72) * mm, v(94, -15.59) * mm, v(93.28, -16.07) * mm, v(93.28, -15.72) * mm]});
            skFitSpline(sketch, "E987", {"points": [v(-102.92, -7.98) * mm, v(-105.96, -4.7) * mm, v(-108.86, -1.55) * mm, v(-109.37, -0.99) * mm]});
            skFitSpline(sketch, "E988", {"points": [v(-109.37, -0.99) * mm, v(-109.88, -0.43) * mm, v(-111.55, 1.38) * mm, v(-113.09, 3.03) * mm]});
            skFitSpline(sketch, "E989", {"points": [v(-107.14, 6.1) * mm, v(-102.34, 6.13) * mm, v(-98.39, 6.13) * mm, v(-98.36, 6.1) * mm]});
            skFitSpline(sketch, "E990", {"points": [v(-98.36, 6.1) * mm, v(-98.3, 6) * mm, v(-97.3, -13.88) * mm, v(-97.36, -13.93) * mm]});
            skFitSpline(sketch, "E991", {"points": [v(-97.36, -13.93) * mm, v(-97.38, -13.95) * mm, v(-99.89, -11.27) * mm, v(-102.92, -7.98) * mm]});
            skFitSpline(sketch, "E992", {"points": [v(-39.43, -8.24) * mm, v(-41.98, -5.6) * mm, v(-44.02, -3.4) * mm, v(-43.97, -3.35) * mm]});
            skFitSpline(sketch, "E993", {"points": [v(-43.97, -3.35) * mm, v(-43.78, -3.19) * mm, v(-36.29, -1.98) * mm, v(-36.02, -2.07) * mm]});
            skFitSpline(sketch, "E994", {"points": [v(-36.02, -2.07) * mm, v(-35.72, -2.17) * mm, v(-34.36, -13.05) * mm, v(-34.65, -13.05) * mm]});
            skFitSpline(sketch, "E995", {"points": [v(-34.65, -13.05) * mm, v(-34.73, -13.05) * mm, v(-36.88, -10.89) * mm, v(-39.43, -8.24) * mm]});
            skFitSpline(sketch, "E996", {"points": [v(48.14, -9.67) * mm, v(47.03, -9) * mm, v(44.23, -7.3) * mm, v(41.92, -5.91) * mm]});
            skFitSpline(sketch, "E997", {"points": [v(41.92, -5.91) * mm, v(39.6, -4.52) * mm, v(37.63, -3.3) * mm, v(37.52, -3.2) * mm]});
            skFitSpline(sketch, "E998", {"points": [v(37.52, -3.2) * mm, v(37.42, -3.11) * mm, v(39.45, -2.2) * mm, v(42.04, -1.18) * mm]});
            skFitSpline(sketch, "E999", {"points": [v(42.04, -1.18) * mm, v(44.64, -0.16) * mm, v(46.85, 0.59) * mm, v(46.95, 0.47) * mm]});
            skFitSpline(sketch, "E1000", {"points": [v(46.95, 0.47) * mm, v(47.17, 0.24) * mm, v(50.35, -10.7) * mm, v(50.23, -10.82) * mm]});
            skFitSpline(sketch, "E1001", {"points": [v(50.23, -10.82) * mm, v(50.2, -10.86) * mm, v(49.25, -10.34) * mm, v(48.14, -9.67) * mm]});
            skFitSpline(sketch, "E1002", {"points": [v(78.7, -8.57) * mm, v(76.42, -7.7) * mm, v(74.56, -6.9) * mm, v(74.56, -6.78) * mm]});
            skFitSpline(sketch, "E1003", {"points": [v(74.56, -6.78) * mm, v(74.56, -6.54) * mm, v(79.74, 1.8) * mm, v(80.18, 2.26) * mm]});
            skFitSpline(sketch, "E1004", {"points": [v(80.18, 2.26) * mm, v(80.4, 2.5) * mm, v(80.74, 1.28) * mm, v(81.75, -3.5) * mm]});
            skFitSpline(sketch, "E1005", {"points": [v(81.75, -3.5) * mm, v(82.45, -6.84) * mm, v(83.07, -9.7) * mm, v(83.13, -9.87) * mm]});
            skFitSpline(sketch, "E1006", {"points": [v(83.13, -9.87) * mm, v(83.2, -10.04) * mm, v(83.16, -10.17) * mm, v(83.04, -10.16) * mm]});
            skFitSpline(sketch, "E1007", {"points": [v(83.04, -10.16) * mm, v(82.93, -10.16) * mm, v(80.98, -9.44) * mm, v(78.7, -8.57) * mm]});
            skFitSpline(sketch, "E1008", {"points": [v(-88.46, -3.15) * mm, v(-89.6, -0.1) * mm, v(-90.48, 2.47) * mm, v(-90.41, 2.54) * mm]});
            skFitSpline(sketch, "E1009", {"points": [v(-90.41, 2.54) * mm, v(-90.24, 2.7) * mm, v(-82.13, 3.18) * mm, v(-82.05, 3.03) * mm]});
            skFitSpline(sketch, "E1010", {"points": [v(-82.05, 3.03) * mm, v(-81.98, 2.89) * mm, v(-86.06, -8.4) * mm, v(-86.25, -8.58) * mm]});
            skFitSpline(sketch, "E1011", {"points": [v(-86.25, -8.58) * mm, v(-86.32, -8.65) * mm, v(-87.31, -6.2) * mm, v(-88.46, -3.15) * mm]});
            skFitSpline(sketch, "E1012", {"points": [v(19.98, -0.3) * mm, v(19.73, 0.46) * mm, v(16.2, 19.6) * mm, v(16.28, 19.8) * mm]});
            skFitSpline(sketch, "E1013", {"points": [v(16.28, 19.8) * mm, v(16.35, 20) * mm, v(18.13, 18.56) * mm, v(29.97, 8.8) * mm]});
            skFitSpline(sketch, "E1014", {"points": [v(27.33, 2.55) * mm, v(23.67, 0.94) * mm, v(20.54, -0.44) * mm, v(20.38, -0.5) * mm]});
            skFitSpline(sketch, "E1015", {"points": [v(20.38, -0.5) * mm, v(20.22, -0.57) * mm, v(20.03, -0.48) * mm, v(19.98, -0.3) * mm]});
            skFitSpline(sketch, "E1016", {"points": [v(-47.12, 9.25) * mm, v(-47.12, 9.38) * mm, v(-46.31, 16) * mm, v(-45.32, 23.97) * mm]});
            skFitSpline(sketch, "E1017", {"points": [v(-45.32, 23.97) * mm, v(-44.33, 31.94) * mm, v(-43.52, 38.6) * mm, v(-43.52, 38.75) * mm]});
            skFitSpline(sketch, "E1018", {"points": [v(-43.52, 38.75) * mm, v(-43.52, 38.9) * mm, v(-43.44, 39.03) * mm, v(-43.33, 39.03) * mm]});
            skFitSpline(sketch, "E1019", {"points": [v(-43.33, 39.03) * mm, v(-43.23, 39.03) * mm, v(-40.4, 36.62) * mm, v(-37.03, 33.68) * mm]});
            skFitSpline(sketch, "E1020", {"points": [v(-30.87, 19.7) * mm, v(-30.84, 14.95) * mm, v(-30.9, 10.94) * mm, v(-31, 10.78) * mm]});
            skFitSpline(sketch, "E1021", {"points": [v(-31, 10.78) * mm, v(-31.11, 10.6) * mm, v(-33.8, 10.23) * mm, v(-38.69, 9.76) * mm]});
            skFitSpline(sketch, "E1022", {"points": [v(-38.69, 9.76) * mm, v(-47.08, 8.94) * mm, v(-47.12, 8.94) * mm, v(-47.12, 9.25) * mm]});
            skFitSpline(sketch, "E1023", {"points": [v(-20.96, 11.91) * mm, v(-20.96, 12.31) * mm, v(-18.93, 36.64) * mm, v(-18.74, 38.54) * mm]});
            skFitSpline(sketch, "E1024", {"points": [v(-18.74, 38.54) * mm, v(-18.69, 39.07) * mm, v(-18.26, 38.73) * mm, v(-14.96, 35.55) * mm]});
            skFitSpline(sketch, "E1025", {"points": [v(-14.96, 35.55) * mm, v(-12.92, 33.58) * mm, v(-8.49, 29.31) * mm, v(-5.13, 26.07) * mm]});
            skFitSpline(sketch, "E1026", {"points": [v(-5.13, 26.07) * mm, v(-1.76, 22.84) * mm, v(2.67, 18.57) * mm, v(4.71, 16.6) * mm]});
            skFitSpline(sketch, "E1027", {"points": [v(4.71, 16.6) * mm, v(6.76, 14.63) * mm, v(8.47, 12.93) * mm, v(8.52, 12.82) * mm]});
            skFitSpline(sketch, "E1028", {"points": [v(8.52, 12.82) * mm, v(8.56, 12.72) * mm, v(8.24, 12.63) * mm, v(7.8, 12.62) * mm]});
            skFitSpline(sketch, "E1029", {"points": [v(7.8, 12.62) * mm, v(7.36, 12.62) * mm, v(1.22, 12.35) * mm, v(-5.84, 12.03) * mm]});
            skFitSpline(sketch, "E1030", {"points": [v(-5.84, 12.03) * mm, v(-21.75, 11.29) * mm, v(-20.96, 11.3) * mm, v(-20.96, 11.91) * mm]});
            skFitSpline(sketch, "E1031", {"points": [v(44.32, 14.74) * mm, v(39.68, 17.18) * mm, v(37.26, 18.46) * mm, v(31, 21.76) * mm]});
            skFitSpline(sketch, "E1032", {"points": [v(31, 21.76) * mm, v(26.6, 24.09) * mm, v(22.52, 26.23) * mm, v(19.3, 27.9) * mm]});
            skFitSpline(sketch, "E1033", {"points": [v(19.3, 27.9) * mm, v(17.6, 28.78) * mm, v(16.27, 29.54) * mm, v(16.32, 29.58) * mm]});
            skFitSpline(sketch, "E1034", {"points": [v(16.32, 29.58) * mm, v(16.4, 29.67) * mm, v(19.45, 29.97) * mm, v(23.32, 30.28) * mm]});
            skFitSpline(sketch, "E1035", {"points": [v(23.32, 30.28) * mm, v(24.24, 30.35) * mm, v(26.08, 30.51) * mm, v(27.4, 30.63) * mm]});
            skFitSpline(sketch, "E1036", {"points": [v(27.4, 30.63) * mm, v(34.05, 31.25) * mm, v(41.71, 31.87) * mm, v(41.77, 31.8) * mm]});
            skFitSpline(sketch, "E1037", {"points": [v(41.77, 31.8) * mm, v(41.81, 31.75) * mm, v(42.5, 30.03) * mm, v(43.3, 27.99) * mm]});
            skFitSpline(sketch, "E1038", {"points": [v(43.3, 27.99) * mm, v(44.1, 25.94) * mm, v(45.83, 21.54) * mm, v(47.15, 18.2) * mm]});
            skFitSpline(sketch, "E1039", {"points": [v(47.15, 18.2) * mm, v(48.47, 14.87) * mm, v(49.48, 12.15) * mm, v(49.4, 12.15) * mm]});
            skFitSpline(sketch, "E1040", {"points": [v(49.4, 12.15) * mm, v(49.3, 12.16) * mm, v(47.02, 13.32) * mm, v(44.32, 14.74) * mm]});
            skFitSpline(sketch, "E1041", {"points": [v(80.2, 18.67) * mm, v(78.09, 21.58) * mm, v(76.27, 24.15) * mm, v(76.16, 24.37) * mm]});
            skFitSpline(sketch, "E1042", {"points": [v(76.16, 24.37) * mm, v(76.02, 24.66) * mm, v(76.4, 25.59) * mm, v(77.48, 27.57) * mm]});
            skFitSpline(sketch, "E1043", {"points": [v(77.48, 27.57) * mm, v(78.32, 29.11) * mm, v(79.07, 30.38) * mm, v(79.17, 30.38) * mm]});
            skFitSpline(sketch, "E1044", {"points": [v(79.17, 30.38) * mm, v(79.46, 30.4) * mm, v(86.42, 27.2) * mm, v(86.7, 26.93) * mm]});
            skFitSpline(sketch, "E1045", {"points": [v(86.7, 26.93) * mm, v(86.9, 26.74) * mm, v(86.6, 24.95) * mm, v(85.6, 20.3) * mm]});
            skFitSpline(sketch, "E1046", {"points": [v(85.6, 20.3) * mm, v(84.85, 16.8) * mm, v(84.2, 13.82) * mm, v(84.14, 13.66) * mm]});
            skFitSpline(sketch, "E1047", {"points": [v(84.14, 13.66) * mm, v(84.08, 13.5) * mm, v(82.31, 15.75) * mm, v(80.2, 18.67) * mm]});
            skFitSpline(sketch, "E1048", {"points": [v(114.68, 18.3) * mm, v(113.08, 20.38) * mm, v(111.8, 22.12) * mm, v(111.87, 22.17) * mm]});
            skFitSpline(sketch, "E1049", {"points": [v(111.87, 22.17) * mm, v(112, 22.3) * mm, v(120.68, 19.62) * mm, v(120.94, 19.37) * mm]});
            skFitSpline(sketch, "E1050", {"points": [v(120.94, 19.37) * mm, v(121.13, 19.2) * mm, v(118.08, 14.55) * mm, v(117.78, 14.55) * mm]});
            skFitSpline(sketch, "E1051", {"points": [v(117.78, 14.55) * mm, v(117.68, 14.55) * mm, v(116.29, 16.24) * mm, v(114.68, 18.3) * mm]});
            skFitSpline(sketch, "E1052", {"points": [v(-66.34, 18.1) * mm, v(-67.73, 19.25) * mm, v(-69.35, 20.57) * mm, v(-69.92, 21.03) * mm]});
            skFitSpline(sketch, "E1053", {"points": [v(-69.92, 21.03) * mm, v(-70.5, 21.49) * mm, v(-71.35, 22.2) * mm, v(-71.82, 22.6) * mm]});
            skFitSpline(sketch, "E1054", {"points": [v(-71.82, 22.6) * mm, v(-72.5, 23.19) * mm, v(-75.73, 25.8) * mm, v(-78.08, 27.67) * mm]});
            skFitSpline(sketch, "E1055", {"points": [v(-78.08, 27.67) * mm, v(-78.28, 27.83) * mm, v(-79.14, 28.54) * mm, v(-80, 29.24) * mm]});
            skFitSpline(sketch, "E1056", {"points": [v(-80, 29.24) * mm, v(-80.86, 29.95) * mm, v(-82.78, 31.54) * mm, v(-84.26, 32.76) * mm]});
            skFitSpline(sketch, "E1057", {"points": [v(-84.26, 32.76) * mm, v(-85.75, 33.99) * mm, v(-86.96, 35.06) * mm, v(-86.96, 35.16) * mm]});
            skFitSpline(sketch, "E1058", {"points": [v(-86.96, 35.16) * mm, v(-86.96, 35.25) * mm, v(-85.31, 35.88) * mm, v(-83.3, 36.56) * mm]});
            skFitSpline(sketch, "E1059", {"points": [v(-83.3, 36.56) * mm, v(-81.29, 37.23) * mm, v(-76.94, 38.72) * mm, v(-73.64, 39.86) * mm]});
            skFitSpline(sketch, "E1060", {"points": [v(-73.64, 39.86) * mm, v(-63.23, 43.45) * mm, v(-61.94, 43.86) * mm, v(-61.77, 43.66) * mm]});
            skFitSpline(sketch, "E1061", {"points": [v(-61.77, 43.66) * mm, v(-61.67, 43.56) * mm, v(-61.68, 42.28) * mm, v(-61.78, 40.83) * mm]});
            skFitSpline(sketch, "E1062", {"points": [v(-61.78, 40.83) * mm, v(-62.1, 36.49) * mm, v(-62.46, 30.87) * mm, v(-62.84, 24.5) * mm]});
            skFitSpline(sketch, "E1063", {"points": [v(-62.84, 24.5) * mm, v(-63.24, 17.7) * mm, v(-63.4, 15.98) * mm, v(-63.64, 16) * mm]});
            skFitSpline(sketch, "E1064", {"points": [v(-63.64, 16) * mm, v(-63.73, 16) * mm, v(-64.94, 16.95) * mm, v(-66.34, 18.1) * mm]});
            skFitSpline(sketch, "E1065", {"points": [v(-112.42, 26.47) * mm, v(-115.77, 30.26) * mm, v(-118.65, 33.54) * mm, v(-118.8, 33.76) * mm]});
            skFitSpline(sketch, "E1066", {"points": [v(-118.8, 33.76) * mm, v(-119.07, 34.12) * mm, v(-118.76, 34.22) * mm, v(-115.69, 34.81) * mm]});
            skFitSpline(sketch, "E1067", {"points": [v(-115.69, 34.81) * mm, v(-113.82, 35.17) * mm, v(-111.55, 35.6) * mm, v(-110.65, 35.78) * mm]});
            skFitSpline(sketch, "E1068", {"points": [v(-105.97, 33.7) * mm, v(-104.3, 32.4) * mm, v(-102.89, 31.22) * mm, v(-102.84, 31.1) * mm]});
            skFitSpline(sketch, "E1069", {"points": [v(-102.84, 31.1) * mm, v(-102.8, 30.97) * mm, v(-103.32, 28.96) * mm, v(-104, 26.61) * mm]});
            skFitSpline(sketch, "E1070", {"points": [v(-104, 26.61) * mm, v(-104.7, 24.27) * mm, v(-105.43, 21.73) * mm, v(-105.65, 20.97) * mm]});
            skFitSpline(sketch, "E1071", {"points": [v(-105.65, 20.97) * mm, v(-105.86, 20.2) * mm, v(-106.1, 19.59) * mm, v(-106.18, 19.59) * mm]});
            skFitSpline(sketch, "E1072", {"points": [v(-106.18, 19.59) * mm, v(-106.25, 19.59) * mm, v(-109.06, 22.69) * mm, v(-112.42, 26.47) * mm]});
            skFitSpline(sketch, "E1073", {"points": [v(53.22, 26.6) * mm, v(50.54, 30.79) * mm, v(46.84, 36.48) * mm, v(44.02, 40.76) * mm]});
            skFitSpline(sketch, "E1074", {"points": [v(44.02, 40.76) * mm, v(42.47, 43.11) * mm, v(41.2, 45.08) * mm, v(41.2, 45.12) * mm]});
            skFitSpline(sketch, "E1075", {"points": [v(41.2, 45.12) * mm, v(41.2, 45.16) * mm, v(40.42, 46.39) * mm, v(39.46, 47.84) * mm]});
            skFitSpline(sketch, "E1076", {"points": [v(39.46, 47.84) * mm, v(37.43, 50.91) * mm, v(32.47, 58.5) * mm, v(30.26, 61.93) * mm]});
            skFitSpline(sketch, "E1077", {"points": [v(30.26, 61.93) * mm, v(29.42, 63.24) * mm, v(28.76, 64.35) * mm, v(28.8, 64.4) * mm]});
            skFitSpline(sketch, "E1078", {"points": [v(28.8, 64.4) * mm, v(28.86, 64.45) * mm, v(32.88, 62.3) * mm, v(37.75, 59.64) * mm]});
            skFitSpline(sketch, "E1079", {"points": [v(37.75, 59.64) * mm, v(42.62, 56.98) * mm, v(49.08, 53.46) * mm, v(52.12, 51.81) * mm]});
            skFitSpline(sketch, "E1080", {"points": [v(52.12, 51.81) * mm, v(55.15, 50.16) * mm, v(58.34, 48.43) * mm, v(59.2, 47.96) * mm]});
            skFitSpline(sketch, "E1081", {"points": [v(59.2, 47.96) * mm, v(60.06, 47.49) * mm, v(62.1, 46.37) * mm, v(63.76, 45.48) * mm]});
            skFitSpline(sketch, "E1082", {"points": [v(63.76, 45.48) * mm, v(67.92, 43.23) * mm, v(67.73, 43.43) * mm, v(66.92, 42.27) * mm]});
            skFitSpline(sketch, "E1083", {"points": [v(66.92, 42.27) * mm, v(65.2, 39.77) * mm, v(57.58, 28.48) * mm, v(55.97, 26) * mm]});
            skFitSpline(sketch, "E1084", {"points": [v(55.97, 26) * mm, v(55.48, 25.25) * mm, v(54.98, 24.57) * mm, v(54.86, 24.5) * mm]});
            skFitSpline(sketch, "E1085", {"points": [v(54.86, 24.5) * mm, v(54.75, 24.43) * mm, v(54, 25.37) * mm, v(53.22, 26.6) * mm]});
            skFitSpline(sketch, "E1086", {"points": [v(99.7, 31.48) * mm, v(96.3, 35.36) * mm, v(93.5, 38.62) * mm, v(93.46, 38.73) * mm]});
            skFitSpline(sketch, "E1087", {"points": [v(93.46, 38.73) * mm, v(93.43, 38.84) * mm, v(94.08, 40.19) * mm, v(94.92, 41.73) * mm]});
            skFitSpline(sketch, "E1088", {"points": [v(94.92, 41.73) * mm, v(96.3, 44.27) * mm, v(96.51, 44.55) * mm, v(97.2, 44.66) * mm]});
            skFitSpline(sketch, "E1089", {"points": [v(97.2, 44.66) * mm, v(97.62, 44.72) * mm, v(100.28, 45) * mm, v(103.12, 45.27) * mm]});
            skFitSpline(sketch, "E1090", {"points": [v(103.12, 45.27) * mm, v(105.96, 45.54) * mm, v(108.52, 45.81) * mm, v(108.82, 45.88) * mm]});
            skFitSpline(sketch, "E1091", {"points": [v(108.82, 45.88) * mm, v(109.25, 45.97) * mm, v(109.36, 45.9) * mm, v(109.36, 45.45) * mm]});
            skFitSpline(sketch, "E1092", {"points": [v(109.36, 45.45) * mm, v(109.35, 45.15) * mm, v(108.76, 41.18) * mm, v(108.03, 36.63) * mm]});
            skFitSpline(sketch, "E1093", {"points": [v(108.03, 36.63) * mm, v(107.3, 32.07) * mm, v(106.6, 27.54) * mm, v(106.44, 26.55) * mm]});
            skFitSpline(sketch, "E1094", {"points": [v(106.44, 26.55) * mm, v(106.3, 25.56) * mm, v(106.11, 24.67) * mm, v(106.03, 24.58) * mm]});
            skFitSpline(sketch, "E1095", {"points": [v(106.03, 24.58) * mm, v(105.95, 24.5) * mm, v(103.1, 27.6) * mm, v(99.7, 31.48) * mm]});
            skFitSpline(sketch, "E1096", {"points": [v(124.72, 30.32) * mm, v(121.88, 31.31) * mm, v(119.53, 32.15) * mm, v(119.5, 32.19) * mm]});
            skFitSpline(sketch, "E1097", {"points": [v(119.5, 32.19) * mm, v(119.43, 32.24) * mm, v(123.8, 50.64) * mm, v(124.15, 51.82) * mm]});
            skFitSpline(sketch, "E1098", {"points": [v(124.15, 51.82) * mm, v(124.22, 52.06) * mm, v(124.37, 52.22) * mm, v(124.49, 52.18) * mm]});
            skFitSpline(sketch, "E1099", {"points": [v(124.49, 52.18) * mm, v(124.6, 52.14) * mm, v(126.57, 50.63) * mm, v(128.88, 48.81) * mm]});
            skFitSpline(sketch, "E1100", {"points": [v(132.87, 44.5) * mm, v(132.76, 43.93) * mm, v(132.06, 40.12) * mm, v(131.31, 36.03) * mm]});
            skFitSpline(sketch, "E1101", {"points": [v(131.31, 36.03) * mm, v(130.56, 31.94) * mm, v(129.94, 28.57) * mm, v(129.91, 28.55) * mm]});
            skFitSpline(sketch, "E1102", {"points": [v(129.91, 28.55) * mm, v(129.9, 28.53) * mm, v(127.56, 29.33) * mm, v(124.72, 30.32) * mm]});
            skFitSpline(sketch, "E1103", {"points": [v(-8.54, 40.55) * mm, v(-15.76, 45.85) * mm, v(-21.67, 50.3) * mm, v(-21.68, 50.43) * mm]});
            skFitSpline(sketch, "E1104", {"points": [v(-21.68, 50.43) * mm, v(-21.68, 50.79) * mm, v(-11.58, 82.8) * mm, v(-11.4, 83) * mm]});
            skFitSpline(sketch, "E1105", {"points": [v(-11.4, 83) * mm, v(-11.3, 83.1) * mm, v(-9.03, 75.96) * mm, v(-6.34, 67.16) * mm]});
            skFitSpline(sketch, "E1106", {"points": [v(-6.34, 67.16) * mm, v(-3.65, 58.35) * mm, v(-0.06, 46.62) * mm, v(1.64, 41.1) * mm]});
            skFitSpline(sketch, "E1107", {"points": [v(1.64, 41.1) * mm, v(3.34, 35.56) * mm, v(4.7, 31.01) * mm, v(4.66, 30.98) * mm]});
            skFitSpline(sketch, "E1108", {"points": [v(4.66, 30.98) * mm, v(4.63, 30.94) * mm, v(-1.31, 35.25) * mm, v(-8.54, 40.55) * mm]});
            skFitSpline(sketch, "E1109", {"points": [v(-40.64, 47.92) * mm, v(-45.46, 51.1) * mm, v(-50.4, 54.37) * mm, v(-51.63, 55.18) * mm]});
            skFitSpline(sketch, "E1110", {"points": [v(-51.63, 55.18) * mm, v(-54.21, 56.87) * mm, v(-54.25, 56.81) * mm, v(-50.36, 57.25) * mm]});
            skFitSpline(sketch, "E1111", {"points": [v(-50.36, 57.25) * mm, v(-48.9, 57.42) * mm, v(-43.47, 58.08) * mm, v(-38.26, 58.73) * mm]});
            skFitSpline(sketch, "E1112", {"points": [v(-38.26, 58.73) * mm, v(-33.06, 59.38) * mm, v(-28.76, 59.86) * mm, v(-28.7, 59.8) * mm]});
            skFitSpline(sketch, "E1113", {"points": [v(-28.7, 59.8) * mm, v(-28.58, 59.7) * mm, v(-31.4, 43.74) * mm, v(-31.72, 42.68) * mm]});
            skFitSpline(sketch, "E1114", {"points": [v(-31.72, 42.68) * mm, v(-31.87, 42.17) * mm, v(-32.43, 42.5) * mm, v(-40.64, 47.92) * mm]});
            skFitSpline(sketch, "E1115", {"points": [v(-128.12, 45.33) * mm, v(-128.93, 47.77) * mm, v(-131.29, 56.47) * mm, v(-131.17, 56.58) * mm]});
            skFitSpline(sketch, "E1116", {"points": [v(-131.17, 56.58) * mm, v(-131.08, 56.67) * mm, v(-128.94, 56.68) * mm, v(-126.42, 56.6) * mm]});
            skFitSpline(sketch, "E1117", {"points": [v(-121, 50.79) * mm, v(-121.37, 50.46) * mm, v(-122.58, 49.43) * mm, v(-123.69, 48.5) * mm]});
            skFitSpline(sketch, "E1118", {"points": [v(-123.69, 48.5) * mm, v(-124.8, 47.58) * mm, v(-126.15, 46.42) * mm, v(-126.7, 45.93) * mm]});
            skFitSpline(sketch, "E1119", {"points": [v(-126.7, 45.93) * mm, v(-127.78, 44.95) * mm, v(-127.96, 44.87) * mm, v(-128.12, 45.33) * mm]});
            skFitSpline(sketch, "E1120", {"points": [v(-87.2, 50.9) * mm, v(-87.2, 50.96) * mm, v(-85.55, 53.22) * mm, v(-83.54, 55.91) * mm]});
            skFitSpline(sketch, "E1121", {"points": [v(-83.54, 55.91) * mm, v(-81.53, 58.6) * mm, v(-76.7, 65.1) * mm, v(-72.8, 70.33) * mm]});
            skFitSpline(sketch, "E1122", {"points": [v(-72.8, 70.33) * mm, v(-66.22, 79.19) * mm, v(-65.72, 79.8) * mm, v(-65.65, 79.06) * mm]});
            skFitSpline(sketch, "E1123", {"points": [v(-65.65, 79.06) * mm, v(-65.6, 78.62) * mm, v(-65.34, 74.5) * mm, v(-65.04, 69.9) * mm]});
            skFitSpline(sketch, "E1124", {"points": [v(-65.41, 61.08) * mm, v(-66.53, 60.5) * mm, v(-84.2, 52.14) * mm, v(-85.94, 51.36) * mm]});
            skFitSpline(sketch, "E1125", {"points": [v(-85.94, 51.36) * mm, v(-86.63, 51.05) * mm, v(-87.2, 50.84) * mm, v(-87.2, 50.9) * mm]});
            skFitSpline(sketch, "E1126", {"points": [v(77.2, 54.67) * mm, v(74.1, 55.73) * mm, v(71.53, 56.63) * mm, v(71.5, 56.66) * mm]});
            skFitSpline(sketch, "E1127", {"points": [v(71.5, 56.66) * mm, v(71.47, 56.68) * mm, v(72.1, 59.24) * mm, v(72.89, 62.33) * mm]});
            skFitSpline(sketch, "E1128", {"points": [v(72.89, 62.33) * mm, v(73.69, 65.42) * mm, v(75.1, 70.92) * mm, v(76.03, 74.55) * mm]});
            skFitSpline(sketch, "E1129", {"points": [v(76.03, 74.55) * mm, v(76.96, 78.18) * mm, v(77.8, 81.22) * mm, v(77.88, 81.3) * mm]});
            skFitSpline(sketch, "E1130", {"points": [v(77.88, 81.3) * mm, v(78.03, 81.45) * mm, v(98.3, 78.25) * mm, v(98.5, 78.05) * mm]});
            skFitSpline(sketch, "E1131", {"points": [v(98.5, 78.05) * mm, v(98.61, 77.93) * mm, v(83.13, 52.7) * mm, v(82.96, 52.72) * mm]});
            skFitSpline(sketch, "E1132", {"points": [v(82.96, 52.72) * mm, v(82.9, 52.73) * mm, v(80.3, 53.6) * mm, v(77.2, 54.67) * mm]});
            skFitSpline(sketch, "E1133", {"points": [v(10.04, 55.14) * mm, v(9.83, 55.8) * mm, v(7.24, 64.68) * mm, v(2.3, 81.74) * mm]});
            skFitSpline(sketch, "E1134", {"points": [v(2.3, 81.74) * mm, v(1.85, 83.26) * mm, v(1.85, 83.28) * mm, v(2.3, 82.82) * mm]});
            skFitSpline(sketch, "E1135", {"points": [v(2.3, 82.82) * mm, v(2.55, 82.56) * mm, v(8.17, 76.2) * mm, v(14.79, 68.67) * mm]});
            skFitSpline(sketch, "E1136", {"points": [v(24.11, 54.84) * mm, v(22.62, 54.75) * mm, v(18.9, 54.6) * mm, v(15.85, 54.5) * mm]});
            skFitSpline(sketch, "E1137", {"points": [v(-105.56, 57.02) * mm, v(-106.75, 57.26) * mm, v(-108.77, 57.64) * mm, v(-110.06, 57.87) * mm]});
            skFitSpline(sketch, "E1138", {"points": [v(-110.06, 57.87) * mm, v(-111.35, 58.1) * mm, v(-112.4, 58.38) * mm, v(-112.4, 58.5) * mm]});
            skFitSpline(sketch, "E1139", {"points": [v(-112.4, 58.5) * mm, v(-112.4, 58.9) * mm, v(-105.8, 68.05) * mm, v(-105.65, 67.87) * mm]});
            skFitSpline(sketch, "E1140", {"points": [v(-105.65, 67.87) * mm, v(-105.57, 67.78) * mm, v(-104.83, 65.39) * mm, v(-104.02, 62.55) * mm]});
            skFitSpline(sketch, "E1141", {"points": [v(-104.02, 62.55) * mm, v(-103.2, 59.7) * mm, v(-102.48, 57.2) * mm, v(-102.41, 56.97) * mm]});
            skFitSpline(sketch, "E1142", {"points": [v(-102.41, 56.97) * mm, v(-102.26, 56.44) * mm, v(-102.64, 56.45) * mm, v(-105.56, 57.02) * mm]});
            skFitSpline(sketch, "E1143", {"points": [v(105.46, 59.5) * mm, v(102.58, 60.7) * mm, v(100.26, 61.77) * mm, v(100.3, 61.87) * mm]});
            skFitSpline(sketch, "E1144", {"points": [v(100.3, 61.87) * mm, v(100.33, 61.97) * mm, v(102.36, 63.9) * mm, v(104.8, 66.14) * mm]});
            skFitSpline(sketch, "E1145", {"points": [v(104.8, 66.14) * mm, v(108.39, 69.44) * mm, v(109.27, 70.14) * mm, v(109.4, 69.8) * mm]});
            skFitSpline(sketch, "E1146", {"points": [v(109.4, 69.8) * mm, v(109.5, 69.58) * mm, v(109.9, 66.85) * mm, v(110.32, 63.75) * mm]});
            skFitSpline(sketch, "E1147", {"points": [v(110.32, 63.75) * mm, v(110.73, 60.65) * mm, v(111.13, 57.92) * mm, v(111.2, 57.69) * mm]});
            skFitSpline(sketch, "E1148", {"points": [v(111.2, 57.69) * mm, v(111.26, 57.43) * mm, v(111.19, 57.28) * mm, v(111, 57.3) * mm]});
            skFitSpline(sketch, "E1149", {"points": [v(111, 57.3) * mm, v(110.82, 57.3) * mm, v(108.33, 58.3) * mm, v(105.46, 59.5) * mm]});
            skFitSpline(sketch, "E1150", {"points": [v(57.64, 60.26) * mm, v(57.37, 60.43) * mm, v(51.7, 63.9) * mm, v(45.04, 67.95) * mm]});
            skFitSpline(sketch, "E1151", {"points": [v(45.04, 67.95) * mm, v(38.37, 72) * mm, v(31.73, 76.06) * mm, v(30.28, 76.95) * mm]});
            skFitSpline(sketch, "E1152", {"points": [v(30.28, 76.95) * mm, v(28.83, 77.84) * mm, v(25.62, 79.8) * mm, v(23.16, 81.3) * mm]});
            skFitSpline(sketch, "E1153", {"points": [v(23.16, 81.3) * mm, v(20.7, 82.8) * mm, v(18.71, 84.06) * mm, v(18.75, 84.1) * mm]});
            skFitSpline(sketch, "E1154", {"points": [v(18.75, 84.1) * mm, v(18.85, 84.2) * mm, v(64.8, 83.16) * mm, v(64.91, 83.06) * mm]});
            skFitSpline(sketch, "E1155", {"points": [v(64.91, 83.06) * mm, v(64.96, 83.02) * mm, v(63.74, 78.53) * mm, v(62.2, 73.07) * mm]});
            skFitSpline(sketch, "E1156", {"points": [v(62.2, 73.07) * mm, v(58.65, 60.43) * mm, v(58.5, 59.9) * mm, v(58.29, 59.92) * mm]});
            skFitSpline(sketch, "E1157", {"points": [v(58.29, 59.92) * mm, v(58.2, 59.93) * mm, v(57.9, 60.08) * mm, v(57.64, 60.26) * mm]});
            skFitSpline(sketch, "E1158", {"points": [v(-135.42, 66.57) * mm, v(-138.31, 78.8) * mm, v(-141.39, 92.2) * mm, v(-141.32, 92.26) * mm]});
            skFitSpline(sketch, "E1159", {"points": [v(-141.32, 92.26) * mm, v(-141.23, 92.36) * mm, v(-112.23, 83.25) * mm, v(-111.7, 82.96) * mm]});
            skFitSpline(sketch, "E1160", {"points": [v(-111.7, 82.96) * mm, v(-111.48, 82.83) * mm, v(-112.18, 82.18) * mm, v(-114.1, 80.76) * mm]});
            skFitSpline(sketch, "E1161", {"points": [v(-114.1, 80.76) * mm, v(-131.26, 68.1) * mm, v(-134.9, 65.43) * mm, v(-135.06, 65.43) * mm]});
            skFitSpline(sketch, "E1162", {"points": [v(-135.06, 65.43) * mm, v(-135.11, 65.43) * mm, v(-135.27, 65.94) * mm, v(-135.42, 66.57) * mm]});
            skFitSpline(sketch, "E1163", {"points": [v(-87.8, 68.5) * mm, v(-88.46, 69.51) * mm, v(-90.76, 73.03) * mm, v(-92.92, 76.3) * mm]});
            skFitSpline(sketch, "E1164", {"points": [v(-92.92, 76.3) * mm, v(-95.07, 79.59) * mm, v(-96.8, 82.32) * mm, v(-96.73, 82.37) * mm]});
            skFitSpline(sketch, "E1165", {"points": [v(-96.73, 82.37) * mm, v(-96.56, 82.55) * mm, v(-76.65, 81.34) * mm, v(-76.44, 81.14) * mm]});
            skFitSpline(sketch, "E1166", {"points": [v(-76.44, 81.14) * mm, v(-76.38, 81.08) * mm, v(-85, 68.75) * mm, v(-86.29, 67.05) * mm]});
            skFitSpline(sketch, "E1167", {"points": [v(-86.29, 67.05) * mm, v(-86.57, 66.68) * mm, v(-86.72, 66.82) * mm, v(-87.8, 68.5) * mm]});
            skFitSpline(sketch, "E1168", {"points": [v(-40.24, 67.4) * mm, v(-39.58, 68.47) * mm, v(-25.47, 87.05) * mm, v(-25.38, 86.97) * mm]});
            skFitSpline(sketch, "E1169", {"points": [v(-25.38, 86.97) * mm, v(-25.33, 86.91) * mm, v(-25.28, 82.8) * mm, v(-25.28, 77.83) * mm]});
            skFitSpline(sketch, "E1170", {"points": [v(-26, 68.79) * mm, v(-26.73, 68.79) * mm, v(-38.2, 67.47) * mm, v(-39.64, 67.22) * mm]});
            skFitSpline(sketch, "E1171", {"points": [v(-39.64, 67.22) * mm, v(-40.27, 67.1) * mm, v(-40.4, 67.15) * mm, v(-40.24, 67.4) * mm]});
            skFitSpline(sketch, "E1172", {"points": [v(123.52, 76.74) * mm, v(115.27, 80.98) * mm, v(108.44, 84.52) * mm, v(108.34, 84.6) * mm]});
            skFitSpline(sketch, "E1173", {"points": [v(108.34, 84.6) * mm, v(108.24, 84.7) * mm, v(115.73, 86.64) * mm, v(124.98, 88.92) * mm]});
            skFitSpline(sketch, "E1174", {"points": [v(124.98, 88.92) * mm, v(134.22, 91.2) * mm, v(141.85, 93.02) * mm, v(141.91, 92.95) * mm]});
            skFitSpline(sketch, "E1175", {"points": [v(141.91, 92.95) * mm, v(142.03, 92.84) * mm, v(139.28, 70.91) * mm, v(138.99, 69.57) * mm]});
            skFitSpline(sketch, "E1176", {"points": [v(138.99, 69.57) * mm, v(138.92, 69.27) * mm, v(138.8, 69.03) * mm, v(138.7, 69.03) * mm]});
            skFitSpline(sketch, "E1177", {"points": [v(138.7, 69.03) * mm, v(138.6, 69.03) * mm, v(131.77, 72.5) * mm, v(123.52, 76.74) * mm]});
            skFitSpline(sketch, "E1178", {"points": [v(-54.37, 73) * mm, v(-54.43, 73.05) * mm, v(-54.34, 74.37) * mm, v(-54.18, 75.92) * mm]});
            skFitSpline(sketch, "E1179", {"points": [v(-54.18, 75.92) * mm, v(-54.02, 77.48) * mm, v(-53.32, 84.53) * mm, v(-52.63, 91.59) * mm]});
            skFitSpline(sketch, "E1180", {"points": [v(-52.63, 91.59) * mm, v(-51.94, 98.65) * mm, v(-51.3, 104.52) * mm, v(-51.2, 104.63) * mm]});
            skFitSpline(sketch, "E1181", {"points": [v(-51.2, 104.63) * mm, v(-51.05, 104.79) * mm, v(-22.74, 98.93) * mm, v(-22.46, 98.68) * mm]});
            skFitSpline(sketch, "E1182", {"points": [v(-22.46, 98.68) * mm, v(-22.41, 98.64) * mm, v(-52.91, 73.85) * mm, v(-53.85, 73.18) * mm]});
            skFitSpline(sketch, "E1183", {"points": [v(-53.85, 73.18) * mm, v(-54.08, 73.02) * mm, v(-54.3, 72.93) * mm, v(-54.37, 73) * mm]});
            skFitSpline(sketch, "E1184", {"points": [v(-110.24, 91.55) * mm, v(-110.24, 91.9) * mm, v(-106.4, 107.76) * mm, v(-106.22, 108.2) * mm]});
            skFitSpline(sketch, "E1185", {"points": [v(-106.22, 108.2) * mm, v(-106.07, 108.55) * mm, v(-104.69, 107.73) * mm, v(-97.57, 103.07) * mm]});
            skFitSpline(sketch, "E1186", {"points": [v(-97.57, 103.07) * mm, v(-92.92, 100.02) * mm, v(-89.15, 97.48) * mm, v(-89.2, 97.44) * mm]});
            skFitSpline(sketch, "E1187", {"points": [v(-89.2, 97.44) * mm, v(-89.29, 97.34) * mm, v(-109.9, 91.35) * mm, v(-110.11, 91.35) * mm]});
            skFitSpline(sketch, "E1188", {"points": [v(-110.11, 91.35) * mm, v(-110.18, 91.35) * mm, v(-110.24, 91.44) * mm, v(-110.24, 91.55) * mm]});
            skFitSpline(sketch, "E1189", {"points": [v(-73.7, 94.94) * mm, v(-80.47, 96.62) * mm, v(-86.07, 98.06) * mm, v(-86.15, 98.13) * mm]});
            skFitSpline(sketch, "E1190", {"points": [v(-86.15, 98.13) * mm, v(-86.25, 98.24) * mm, v(-56.83, 108.15) * mm, v(-56.4, 108.15) * mm]});
            skFitSpline(sketch, "E1191", {"points": [v(-56.4, 108.15) * mm, v(-56.34, 108.15) * mm, v(-57.22, 104.48) * mm, v(-58.36, 99.99) * mm]});
            skFitSpline(sketch, "E1192", {"points": [v(-58.36, 99.99) * mm, v(-60.24, 92.6) * mm, v(-60.48, 91.83) * mm, v(-60.92, 91.85) * mm]});
            skFitSpline(sketch, "E1193", {"points": [v(-60.92, 91.85) * mm, v(-61.18, 91.87) * mm, v(-66.94, 93.25) * mm, v(-73.7, 94.94) * mm]});
            skFitSpline(sketch, "E1194", {"points": [v(54.94, 98.27) * mm, v(46.46, 100.2) * mm, v(39.52, 101.83) * mm, v(39.52, 101.9) * mm]});
            skFitSpline(sketch, "E1195", {"points": [v(39.52, 101.9) * mm, v(39.52, 102.05) * mm, v(70.25, 104.86) * mm, v(70.38, 104.72) * mm]});
            skFitSpline(sketch, "E1196", {"points": [v(70.38, 104.72) * mm, v(70.43, 104.67) * mm, v(70.64, 102.75) * mm, v(70.83, 100.45) * mm]});
            skFitSpline(sketch, "E1197", {"points": [v(70.83, 100.45) * mm, v(71.03, 98.15) * mm, v(71.24, 95.92) * mm, v(71.3, 95.49) * mm]});
            skFitSpline(sketch, "E1198", {"points": [v(71.3, 95.49) * mm, v(71.4, 94.8) * mm, v(71.34, 94.71) * mm, v(70.88, 94.73) * mm]});
            skFitSpline(sketch, "E1199", {"points": [v(70.88, 94.73) * mm, v(70.6, 94.75) * mm, v(63.42, 96.34) * mm, v(54.94, 98.27) * mm]});
            skFitSpline(sketch, "E1200", {"points": [v(7.41, 96.2) * mm, v(7.47, 96.37) * mm, v(9.4, 101.88) * mm, v(11.7, 108.45) * mm]});
            skFitSpline(sketch, "E1201", {"points": [v(11.7, 108.45) * mm, v(14, 115.01) * mm, v(15.93, 120.39) * mm, v(16, 120.39) * mm]});
            skFitSpline(sketch, "E1202", {"points": [v(16, 120.39) * mm, v(16.12, 120.39) * mm, v(30.7, 104.6) * mm, v(34.58, 100.3) * mm]});
            skFitSpline(sketch, "E1203", {"points": [v(34.9, 98.92) * mm, v(33.97, 98.76) * mm, v(8.1, 95.9) * mm, v(7.63, 95.9) * mm]});
            skFitSpline(sketch, "E1204", {"points": [v(7.63, 95.9) * mm, v(7.45, 95.9) * mm, v(7.36, 96.04) * mm, v(7.41, 96.2) * mm]});
            skFitSpline(sketch, "E1205", {"points": [v(113, 102.09) * mm, v(113.07, 104.03) * mm, v(113.16, 106.01) * mm, v(113.17, 106.49) * mm]});
            skFitSpline(sketch, "E1206", {"points": [v(118.16, 106.43) * mm, v(120.89, 105.92) * mm, v(123.16, 105.47) * mm, v(123.2, 105.42) * mm]});
            skFitSpline(sketch, "E1207", {"points": [v(123.2, 105.42) * mm, v(123.28, 105.34) * mm, v(113.1, 98.55) * mm, v(112.92, 98.55) * mm]});
            skFitSpline(sketch, "E1208", {"points": [v(112.92, 98.55) * mm, v(112.87, 98.55) * mm, v(112.9, 100.14) * mm, v(113, 102.09) * mm]});
            skFitSpline(sketch, "E1209", {"points": [v(-131.95, 101.33) * mm, v(-134.2, 102.19) * mm, v(-136.06, 102.93) * mm, v(-136.1, 102.97) * mm]});
            skFitSpline(sketch, "E1210", {"points": [v(-136.1, 102.97) * mm, v(-136.24, 103.1) * mm, v(-129.6, 116.55) * mm, v(-129.4, 116.55) * mm]});
            skFitSpline(sketch, "E1211", {"points": [v(-129.4, 116.55) * mm, v(-128.74, 116.55) * mm, v(-114.56, 111.38) * mm, v(-114.63, 111.17) * mm]});
            skFitSpline(sketch, "E1212", {"points": [v(-114.63, 111.17) * mm, v(-114.76, 110.77) * mm, v(-127.3, 99.75) * mm, v(-127.6, 99.76) * mm]});
            skFitSpline(sketch, "E1213", {"points": [v(-127.6, 99.76) * mm, v(-127.76, 99.76) * mm, v(-129.71, 100.47) * mm, v(-131.95, 101.33) * mm]});
            skFitSpline(sketch, "E1214", {"points": [v(-15.56, 109.84) * mm, v(-22.92, 112.86) * mm, v(-26.58, 114.47) * mm, v(-26.52, 114.68) * mm]});
            skFitSpline(sketch, "E1215", {"points": [v(-26.52, 114.68) * mm, v(-26.48, 114.85) * mm, v(-25.93, 115.9) * mm, v(-25.3, 117.03) * mm]});
            skFitSpline(sketch, "E1216", {"points": [v(-25.3, 117.03) * mm, v(-24.66, 118.15) * mm, v(-22.11, 122.78) * mm, v(-19.63, 127.32) * mm]});
            skFitSpline(sketch, "E1217", {"points": [v(-19.63, 127.32) * mm, v(-15.68, 134.54) * mm, v(-15.09, 135.5) * mm, v(-14.9, 135) * mm]});
            skFitSpline(sketch, "E1218", {"points": [v(-14.9, 135) * mm, v(-14.78, 134.68) * mm, v(-12.43, 128.16) * mm, v(-9.68, 120.5) * mm]});
            skFitSpline(sketch, "E1219", {"points": [v(-9.68, 120.5) * mm, v(-6.93, 112.85) * mm, v(-4.56, 106.3) * mm, v(-4.43, 105.93) * mm]});
            skFitSpline(sketch, "E1220", {"points": [v(-4.43, 105.93) * mm, v(-4.29, 105.56) * mm, v(-4.25, 105.28) * mm, v(-4.35, 105.3) * mm]});
            skFitSpline(sketch, "E1221", {"points": [v(-4.35, 105.3) * mm, v(-4.44, 105.3) * mm, v(-9.49, 107.35) * mm, v(-15.56, 109.84) * mm]});
            skFitSpline(sketch, "E1222", {"points": [v(34.8, 113.13) * mm, v(34.1, 114.63) * mm, v(33.52, 115.9) * mm, v(33.52, 115.94) * mm]});
            skFitSpline(sketch, "E1223", {"points": [v(33.52, 115.94) * mm, v(33.52, 115.98) * mm, v(33.98, 116.18) * mm, v(34.54, 116.38) * mm]});
            skFitSpline(sketch, "E1224", {"points": [v(34.54, 116.38) * mm, v(35.1, 116.58) * mm, v(39.01, 118.05) * mm, v(43.24, 119.66) * mm]});
            skFitSpline(sketch, "E1225", {"points": [v(43.24, 119.66) * mm, v(70.68, 130.09) * mm, v(80.16, 133.6) * mm, v(80.32, 133.43) * mm]});
            skFitSpline(sketch, "E1226", {"points": [v(80.32, 133.43) * mm, v(80.42, 133.32) * mm, v(80.67, 132.26) * mm, v(80.88, 131.07) * mm]});
            skFitSpline(sketch, "E1227", {"points": [v(80.88, 131.07) * mm, v(82.88, 119.63) * mm, v(83.47, 116.02) * mm, v(83.38, 115.93) * mm]});
            skFitSpline(sketch, "E1228", {"points": [v(83.38, 115.93) * mm, v(83.25, 115.8) * mm, v(81.52, 115.58) * mm, v(73, 114.62) * mm]});
            skFitSpline(sketch, "E1229", {"points": [v(73, 114.62) * mm, v(69.43, 114.22) * mm, v(64.2, 113.62) * mm, v(61.36, 113.3) * mm]});
            skFitSpline(sketch, "E1230", {"points": [v(61.36, 113.3) * mm, v(58.52, 112.96) * mm, v(53.82, 112.42) * mm, v(50.92, 112.1) * mm]});
            skFitSpline(sketch, "E1231", {"points": [v(50.92, 112.1) * mm, v(48.01, 111.77) * mm, v(43.5, 111.25) * mm, v(40.87, 110.95) * mm]});
            skFitSpline(sketch, "E1232", {"points": [v(137.32, 114.55) * mm, v(137.05, 114.6) * mm, v(135.97, 114.85) * mm, v(134.92, 115.1) * mm]});
            skFitSpline(sketch, "E1233", {"points": [v(134.92, 115.1) * mm, v(133.86, 115.36) * mm, v(132.3, 115.72) * mm, v(131.44, 115.92) * mm]});
            skFitSpline(sketch, "E1234", {"points": [v(131.44, 115.92) * mm, v(127.32, 116.87) * mm, v(122.39, 118.03) * mm, v(120.02, 118.59) * mm]});
            skFitSpline(sketch, "E1235", {"points": [v(120.02, 118.59) * mm, v(118.58, 118.93) * mm, v(116.75, 119.36) * mm, v(115.96, 119.55) * mm]});
            skFitSpline(sketch, "E1236", {"points": [v(115.96, 119.55) * mm, v(115.17, 119.73) * mm, v(113.73, 120.07) * mm, v(112.77, 120.29) * mm]});
            skFitSpline(sketch, "E1237", {"points": [v(112.77, 120.29) * mm, v(111.81, 120.51) * mm, v(110.97, 120.78) * mm, v(110.9, 120.9) * mm]});
            skFitSpline(sketch, "E1238", {"points": [v(110.9, 120.9) * mm, v(110.84, 121) * mm, v(113.35, 124.51) * mm, v(116.5, 128.7) * mm]});
            skFitSpline(sketch, "E1239", {"points": [v(116.5, 128.7) * mm, v(119.63, 132.88) * mm, v(123.05, 137.44) * mm, v(124.1, 138.84) * mm]});
            skFitSpline(sketch, "E1240", {"points": [v(126.4, 140.42) * mm, v(126.88, 139.3) * mm, v(137.31, 116.52) * mm, v(137.82, 115.5) * mm]});
            skFitSpline(sketch, "E1241", {"points": [v(137.82, 115.5) * mm, v(138, 115.1) * mm, v(138.16, 114.7) * mm, v(138.16, 114.6) * mm]});
            skFitSpline(sketch, "E1242", {"points": [v(138.16, 114.6) * mm, v(138.16, 114.38) * mm, v(138.1, 114.38) * mm, v(137.32, 114.55) * mm]});
            skFitSpline(sketch, "E1243", {"points": [v(-50.72, 120.44) * mm, v(-52.37, 120.96) * mm, v(-55.34, 121.9) * mm, v(-57.32, 122.54) * mm]});
            skFitSpline(sketch, "E1244", {"points": [v(-57.32, 122.54) * mm, v(-59.3, 123.17) * mm, v(-62.06, 124.04) * mm, v(-63.44, 124.47) * mm]});
            skFitSpline(sketch, "E1245", {"points": [v(-63.44, 124.47) * mm, v(-64.83, 124.9) * mm, v(-67.58, 125.77) * mm, v(-69.56, 126.4) * mm]});
            skFitSpline(sketch, "E1246", {"points": [v(-69.56, 126.4) * mm, v(-71.54, 127.04) * mm, v(-74.67, 128.02) * mm, v(-76.52, 128.58) * mm]});
            skFitSpline(sketch, "E1247", {"points": [v(-76.52, 128.58) * mm, v(-78.37, 129.14) * mm, v(-79.97, 129.67) * mm, v(-80.07, 129.75) * mm]});
            skFitSpline(sketch, "E1248", {"points": [v(-80.07, 129.75) * mm, v(-80.22, 129.88) * mm, v(-77.92, 136.7) * mm, v(-77.12, 138.5) * mm]});
            skFitSpline(sketch, "E1249", {"points": [v(-77.12, 138.5) * mm, v(-77, 138.77) * mm, v(-76.75, 139.47) * mm, v(-76.55, 140.07) * mm]});
            skFitSpline(sketch, "E1250", {"points": [v(-76.55, 140.07) * mm, v(-75.99, 141.8) * mm, v(-73.28, 149.23) * mm, v(-73.1, 149.57) * mm]});
            skFitSpline(sketch, "E1251", {"points": [v(-73.1, 149.57) * mm, v(-72.97, 149.8) * mm, v(-71.16, 148.4) * mm, v(-67.04, 144.93) * mm]});
            skFitSpline(sketch, "E1252", {"points": [v(-67.04, 144.93) * mm, v(-60.37, 139.3) * mm, v(-54.74, 134.57) * mm, v(-49.97, 130.56) * mm]});
            skFitSpline(sketch, "E1253", {"points": [v(-49.97, 130.56) * mm, v(-47.67, 128.63) * mm, v(-46.72, 127.69) * mm, v(-46.79, 127.4) * mm]});
            skFitSpline(sketch, "E1254", {"points": [v(-46.79, 127.4) * mm, v(-46.84, 127.17) * mm, v(-47.04, 125.32) * mm, v(-47.24, 123.3) * mm]});
            skFitSpline(sketch, "E1255", {"points": [v(-47.24, 123.3) * mm, v(-47.43, 121.26) * mm, v(-47.62, 119.57) * mm, v(-47.66, 119.54) * mm]});
            skFitSpline(sketch, "E1256", {"points": [v(-47.66, 119.54) * mm, v(-47.7, 119.51) * mm, v(-49.07, 119.92) * mm, v(-50.72, 120.44) * mm]});
            skFitSpline(sketch, "E1257", {"points": [v(1.57, 126.76) * mm, v(1.56, 129) * mm, v(1.48, 139.09) * mm, v(1.38, 149.19) * mm]});
            skFitSpline(sketch, "E1258", {"points": [v(1.38, 149.19) * mm, v(1.3, 159.29) * mm, v(1.24, 167.58) * mm, v(1.26, 167.62) * mm]});
            skFitSpline(sketch, "E1259", {"points": [v(1.26, 167.62) * mm, v(1.29, 167.67) * mm, v(8.08, 165.47) * mm, v(16.35, 162.74) * mm]});
            skFitSpline(sketch, "E1260", {"points": [v(16.35, 162.74) * mm, v(30.1, 158.2) * mm, v(31.37, 157.75) * mm, v(31.06, 157.39) * mm]});
            skFitSpline(sketch, "E1261", {"points": [v(31.06, 157.39) * mm, v(29.5, 155.52) * mm, v(22.3, 147.03) * mm, v(21.16, 145.7) * mm]});
            skFitSpline(sketch, "E1262", {"points": [v(21.16, 145.7) * mm, v(20.37, 144.77) * mm, v(18.58, 142.66) * mm, v(17.19, 141.02) * mm]});
            skFitSpline(sketch, "E1263", {"points": [v(17.19, 141.02) * mm, v(4.6, 126.17) * mm, v(2.21, 123.34) * mm, v(1.93, 123.04) * mm]});
            skFitSpline(sketch, "E1264", {"points": [v(1.93, 123.04) * mm, v(1.65, 122.74) * mm, v(1.6, 123.3) * mm, v(1.57, 126.76) * mm]});
            skFitSpline(sketch, "E1265", {"points": [v(27.98, 125.25) * mm, v(27.97, 125.68) * mm, v(27.92, 126.24) * mm, v(27.87, 126.5) * mm]});
            skFitSpline(sketch, "E1266", {"points": [v(27.87, 126.5) * mm, v(27.82, 126.77) * mm, v(27.75, 128.56) * mm, v(27.7, 130.5) * mm]});
            skFitSpline(sketch, "E1267", {"points": [v(39.83, 146.75) * mm, v(46.54, 153.77) * mm, v(52.11, 159.5) * mm, v(52.22, 159.5) * mm]});
            skFitSpline(sketch, "E1268", {"points": [v(52.22, 159.5) * mm, v(52.33, 159.5) * mm, v(53.88, 155.21) * mm, v(55.67, 149.97) * mm]});
            skFitSpline(sketch, "E1269", {"points": [v(55.67, 149.97) * mm, v(57.46, 144.72) * mm, v(58.98, 140.27) * mm, v(59.05, 140.07) * mm]});
            skFitSpline(sketch, "E1270", {"points": [v(59.05, 140.07) * mm, v(59.15, 139.8) * mm, v(58.58, 139.41) * mm, v(56.85, 138.57) * mm]});
            skFitSpline(sketch, "E1271", {"points": [v(56.85, 138.57) * mm, v(55.57, 137.95) * mm, v(49.33, 134.89) * mm, v(43, 131.77) * mm]});
            skFitSpline(sketch, "E1272", {"points": [v(43, 131.77) * mm, v(28.22, 124.49) * mm, v(28.17, 124.47) * mm, v(28.08, 124.47) * mm]});
            skFitSpline(sketch, "E1273", {"points": [v(28.08, 124.47) * mm, v(28.03, 124.47) * mm, v(28, 124.82) * mm, v(27.98, 125.25) * mm]});
            skFitSpline(sketch, "E1274", {"points": [v(-130.6, 125.31) * mm, v(-132.88, 125.48) * mm, v(-134.8, 125.66) * mm, v(-134.86, 125.73) * mm]});
            skFitSpline(sketch, "E1275", {"points": [v(-134.86, 125.73) * mm, v(-134.97, 125.84) * mm, v(-134.48, 126.93) * mm, v(-131.54, 133.12) * mm]});
            skFitSpline(sketch, "E1276", {"points": [v(-126.33, 135.6) * mm, v(-124.2, 135.44) * mm, v(-122.39, 135.25) * mm, v(-122.32, 135.18) * mm]});
            skFitSpline(sketch, "E1277", {"points": [v(-122.32, 135.18) * mm, v(-122.25, 135.11) * mm, v(-122.6, 132.78) * mm, v(-123.12, 130) * mm]});
            skFitSpline(sketch, "E1278", {"points": [v(-125.24, 124.98) * mm, v(-125.9, 125) * mm, v(-128.31, 125.15) * mm, v(-130.6, 125.31) * mm]});
            skFitSpline(sketch, "E1279", {"points": [v(-100.24, 126.76) * mm, v(-104.58, 127.06) * mm, v(-108.16, 127.34) * mm, v(-108.2, 127.39) * mm]});
            skFitSpline(sketch, "E1280", {"points": [v(-108.2, 127.39) * mm, v(-108.33, 127.53) * mm, v(-102.43, 140.36) * mm, v(-102.24, 140.34) * mm]});
            skFitSpline(sketch, "E1281", {"points": [v(-102.24, 140.34) * mm, v(-102.06, 140.32) * mm, v(-90.08, 126.44) * mm, v(-90.08, 126.25) * mm]});
            skFitSpline(sketch, "E1282", {"points": [v(-90.08, 126.25) * mm, v(-90.08, 126.09) * mm, v(-91.83, 126.18) * mm, v(-100.24, 126.76) * mm]});
            skFitSpline(sketch, "E1283", {"points": [v(-49.16, 139.25) * mm, v(-59.92, 151.47) * mm, v(-59.7, 151.2) * mm, v(-59.41, 151.3) * mm]});
            skFitSpline(sketch, "E1284", {"points": [v(-59.41, 151.3) * mm, v(-59.2, 151.36) * mm, v(-25.25, 145.39) * mm, v(-25.11, 145.26) * mm]});
            skFitSpline(sketch, "E1285", {"points": [v(-25.11, 145.26) * mm, v(-25.07, 145.22) * mm, v(-30.42, 140.16) * mm, v(-39.15, 131.98) * mm]});
            skFitSpline(sketch, "E1286", {"points": [v(-39.15, 131.98) * mm, v(-40.17, 131.02) * mm, v(-41.06, 130.25) * mm, v(-41.12, 130.25) * mm]});
            skFitSpline(sketch, "E1287", {"points": [v(-41.12, 130.25) * mm, v(-41.19, 130.25) * mm, v(-44.8, 134.3) * mm, v(-49.16, 139.25) * mm]});
            skFitSpline(sketch, "E1288", {"points": [v(100.53, 135.68) * mm, v(99.44, 138.53) * mm, v(98.58, 140.89) * mm, v(98.61, 140.92) * mm]});
            skFitSpline(sketch, "E1289", {"points": [v(98.61, 140.92) * mm, v(98.65, 140.96) * mm, v(100.03, 141.05) * mm, v(101.68, 141.13) * mm]});
            skFitSpline(sketch, "E1290", {"points": [v(101.68, 141.13) * mm, v(103.33, 141.22) * mm, v(105.22, 141.33) * mm, v(105.88, 141.39) * mm]});
            skFitSpline(sketch, "E1291", {"points": [v(105.88, 141.39) * mm, v(108.2, 141.59) * mm, v(114.64, 141.8) * mm, v(114.64, 141.69) * mm]});
            skFitSpline(sketch, "E1292", {"points": [v(114.64, 141.69) * mm, v(114.64, 141.56) * mm, v(103.16, 130.9) * mm, v(102.75, 130.66) * mm]});
            skFitSpline(sketch, "E1293", {"points": [v(102.75, 130.66) * mm, v(102.61, 130.57) * mm, v(101.7, 132.64) * mm, v(100.53, 135.68) * mm]});
            skFitSpline(sketch, "E1294", {"points": [v(72.32, 150.31) * mm, v(73.35, 150.23) * mm, v(76.5, 150.03) * mm, v(79.3, 149.87) * mm]});
            skFitSpline(sketch, "E1295", {"points": [v(79.3, 149.87) * mm, v(82.1, 149.7) * mm, v(84.39, 149.52) * mm, v(84.38, 149.44) * mm]});
            skFitSpline(sketch, "E1296", {"points": [v(84.38, 149.44) * mm, v(84.36, 149.3) * mm, v(75.55, 141.18) * mm, v(75.3, 141.09) * mm]});
            skFitSpline(sketch, "E1297", {"points": [v(75.3, 141.09) * mm, v(75.22, 141.05) * mm, v(74.1, 143.15) * mm, v(72.8, 145.74) * mm]});
            skFitSpline(sketch, "E1298", {"points": [v(-117.47, 147.34) * mm, v(-121.08, 150.05) * mm, v(-123.64, 151.93) * mm, v(-124.82, 152.76) * mm]});
            skFitSpline(sketch, "E1299", {"points": [v(-124.82, 152.76) * mm, v(-125.25, 153.06) * mm, v(-125.6, 153.38) * mm, v(-125.6, 153.48) * mm]});
            skFitSpline(sketch, "E1300", {"points": [v(-125.6, 153.48) * mm, v(-125.6, 153.58) * mm, v(-124.12, 154.62) * mm, v(-122.3, 155.8) * mm]});
            skFitSpline(sketch, "E1301", {"points": [v(-122.3, 155.8) * mm, v(-120.49, 156.98) * mm, v(-116.36, 159.7) * mm, v(-113.14, 161.84) * mm]});
            skFitSpline(sketch, "E1302", {"points": [v(-113.14, 161.84) * mm, v(-109.9, 163.98) * mm, v(-107.24, 165.7) * mm, v(-107.2, 165.67) * mm]});
            skFitSpline(sketch, "E1303", {"points": [v(-107.2, 165.67) * mm, v(-107.17, 165.64) * mm, v(-108.49, 161.5) * mm, v(-110.13, 156.5) * mm]});
            skFitSpline(sketch, "E1304", {"points": [v(-110.13, 156.5) * mm, v(-111.78, 151.49) * mm, v(-113.23, 147) * mm, v(-113.36, 146.54) * mm]});
            skFitSpline(sketch, "E1305", {"points": [v(-113.36, 146.54) * mm, v(-113.88, 144.66) * mm, v(-113.88, 144.66) * mm, v(-117.47, 147.34) * mm]});
            skFitSpline(sketch, "E1306", {"points": [v(116.44, 150.98) * mm, v(109.05, 151.8) * mm, v(102.78, 152.53) * mm, v(102.52, 152.6) * mm]});
            skFitSpline(sketch, "E1307", {"points": [v(102.52, 152.6) * mm, v(102.25, 152.65) * mm, v(106.95, 153.9) * mm, v(112.96, 155.39) * mm]});
            skFitSpline(sketch, "E1308", {"points": [v(112.96, 155.39) * mm, v(118.96, 156.87) * mm, v(124.06, 158.14) * mm, v(124.27, 158.2) * mm]});
            skFitSpline(sketch, "E1309", {"points": [v(124.27, 158.2) * mm, v(124.56, 158.3) * mm, v(125.49, 157.2) * mm, v(127.81, 154) * mm]});
            skFitSpline(sketch, "E1310", {"points": [v(127.81, 154) * mm, v(129.54, 151.62) * mm, v(130.96, 149.62) * mm, v(130.96, 149.55) * mm]});
            skFitSpline(sketch, "E1311", {"points": [v(130.96, 149.55) * mm, v(130.96, 149.36) * mm, v(130.6, 149.4) * mm, v(116.44, 150.98) * mm]});
            skFitSpline(sketch, "E1312", {"points": [v(-93.08, 157.84) * mm, v(-97.3, 160.1) * mm, v(-100.85, 162.02) * mm, v(-100.96, 162.13) * mm]});
            skFitSpline(sketch, "E1313", {"points": [v(-100.96, 162.13) * mm, v(-101.12, 162.3) * mm, v(-93.65, 167.62) * mm, v(-93.08, 167.75) * mm]});
            skFitSpline(sketch, "E1314", {"points": [v(-93.08, 167.75) * mm, v(-93, 167.77) * mm, v(-91.69, 165.52) * mm, v(-90.17, 162.75) * mm]});
            skFitSpline(sketch, "E1315", {"points": [v(-90.17, 162.75) * mm, v(-88.66, 159.98) * mm, v(-86.93, 156.82) * mm, v(-86.33, 155.73) * mm]});
            skFitSpline(sketch, "E1316", {"points": [v(-86.33, 155.73) * mm, v(-85.73, 154.64) * mm, v(-85.28, 153.75) * mm, v(-85.32, 153.75) * mm]});
            skFitSpline(sketch, "E1317", {"points": [v(-85.32, 153.75) * mm, v(-85.37, 153.75) * mm, v(-88.86, 155.6) * mm, v(-93.08, 157.84) * mm]});
            skFitSpline(sketch, "E1318", {"points": [v(-73.34, 179.01) * mm, v(-67.35, 185) * mm, v(-67.16, 185.18) * mm, v(-66.98, 184.53) * mm]});
            skFitSpline(sketch, "E1319", {"points": [v(-66.98, 184.53) * mm, v(-66.89, 184.17) * mm, v(-66.05, 178.14) * mm, v(-65.13, 171.15) * mm]});
            skFitSpline(sketch, "E1320", {"points": [v(-65.13, 171.15) * mm, v(-64.2, 164.15) * mm, v(-63.4, 158.18) * mm, v(-63.36, 157.89) * mm]});
            skFitSpline(sketch, "E1321", {"points": [v(-63.36, 157.89) * mm, v(-63.3, 157.6) * mm, v(-63.33, 157.35) * mm, v(-63.41, 157.36) * mm]});
            skFitSpline(sketch, "E1322", {"points": [v(-63.41, 157.36) * mm, v(-63.5, 157.37) * mm, v(-67.15, 160.85) * mm, v(-71.54, 165.1) * mm]});
            skFitSpline(sketch, "E1323", {"points": [v(72.05, 161.05) * mm, v(68.9, 161.87) * mm, v(66.27, 162.65) * mm, v(66.23, 162.77) * mm]});
            skFitSpline(sketch, "E1324", {"points": [v(66.23, 162.77) * mm, v(66.19, 162.9) * mm, v(67.46, 165.92) * mm, v(69.06, 169.48) * mm]});
            skFitSpline(sketch, "E1325", {"points": [v(69.06, 169.48) * mm, v(70.66, 173.04) * mm, v(72.07, 176.2) * mm, v(72.19, 176.52) * mm]});
            skFitSpline(sketch, "E1326", {"points": [v(72.19, 176.52) * mm, v(72.31, 176.84) * mm, v(72.47, 177.04) * mm, v(72.53, 176.97) * mm]});
            skFitSpline(sketch, "E1327", {"points": [v(72.53, 176.97) * mm, v(72.6, 176.9) * mm, v(73.94, 173.14) * mm, v(75.5, 168.6) * mm]});
            skFitSpline(sketch, "E1328", {"points": [v(75.5, 168.6) * mm, v(77.07, 164.06) * mm, v(78.43, 160.16) * mm, v(78.52, 159.93) * mm]});
            skFitSpline(sketch, "E1329", {"points": [v(78.52, 159.93) * mm, v(78.76, 159.33) * mm, v(78.6, 159.36) * mm, v(72.05, 161.05) * mm]});
            skFitSpline(sketch, "E1330", {"points": [v(-44.72, 162.48) * mm, v(-44.72, 162.65) * mm, v(-43.55, 166.02) * mm, v(-42.12, 169.97) * mm]});
            skFitSpline(sketch, "E1331", {"points": [v(-42.12, 169.97) * mm, v(-40.68, 173.92) * mm, v(-38.67, 179.5) * mm, v(-37.63, 182.37) * mm]});
            skFitSpline(sketch, "E1332", {"points": [v(-37.63, 182.37) * mm, v(-36.6, 185.24) * mm, v(-35.7, 187.59) * mm, v(-35.62, 187.59) * mm]});
            skFitSpline(sketch, "E1333", {"points": [v(-35.62, 187.59) * mm, v(-35.44, 187.59) * mm, v(-27.36, 163.35) * mm, v(-27.49, 163.22) * mm]});
            skFitSpline(sketch, "E1334", {"points": [v(-27.49, 163.22) * mm, v(-27.54, 163.17) * mm, v(-30.93, 162.96) * mm, v(-35.01, 162.76) * mm]});
            skFitSpline(sketch, "E1335", {"points": [v(-35.01, 162.76) * mm, v(-39.1, 162.56) * mm, v(-42.95, 162.34) * mm, v(-43.58, 162.28) * mm]});
            skFitSpline(sketch, "E1336", {"points": [v(-43.58, 162.28) * mm, v(-44.41, 162.2) * mm, v(-44.72, 162.25) * mm, v(-44.72, 162.48) * mm]});
            skFitSpline(sketch, "E1337", {"points": [v(109.77, 169.29) * mm, v(110.51, 170.44) * mm, v(111.73, 172.33) * mm, v(112.47, 173.48) * mm]});
            skFitSpline(sketch, "E1338", {"points": [v(53.1, 173.73) * mm, v(51.64, 178.55) * mm, v(51.61, 178.73) * mm, v(52.13, 179.1) * mm]});
            skFitSpline(sketch, "E1339", {"points": [v(52.13, 179.1) * mm, v(53.63, 180.21) * mm, v(58.08, 182.56) * mm, v(58.23, 182.33) * mm]});
            skFitSpline(sketch, "E1340", {"points": [v(58.23, 182.33) * mm, v(58.32, 182.18) * mm, v(58.6, 179.93) * mm, v(58.84, 177.32) * mm]});
            skFitSpline(sketch, "E1341", {"points": [v(58.84, 177.32) * mm, v(59.08, 174.72) * mm, v(59.29, 172.53) * mm, v(59.3, 172.47) * mm]});
            skFitSpline(sketch, "E1342", {"points": [v(59.3, 172.47) * mm, v(59.32, 172.34) * mm, v(55.5, 171.8) * mm, v(54.35, 171.77) * mm]});
            skFitSpline(sketch, "E1343", {"points": [v(54.35, 171.77) * mm, v(53.73, 171.75) * mm, v(53.66, 171.87) * mm, v(53.1, 173.73) * mm]});
            skFitSpline(sketch, "E1344", {"points": [v(26.97, 174.45) * mm, v(23.17, 175.52) * mm, v(20.1, 176.49) * mm, v(20.14, 176.6) * mm]});
            skFitSpline(sketch, "E1345", {"points": [v(20.14, 176.6) * mm, v(20.23, 176.9) * mm, v(42.5, 197.38) * mm, v(42.6, 197.29) * mm]});
            skFitSpline(sketch, "E1346", {"points": [v(42.6, 197.29) * mm, v(42.65, 197.25) * mm, v(41.04, 192.16) * mm, v(39.03, 185.98) * mm]});
            skFitSpline(sketch, "E1347", {"points": [v(39.03, 185.98) * mm, v(37.03, 179.8) * mm, v(35.23, 174.23) * mm, v(35.04, 173.6) * mm]});
            skFitSpline(sketch, "E1348", {"points": [v(35.04, 173.6) * mm, v(34.8, 172.8) * mm, v(34.58, 172.48) * mm, v(34.29, 172.5) * mm]});
            skFitSpline(sketch, "E1349", {"points": [v(34.29, 172.5) * mm, v(34.06, 172.5) * mm, v(30.77, 173.39) * mm, v(26.97, 174.45) * mm]});
            skFitSpline(sketch, "E1350", {"points": [v(-2.74, 176.4) * mm, v(-2.85, 176.5) * mm, v(-3.37, 176.53) * mm, v(-12.15, 177.17) * mm]});
            skFitSpline(sketch, "E1351", {"points": [v(-12.15, 177.17) * mm, v(-17.15, 177.54) * mm, v(-17.84, 177.64) * mm, v(-17.72, 177.97) * mm]});
            skFitSpline(sketch, "E1352", {"points": [v(-17.72, 177.97) * mm, v(-17.1, 179.57) * mm, v(-9.78, 195.75) * mm, v(-9.67, 195.75) * mm]});
            skFitSpline(sketch, "E1353", {"points": [v(-9.67, 195.75) * mm, v(-9.47, 195.75) * mm, v(-2.38, 176.57) * mm, v(-2.52, 176.42) * mm]});
            skFitSpline(sketch, "E1354", {"points": [v(-2.52, 176.42) * mm, v(-2.59, 176.36) * mm, v(-2.69, 176.35) * mm, v(-2.74, 176.4) * mm]});
            skFitSpline(sketch, "E1355", {"points": [v(83.37, 183.47) * mm, v(77.18, 190.32) * mm, v(77.74, 189.7) * mm, v(76.77, 190.74) * mm]});
            skFitSpline(sketch, "E1356", {"points": [v(77.08, 194.08) * mm, v(77.68, 195.46) * mm, v(79.38, 199.37) * mm, v(80.85, 202.77) * mm]});
            skFitSpline(sketch, "E1357", {"points": [v(80.85, 202.77) * mm, v(82.32, 206.18) * mm, v(83.6, 208.93) * mm, v(83.7, 208.9) * mm]});
            skFitSpline(sketch, "E1358", {"points": [v(83.7, 208.9) * mm, v(83.79, 208.86) * mm, v(84.94, 207.64) * mm, v(86.25, 206.19) * mm]});
            skFitSpline(sketch, "E1359", {"points": [v(86.25, 206.19) * mm, v(96.5, 194.86) * mm, v(98.34, 192.78) * mm, v(98.24, 192.53) * mm]});
            skFitSpline(sketch, "E1360", {"points": [v(98.24, 192.53) * mm, v(98.02, 191.97) * mm, v(88.93, 177.87) * mm, v(88.74, 177.8) * mm]});
            skFitSpline(sketch, "E1361", {"points": [v(88.74, 177.8) * mm, v(88.64, 177.76) * mm, v(86.22, 180.31) * mm, v(83.37, 183.47) * mm]});
            skFitSpline(sketch, "E1362", {"points": [v(-47.36, 181.86) * mm, v(-47.36, 181.93) * mm, v(-47.75, 183.06) * mm, v(-48.22, 184.37) * mm]});
            skFitSpline(sketch, "E1363", {"points": [v(-48.22, 184.37) * mm, v(-48.7, 185.68) * mm, v(-49.44, 187.77) * mm, v(-49.88, 189.03) * mm]});
            skFitSpline(sketch, "E1364", {"points": [v(-49.88, 189.03) * mm, v(-50.32, 190.28) * mm, v(-50.96, 192.06) * mm, v(-51.3, 192.99) * mm]});
            skFitSpline(sketch, "E1365", {"points": [v(-51.3, 192.99) * mm, v(-51.64, 193.91) * mm, v(-51.92, 194.83) * mm, v(-51.92, 195.04) * mm]});
            skFitSpline(sketch, "E1366", {"points": [v(-51.92, 195.04) * mm, v(-51.92, 195.26) * mm, v(-51, 195.88) * mm, v(-49.58, 196.63) * mm]});
            skFitSpline(sketch, "E1367", {"points": [v(-49.58, 196.63) * mm, v(-48.3, 197.3) * mm, v(-45.64, 198.68) * mm, v(-43.69, 199.7) * mm]});
            skFitSpline(sketch, "E1368", {"points": [v(-43.69, 199.7) * mm, v(-41.73, 200.72) * mm, v(-40.07, 201.5) * mm, v(-40, 201.42) * mm]});
            skFitSpline(sketch, "E1369", {"points": [v(-40, 201.42) * mm, v(-39.92, 201.35) * mm, v(-40.08, 200.71) * mm, v(-40.35, 200.02) * mm]});
            skFitSpline(sketch, "E1370", {"points": [v(-40.35, 200.02) * mm, v(-41.08, 198.1) * mm, v(-42.31, 194.82) * mm, v(-42.8, 193.47) * mm]});
            skFitSpline(sketch, "E1371", {"points": [v(-42.8, 193.47) * mm, v(-43.04, 192.8) * mm, v(-43.52, 191.51) * mm, v(-43.86, 190.59) * mm]});
            skFitSpline(sketch, "E1372", {"points": [v(-43.86, 190.59) * mm, v(-44.2, 189.66) * mm, v(-45.02, 187.4) * mm, v(-45.7, 185.55) * mm]});
            skFitSpline(sketch, "E1373", {"points": [v(-45.7, 185.55) * mm, v(-46.73, 182.71) * mm, v(-47.36, 181.3) * mm, v(-47.36, 181.86) * mm]});
            skFitSpline(sketch, "E1374", {"points": [v(-87.86, 188.37) * mm, v(-92.51, 190.36) * mm, v(-96.32, 192.07) * mm, v(-96.32, 192.17) * mm]});
            skFitSpline(sketch, "E1375", {"points": [v(-96.32, 192.17) * mm, v(-96.32, 192.36) * mm, v(-79.73, 205.35) * mm, v(-79.48, 205.35) * mm]});
            skFitSpline(sketch, "E1376", {"points": [v(-79.48, 205.35) * mm, v(-79.4, 205.35) * mm, v(-79.3, 203.65) * mm, v(-79.28, 201.57) * mm]});
            skFitSpline(sketch, "E1377", {"points": [v(-79.28, 201.57) * mm, v(-79.25, 199.49) * mm, v(-79.16, 194.84) * mm, v(-79.07, 191.25) * mm]});
            skFitSpline(sketch, "E1378", {"points": [v(-79.07, 191.25) * mm, v(-78.97, 186.94) * mm, v(-79, 184.71) * mm, v(-79.16, 184.73) * mm]});
            skFitSpline(sketch, "E1379", {"points": [v(-79.16, 184.73) * mm, v(-79.3, 184.74) * mm, v(-83.2, 186.38) * mm, v(-87.86, 188.37) * mm]});
            skFitSpline(sketch, "E1380", {"points": [v(2.11, 200.7) * mm, v(-0.7, 204.23) * mm, v(-3.06, 207.24) * mm, v(-3.11, 207.38) * mm]});
            skFitSpline(sketch, "E1381", {"points": [v(-3.11, 207.38) * mm, v(-3.18, 207.55) * mm, v(-1.49, 207.83) * mm, v(1.77, 208.2) * mm]});
            skFitSpline(sketch, "E1382", {"points": [v(1.77, 208.2) * mm, v(4.52, 208.5) * mm, v(7.03, 208.8) * mm, v(7.36, 208.87) * mm]});
            skFitSpline(sketch, "E1383", {"points": [v(7.67, 201.96) * mm, v(7.5, 198.1) * mm, v(7.35, 194.79) * mm, v(7.3, 194.6) * mm]});
            skFitSpline(sketch, "E1384", {"points": [v(7.3, 194.6) * mm, v(7.27, 194.41) * mm, v(4.93, 197.15) * mm, v(2.11, 200.7) * mm]});
            skFitSpline(sketch, "E1385", {"points": [v(25.82, 207.17) * mm, v(23.69, 211.51) * mm, v(21.54, 215.93) * mm, v(21.04, 216.99) * mm]});
            skFitSpline(sketch, "E1386", {"points": [v(21.04, 216.99) * mm, v(20.53, 218.04) * mm, v(18.77, 221.66) * mm, v(17.12, 225.02) * mm]});
            skFitSpline(sketch, "E1387", {"points": [v(17.12, 225.02) * mm, v(15.46, 228.39) * mm, v(14.15, 231.18) * mm, v(14.2, 231.23) * mm]});
            skFitSpline(sketch, "E1388", {"points": [v(14.2, 231.23) * mm, v(14.33, 231.36) * mm, v(39.12, 225.96) * mm, v(39.35, 225.76) * mm]});
            skFitSpline(sketch, "E1389", {"points": [v(39.35, 225.76) * mm, v(39.51, 225.6) * mm, v(38.28, 222.15) * mm, v(31.49, 203.8) * mm]});
            skFitSpline(sketch, "E1390", {"points": [v(31.49, 203.8) * mm, v(30.61, 201.43) * mm, v(29.85, 199.44) * mm, v(29.79, 199.38) * mm]});
            skFitSpline(sketch, "E1391", {"points": [v(29.79, 199.38) * mm, v(29.73, 199.32) * mm, v(27.94, 202.83) * mm, v(25.82, 207.17) * mm]});
            skFitSpline(sketch, "E1392", {"points": [v(65.44, 202.86) * mm, v(65.1, 202.91) * mm, v(63.2, 203.18) * mm, v(61.18, 203.47) * mm]});
            skFitSpline(sketch, "E1393", {"points": [v(61.18, 203.47) * mm, v(57.71, 203.95) * mm, v(57.53, 204) * mm, v(57.64, 204.48) * mm]});
            skFitSpline(sketch, "E1394", {"points": [v(57.64, 204.48) * mm, v(57.75, 204.98) * mm, v(58, 206.53) * mm, v(58.95, 212.79) * mm]});
            skFitSpline(sketch, "E1395", {"points": [v(58.95, 212.79) * mm, v(59.6, 217.09) * mm, v(59.95, 219.03) * mm, v(60.06, 219.03) * mm]});
            skFitSpline(sketch, "E1396", {"points": [v(60.06, 219.03) * mm, v(60.1, 219.03) * mm, v(60.99, 218.76) * mm, v(62.01, 218.43) * mm]});
            skFitSpline(sketch, "E1397", {"points": [v(62.01, 218.43) * mm, v(64.7, 217.56) * mm, v(64.9, 217.5) * mm, v(69.52, 216.15) * mm]});
            skFitSpline(sketch, "E1398", {"points": [v(69.52, 216.15) * mm, v(71.83, 215.48) * mm, v(73.91, 214.85) * mm, v(74.15, 214.75) * mm]});
            skFitSpline(sketch, "E1399", {"points": [v(74.15, 214.75) * mm, v(74.52, 214.6) * mm, v(74, 213.72) * mm, v(70.61, 208.7) * mm]});
            skFitSpline(sketch, "E1400", {"points": [v(70.61, 208.7) * mm, v(68.43, 205.47) * mm, v(66.51, 202.81) * mm, v(66.34, 202.8) * mm]});
            skFitSpline(sketch, "E1401", {"points": [v(66.34, 202.8) * mm, v(66.18, 202.78) * mm, v(65.77, 202.8) * mm, v(65.44, 202.86) * mm]});
            skFitSpline(sketch, "E1402", {"points": [v(-54.44, 212.13) * mm, v(-54.34, 215.86) * mm, v(-54.25, 218.93) * mm, v(-54.23, 218.95) * mm]});
            skFitSpline(sketch, "E1403", {"points": [v(-54.23, 218.95) * mm, v(-54.22, 218.97) * mm, v(-49.9, 220.84) * mm, v(-44.63, 223.1) * mm]});
            skFitSpline(sketch, "E1404", {"points": [v(-44.63, 223.1) * mm, v(-36.8, 226.47) * mm, v(-35, 227.16) * mm, v(-34.76, 226.9) * mm]});
            skFitSpline(sketch, "E1405", {"points": [v(-34.76, 226.9) * mm, v(-34.1, 226.2) * mm, v(-26.48, 216.32) * mm, v(-26.48, 216.17) * mm]});
            skFitSpline(sketch, "E1406", {"points": [v(-26.48, 216.17) * mm, v(-26.48, 216.09) * mm, v(-27.37, 215.67) * mm, v(-28.46, 215.26) * mm]});
            skFitSpline(sketch, "E1407", {"points": [v(-28.46, 215.26) * mm, v(-29.55, 214.84) * mm, v(-35.77, 212.44) * mm, v(-42.27, 209.93) * mm]});
            skFitSpline(sketch, "E1408", {"points": [v(-42.27, 209.93) * mm, v(-48.78, 207.4) * mm, v(-54.22, 205.35) * mm, v(-54.36, 205.35) * mm]});
            skFitSpline(sketch, "E1409", {"points": [v(-54.36, 205.35) * mm, v(-54.54, 205.35) * mm, v(-54.56, 207.42) * mm, v(-54.44, 212.13) * mm]});
            skFitSpline(sketch, "E1410", {"points": [v(-2.58, 225.15) * mm, v(-5.16, 228.58) * mm, v(-7.27, 231.47) * mm, v(-7.28, 231.57) * mm]});
            skFitSpline(sketch, "E1411", {"points": [v(-7.28, 231.57) * mm, v(-7.28, 231.67) * mm, v(-4.27, 231.75) * mm, v(-0.58, 231.75) * mm]});
            skFitSpline(sketch, "E1412", {"points": [v(6.25, 231.09) * mm, v(6.32, 230.72) * mm, v(6.71, 228.05) * mm, v(7.12, 225.15) * mm]});
            skFitSpline(sketch, "E1413", {"points": [v(7.12, 225.15) * mm, v(7.52, 222.24) * mm, v(7.91, 219.57) * mm, v(7.98, 219.2) * mm]});
            skFitSpline(sketch, "E1414", {"points": [v(7.98, 219.2) * mm, v(8.06, 218.84) * mm, v(8.03, 218.57) * mm, v(7.92, 218.6) * mm]});
            skFitSpline(sketch, "E1415", {"points": [v(7.92, 218.6) * mm, v(7.8, 218.62) * mm, v(6.46, 218.7) * mm, v(4.91, 218.78) * mm]});
            skSolve(sketch);
        }
        {
            var Q0;
            Q0 = qSketchRegion(id + "F2", true);
            extrude(context, id + "F3", {"entities" : qUnion([Q0]), "operationType" : NewBodyOperationType.ADD, "depth" : 2 * mm, "offsetDistance" : 25 * mm});
        }
    });
